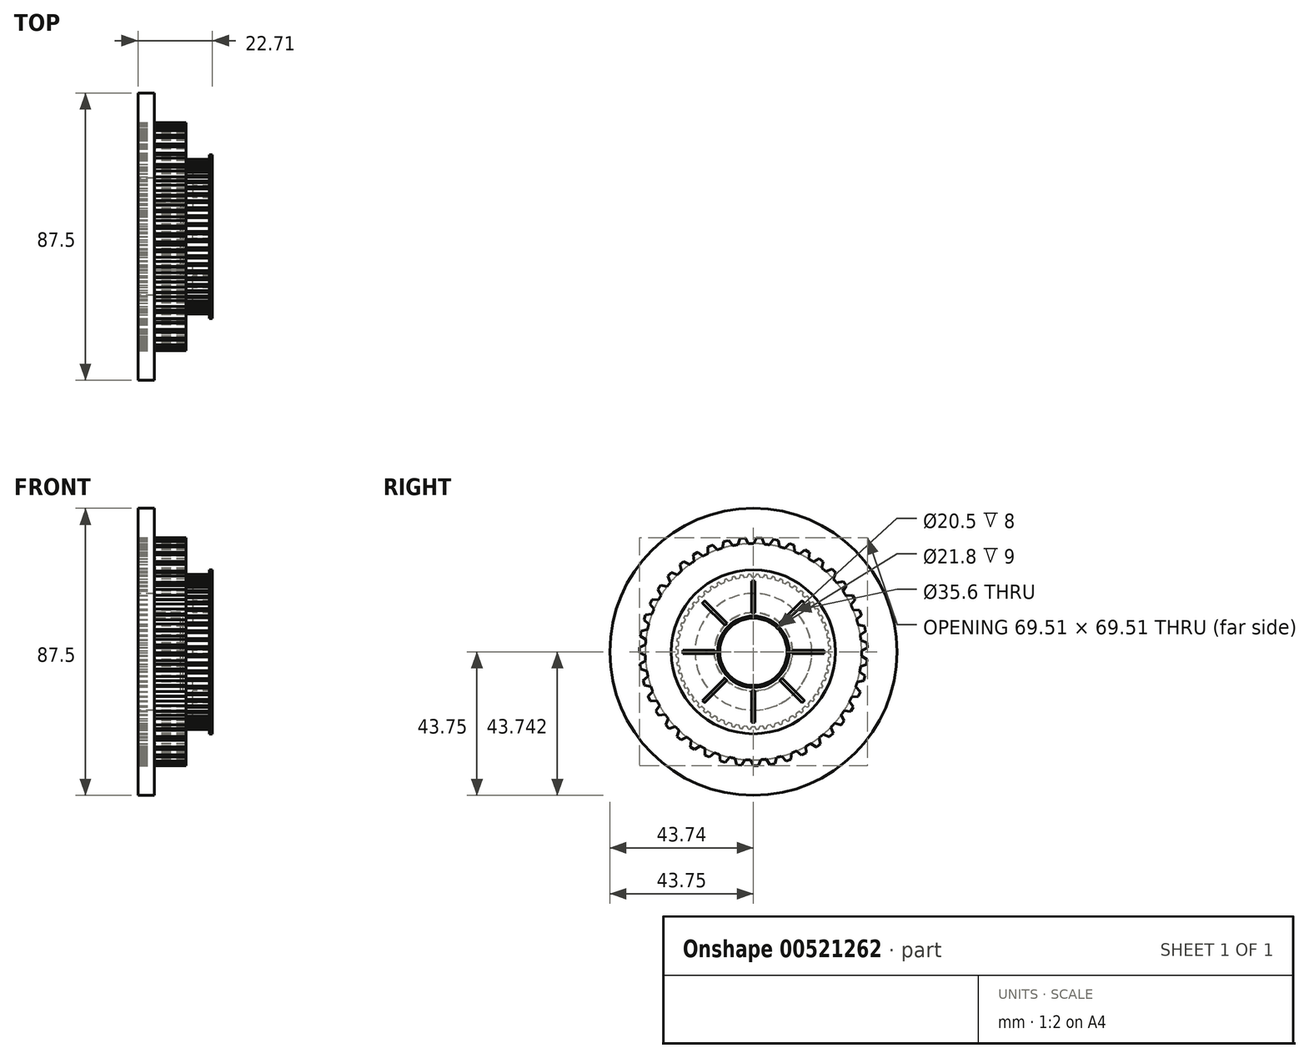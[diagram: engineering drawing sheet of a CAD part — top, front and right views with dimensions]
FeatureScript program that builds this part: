
annotation { "Feature Type Name" : "Feature", "Feature Type Description" : "" }
export const myFeature = defineFeature(function(context is Context, id is Id, definition is map)
    precondition{}
    {
        {
            var Q0;
            Q0=qCreatedBy(makeId("Right.planeOp"),FACE);
            var sketch = newSketch(context, id + "F0", { "sketchPlane" : qUnion([Q0])});
            skCircle(sketch, "E0", {"center": v(0, 0) * mm, "radius": 34.77 * mm, "construction": true});
            skCircle(sketch, "E1", {"center": v(0, 0) * mm, "radius": 10.25 * mm});
            skCircle(sketch, "E2", {"center": v(0, 0) * mm, "radius": 43.75 * mm});
            skCircle(sketch, "E3", {"center": v(0, 0) * mm, "radius": 12 * mm});
            skLineSegment(sketch, "E4", {"start": v(-2.5, 34.67) * mm, "end": v(2.5, 34.67) * mm, "construction": true});
            skCircle(sketch, "E5", {"center": v(0, 0) * mm, "radius": 32.97 * mm});
            skLineSegment(sketch, "E6", {"start": v(0, 0) * mm, "end": v(0, 46.74) * mm, "construction": true});
            skLineSegment(sketch, "E7", {"start": v(-2.5, 34.67) * mm, "end": v(-1.53, 32.93) * mm});
            skLineSegment(sketch, "E8", {"start": v(-1.53, 32.93) * mm, "end": v(0.13, 32.96) * mm});
            skLineSegment(sketch, "E9", {"start": v(0.13, 32.96) * mm, "end": v(1.03, 34.75) * mm});
            skLineSegment(sketch, "E10", {"start": v(1.03, 34.75) * mm, "end": v(2.5, 34.67) * mm});
            skLineSegment(sketch, "E11", {"start": v(-2.5, 34.67) * mm, "end": v(0, 0) * mm, "construction": true});
            skLineSegment(sketch, "E12", {"start": v(1.03, 34.75) * mm, "end": v(0, 0) * mm, "construction": true});
            skLineSegment(sketch, "E13", {"start": v(-2.5, 34.67) * mm, "end": v(-2.37, 32.88) * mm, "construction": true});
            skLineSegment(sketch, "E14", {"start": v(-2.37, 32.88) * mm, "end": v(0.13, 32.96) * mm});
            skLineSegment(sketch, "E15.1.0", {"start": v(-7.52, 33.94) * mm, "end": v(-6.3, 32.36) * mm});
            skLineSegment(sketch, "E15.1.1", {"start": v(-6.3, 32.36) * mm, "end": v(-4.67, 32.63) * mm});
            skLineSegment(sketch, "E15.1.2", {"start": v(-4.67, 32.63) * mm, "end": v(-4.05, 34.53) * mm});
            skLineSegment(sketch, "E15.1.3", {"start": v(-4.05, 34.53) * mm, "end": v(-2.58, 34.67) * mm});
            skLineSegment(sketch, "E15.2.0", {"start": v(-12.38, 32.48) * mm, "end": v(-10.95, 31.1) * mm});
            skLineSegment(sketch, "E15.2.1", {"start": v(-10.95, 31.1) * mm, "end": v(-9.37, 31.6) * mm});
            skLineSegment(sketch, "E15.2.2", {"start": v(-9.37, 31.6) * mm, "end": v(-9.03, 33.57) * mm});
            skLineSegment(sketch, "E15.2.3", {"start": v(-9.03, 33.57) * mm, "end": v(-7.6, 33.93) * mm});
            skLineSegment(sketch, "E15.3.0", {"start": v(-16.98, 30.34) * mm, "end": v(-15.36, 29.17) * mm});
            skLineSegment(sketch, "E15.3.1", {"start": v(-15.36, 29.17) * mm, "end": v(-13.88, 29.9) * mm});
            skLineSegment(sketch, "E15.3.2", {"start": v(-13.88, 29.9) * mm, "end": v(-13.82, 31.9) * mm});
            skLineSegment(sketch, "E15.3.3", {"start": v(-13.82, 31.9) * mm, "end": v(-12.45, 32.46) * mm});
            skLineSegment(sketch, "E15.4.0", {"start": v(-21.22, 27.54) * mm, "end": v(-19.44, 26.62) * mm});
            skLineSegment(sketch, "E15.4.1", {"start": v(-19.44, 26.62) * mm, "end": v(-18.08, 27.56) * mm});
            skLineSegment(sketch, "E15.4.2", {"start": v(-18.08, 27.56) * mm, "end": v(-18.32, 29.55) * mm});
            skLineSegment(sketch, "E15.4.3", {"start": v(-18.32, 29.55) * mm, "end": v(-17.05, 30.3) * mm});
            skLineSegment(sketch, "E15.5.0", {"start": v(-25, 24.16) * mm, "end": v(-23.11, 23.5) * mm});
            skLineSegment(sketch, "E15.5.1", {"start": v(-23.11, 23.5) * mm, "end": v(-21.9, 24.64) * mm});
            skLineSegment(sketch, "E15.5.2", {"start": v(-21.9, 24.64) * mm, "end": v(-22.43, 26.57) * mm});
            skLineSegment(sketch, "E15.5.3", {"start": v(-22.43, 26.57) * mm, "end": v(-21.28, 27.5) * mm});
            skLineSegment(sketch, "E15.6.0", {"start": v(-28.25, 20.26) * mm, "end": v(-26.29, 19.9) * mm});
            skLineSegment(sketch, "E15.6.1", {"start": v(-26.29, 19.9) * mm, "end": v(-25.26, 21.19) * mm});
            skLineSegment(sketch, "E15.6.2", {"start": v(-25.26, 21.19) * mm, "end": v(-26.05, 23.02) * mm});
            skLineSegment(sketch, "E15.6.3", {"start": v(-26.05, 23.02) * mm, "end": v(-25.05, 24.1) * mm});
            skLineSegment(sketch, "E15.7.0", {"start": v(-30.9, 15.93) * mm, "end": v(-28.9, 15.85) * mm});
            skLineSegment(sketch, "E15.7.1", {"start": v(-28.9, 15.85) * mm, "end": v(-28.07, 17.28) * mm});
            skLineSegment(sketch, "E15.7.2", {"start": v(-28.07, 17.28) * mm, "end": v(-29.13, 18.98) * mm});
            skLineSegment(sketch, "E15.7.3", {"start": v(-29.13, 18.98) * mm, "end": v(-28.3, 20.2) * mm});
            skLineSegment(sketch, "E15.8.0", {"start": v(-32.9, 11.26) * mm, "end": v(-30.9, 11.47) * mm});
            skLineSegment(sketch, "E15.8.1", {"start": v(-30.9, 11.47) * mm, "end": v(-30.29, 13.01) * mm});
            skLineSegment(sketch, "E15.8.2", {"start": v(-30.29, 13.01) * mm, "end": v(-31.58, 14.53) * mm});
            skLineSegment(sketch, "E15.8.3", {"start": v(-31.58, 14.53) * mm, "end": v(-30.94, 15.86) * mm});
            skLineSegment(sketch, "E15.9.0", {"start": v(-34.18, 6.35) * mm, "end": v(-32.25, 6.85) * mm});
            skLineSegment(sketch, "E15.9.1", {"start": v(-32.25, 6.85) * mm, "end": v(-31.86, 8.46) * mm});
            skLineSegment(sketch, "E15.9.2", {"start": v(-31.86, 8.46) * mm, "end": v(-33.36, 9.78) * mm});
            skLineSegment(sketch, "E15.9.3", {"start": v(-33.36, 9.78) * mm, "end": v(-32.92, 11.19) * mm});
            skLineSegment(sketch, "E15.10.0", {"start": v(-34.74, 1.3) * mm, "end": v(-32.9, 2.08) * mm});
            skLineSegment(sketch, "E15.10.1", {"start": v(-32.9, 2.08) * mm, "end": v(-32.75, 3.73) * mm});
            skLineSegment(sketch, "E15.10.2", {"start": v(-32.75, 3.73) * mm, "end": v(-34.43, 4.82) * mm});
            skLineSegment(sketch, "E15.10.3", {"start": v(-34.43, 4.82) * mm, "end": v(-34.2, 6.28) * mm});
            skLineSegment(sketch, "E15.11.0", {"start": v(-34.56, -3.76) * mm, "end": v(-32.85, -2.73) * mm});
            skLineSegment(sketch, "E15.11.1", {"start": v(-32.85, -2.73) * mm, "end": v(-32.95, -1.08) * mm});
            skLineSegment(sketch, "E15.11.2", {"start": v(-32.95, -1.08) * mm, "end": v(-34.76, -0.24) * mm});
            skLineSegment(sketch, "E15.11.3", {"start": v(-34.76, -0.24) * mm, "end": v(-34.74, 1.23) * mm});
            skLineSegment(sketch, "E15.12.0", {"start": v(-33.64, -8.76) * mm, "end": v(-32.1, -7.48) * mm});
            skLineSegment(sketch, "E15.12.1", {"start": v(-32.1, -7.48) * mm, "end": v(-32.44, -5.86) * mm});
            skLineSegment(sketch, "E15.12.2", {"start": v(-32.44, -5.86) * mm, "end": v(-34.36, -5.3) * mm});
            skLineSegment(sketch, "E15.12.3", {"start": v(-34.36, -5.3) * mm, "end": v(-34.55, -3.84) * mm});
            skLineSegment(sketch, "E15.13.0", {"start": v(-32.01, -13.56) * mm, "end": v(-30.67, -12.08) * mm});
            skLineSegment(sketch, "E15.13.1", {"start": v(-30.67, -12.08) * mm, "end": v(-31.24, -10.52) * mm});
            skLineSegment(sketch, "E15.13.2", {"start": v(-31.24, -10.52) * mm, "end": v(-33.22, -10.25) * mm});
            skLineSegment(sketch, "E15.13.3", {"start": v(-33.22, -10.25) * mm, "end": v(-33.62, -8.83) * mm});
            skLineSegment(sketch, "E15.14.0", {"start": v(-29.7, -18.08) * mm, "end": v(-28.59, -16.42) * mm});
            skLineSegment(sketch, "E15.14.1", {"start": v(-28.59, -16.42) * mm, "end": v(-29.38, -14.96) * mm});
            skLineSegment(sketch, "E15.14.2", {"start": v(-29.38, -14.96) * mm, "end": v(-31.37, -14.98) * mm});
            skLineSegment(sketch, "E15.14.3", {"start": v(-31.37, -14.98) * mm, "end": v(-31.98, -13.63) * mm});
            skLineSegment(sketch, "E15.15.0", {"start": v(-26.75, -22.2) * mm, "end": v(-25.9, -20.4) * mm});
            skLineSegment(sketch, "E15.15.1", {"start": v(-25.9, -20.4) * mm, "end": v(-26.88, -19.08) * mm});
            skLineSegment(sketch, "E15.15.2", {"start": v(-26.88, -19.08) * mm, "end": v(-28.86, -19.39) * mm});
            skLineSegment(sketch, "E15.15.3", {"start": v(-28.86, -19.39) * mm, "end": v(-29.66, -18.14) * mm});
            skLineSegment(sketch, "E15.16.0", {"start": v(-23.23, -25.87) * mm, "end": v(-22.65, -23.96) * mm});
            skLineSegment(sketch, "E15.16.1", {"start": v(-22.65, -23.96) * mm, "end": v(-23.82, -22.79) * mm});
            skLineSegment(sketch, "E15.16.2", {"start": v(-23.82, -22.79) * mm, "end": v(-25.73, -23.38) * mm});
            skLineSegment(sketch, "E15.16.3", {"start": v(-25.73, -23.38) * mm, "end": v(-26.7, -22.27) * mm});
            skLineSegment(sketch, "E15.17.0", {"start": v(-19.21, -28.97) * mm, "end": v(-18.92, -27) * mm});
            skLineSegment(sketch, "E15.17.1", {"start": v(-18.92, -27) * mm, "end": v(-20.25, -26.01) * mm});
            skLineSegment(sketch, "E15.17.2", {"start": v(-20.25, -26.01) * mm, "end": v(-22.05, -26.88) * mm});
            skLineSegment(sketch, "E15.17.3", {"start": v(-22.05, -26.88) * mm, "end": v(-23.17, -25.92) * mm});
            skLineSegment(sketch, "E15.18.0", {"start": v(-14.8, -31.46) * mm, "end": v(-14.78, -29.46) * mm});
            skLineSegment(sketch, "E15.18.1", {"start": v(-14.78, -29.46) * mm, "end": v(-16.25, -28.68) * mm});
            skLineSegment(sketch, "E15.18.2", {"start": v(-16.25, -28.68) * mm, "end": v(-17.9, -29.8) * mm});
            skLineSegment(sketch, "E15.18.3", {"start": v(-17.9, -29.8) * mm, "end": v(-19.15, -29.01) * mm});
            skLineSegment(sketch, "E15.19.0", {"start": v(-10.05, -33.28) * mm, "end": v(-10.34, -31.3) * mm});
            skLineSegment(sketch, "E15.19.1", {"start": v(-10.34, -31.3) * mm, "end": v(-11.9, -30.74) * mm});
            skLineSegment(sketch, "E15.19.2", {"start": v(-11.9, -30.74) * mm, "end": v(-13.37, -32.1) * mm});
            skLineSegment(sketch, "E15.19.3", {"start": v(-13.37, -32.1) * mm, "end": v(-14.72, -31.5) * mm});
            skLineSegment(sketch, "E15.20.0", {"start": v(-5.1, -34.39) * mm, "end": v(-5.67, -32.47) * mm});
            skLineSegment(sketch, "E15.20.1", {"start": v(-5.67, -32.47) * mm, "end": v(-7.3, -32.15) * mm});
            skLineSegment(sketch, "E15.20.2", {"start": v(-7.3, -32.15) * mm, "end": v(-8.56, -33.7) * mm});
            skLineSegment(sketch, "E15.20.3", {"start": v(-8.56, -33.7) * mm, "end": v(-9.98, -33.3) * mm});
            skLineSegment(sketch, "E15.21.0", {"start": v(-0.04, -34.76) * mm, "end": v(-0.88, -32.95) * mm});
            skLineSegment(sketch, "E15.21.1", {"start": v(-0.88, -32.95) * mm, "end": v(-2.53, -32.87) * mm});
            skLineSegment(sketch, "E15.21.2", {"start": v(-2.53, -32.87) * mm, "end": v(-3.56, -34.58) * mm});
            skLineSegment(sketch, "E15.21.3", {"start": v(-3.56, -34.58) * mm, "end": v(-5.02, -34.4) * mm});
            skLineSegment(sketch, "E15.22.0", {"start": v(5.02, -34.4) * mm, "end": v(3.93, -32.73) * mm});
            skLineSegment(sketch, "E15.22.1", {"start": v(3.93, -32.73) * mm, "end": v(2.28, -32.89) * mm});
            skLineSegment(sketch, "E15.22.2", {"start": v(2.28, -32.89) * mm, "end": v(1.51, -34.73) * mm});
            skLineSegment(sketch, "E15.22.3", {"start": v(1.51, -34.73) * mm, "end": v(0.04, -34.76) * mm});
            skLineSegment(sketch, "E15.23.0", {"start": v(9.98, -33.3) * mm, "end": v(8.65, -31.8) * mm});
            skLineSegment(sketch, "E15.23.1", {"start": v(8.65, -31.8) * mm, "end": v(7.04, -32.2) * mm});
            skLineSegment(sketch, "E15.23.2", {"start": v(7.04, -32.2) * mm, "end": v(6.55, -34.14) * mm});
            skLineSegment(sketch, "E15.23.3", {"start": v(6.55, -34.14) * mm, "end": v(5.1, -34.39) * mm});
            skLineSegment(sketch, "E15.24.0", {"start": v(14.72, -31.5) * mm, "end": v(13.2, -30.21) * mm});
            skLineSegment(sketch, "E15.24.1", {"start": v(13.2, -30.21) * mm, "end": v(11.66, -30.84) * mm});
            skLineSegment(sketch, "E15.24.2", {"start": v(11.66, -30.84) * mm, "end": v(11.46, -32.82) * mm});
            skLineSegment(sketch, "E15.24.3", {"start": v(11.46, -32.82) * mm, "end": v(10.05, -33.28) * mm});
            skLineSegment(sketch, "E15.25.0", {"start": v(19.15, -29.01) * mm, "end": v(17.45, -27.97) * mm});
            skLineSegment(sketch, "E15.25.1", {"start": v(17.45, -27.97) * mm, "end": v(16.02, -28.8) * mm});
            skLineSegment(sketch, "E15.25.2", {"start": v(16.02, -28.8) * mm, "end": v(16.11, -30.8) * mm});
            skLineSegment(sketch, "E15.25.3", {"start": v(16.11, -30.8) * mm, "end": v(14.8, -31.46) * mm});
            skLineSegment(sketch, "E15.26.0", {"start": v(23.17, -25.92) * mm, "end": v(21.33, -25.13) * mm});
            skLineSegment(sketch, "E15.26.1", {"start": v(21.33, -25.13) * mm, "end": v(20.05, -26.17) * mm});
            skLineSegment(sketch, "E15.26.2", {"start": v(20.05, -26.17) * mm, "end": v(20.43, -28.13) * mm});
            skLineSegment(sketch, "E15.26.3", {"start": v(20.43, -28.13) * mm, "end": v(19.21, -28.97) * mm});
            skLineSegment(sketch, "E15.27.0", {"start": v(26.7, -22.27) * mm, "end": v(24.77, -21.76) * mm});
            skLineSegment(sketch, "E15.27.1", {"start": v(24.77, -21.76) * mm, "end": v(23.64, -22.97) * mm});
            skLineSegment(sketch, "E15.27.2", {"start": v(23.64, -22.97) * mm, "end": v(24.3, -24.86) * mm});
            skLineSegment(sketch, "E15.27.3", {"start": v(24.3, -24.86) * mm, "end": v(23.23, -25.87) * mm});
            skLineSegment(sketch, "E15.28.0", {"start": v(29.66, -18.14) * mm, "end": v(27.67, -17.92) * mm});
            skLineSegment(sketch, "E15.28.1", {"start": v(27.67, -17.92) * mm, "end": v(26.74, -19.28) * mm});
            skLineSegment(sketch, "E15.28.2", {"start": v(26.74, -19.28) * mm, "end": v(27.67, -21.05) * mm});
            skLineSegment(sketch, "E15.28.3", {"start": v(27.67, -21.05) * mm, "end": v(26.75, -22.2) * mm});
            skLineSegment(sketch, "E15.29.0", {"start": v(31.98, -13.63) * mm, "end": v(29.98, -13.7) * mm});
            skLineSegment(sketch, "E15.29.1", {"start": v(29.98, -13.7) * mm, "end": v(29.26, -15.19) * mm});
            skLineSegment(sketch, "E15.29.2", {"start": v(29.26, -15.19) * mm, "end": v(30.44, -16.8) * mm});
            skLineSegment(sketch, "E15.29.3", {"start": v(30.44, -16.8) * mm, "end": v(29.7, -18.08) * mm});
            skLineSegment(sketch, "E15.30.0", {"start": v(33.62, -8.83) * mm, "end": v(31.66, -9.19) * mm});
            skLineSegment(sketch, "E15.30.1", {"start": v(31.66, -9.19) * mm, "end": v(31.16, -10.76) * mm});
            skLineSegment(sketch, "E15.30.2", {"start": v(31.16, -10.76) * mm, "end": v(32.56, -12.2) * mm});
            skLineSegment(sketch, "E15.30.3", {"start": v(32.56, -12.2) * mm, "end": v(32.01, -13.56) * mm});
            skLineSegment(sketch, "E15.31.0", {"start": v(34.55, -3.84) * mm, "end": v(32.66, -4.48) * mm});
            skLineSegment(sketch, "E15.31.1", {"start": v(32.66, -4.48) * mm, "end": v(32.4, -6.11) * mm});
            skLineSegment(sketch, "E15.31.2", {"start": v(32.4, -6.11) * mm, "end": v(33.99, -7.32) * mm});
            skLineSegment(sketch, "E15.31.3", {"start": v(33.99, -7.32) * mm, "end": v(33.64, -8.76) * mm});
            skLineSegment(sketch, "E15.32.0", {"start": v(34.74, 1.23) * mm, "end": v(32.96, 0.32) * mm});
            skLineSegment(sketch, "E15.32.1", {"start": v(32.96, 0.32) * mm, "end": v(32.94, -1.33) * mm});
            skLineSegment(sketch, "E15.32.2", {"start": v(32.94, -1.33) * mm, "end": v(34.69, -2.3) * mm});
            skLineSegment(sketch, "E15.32.3", {"start": v(34.69, -2.3) * mm, "end": v(34.56, -3.76) * mm});
            skLineSegment(sketch, "E15.33.0", {"start": v(34.2, 6.28) * mm, "end": v(32.56, 5.12) * mm});
            skLineSegment(sketch, "E15.33.1", {"start": v(32.56, 5.12) * mm, "end": v(32.78, 3.48) * mm});
            skLineSegment(sketch, "E15.33.2", {"start": v(32.78, 3.48) * mm, "end": v(34.65, 2.78) * mm});
            skLineSegment(sketch, "E15.33.3", {"start": v(34.65, 2.78) * mm, "end": v(34.74, 1.3) * mm});
            skLineSegment(sketch, "E15.34.0", {"start": v(32.92, 11.19) * mm, "end": v(31.47, 9.8) * mm});
            skLineSegment(sketch, "E15.34.1", {"start": v(31.47, 9.8) * mm, "end": v(31.93, 8.21) * mm});
            skLineSegment(sketch, "E15.34.2", {"start": v(31.93, 8.21) * mm, "end": v(33.88, 7.8) * mm});
            skLineSegment(sketch, "E15.34.3", {"start": v(33.88, 7.8) * mm, "end": v(34.18, 6.35) * mm});
            skLineSegment(sketch, "E15.35.0", {"start": v(30.94, 15.86) * mm, "end": v(29.7, 14.28) * mm});
            skLineSegment(sketch, "E15.35.1", {"start": v(29.7, 14.28) * mm, "end": v(30.39, 12.77) * mm});
            skLineSegment(sketch, "E15.35.2", {"start": v(30.39, 12.77) * mm, "end": v(32.38, 12.65) * mm});
            skLineSegment(sketch, "E15.35.3", {"start": v(32.38, 12.65) * mm, "end": v(32.9, 11.26) * mm});
            skLineSegment(sketch, "E15.36.0", {"start": v(28.3, 20.2) * mm, "end": v(27.31, 18.46) * mm});
            skLineSegment(sketch, "E15.36.1", {"start": v(27.31, 18.46) * mm, "end": v(28.2, 17.06) * mm});
            skLineSegment(sketch, "E15.36.2", {"start": v(28.2, 17.06) * mm, "end": v(30.2, 17.23) * mm});
            skLineSegment(sketch, "E15.36.3", {"start": v(30.2, 17.23) * mm, "end": v(30.9, 15.93) * mm});
            skLineSegment(sketch, "E15.37.0", {"start": v(25.05, 24.1) * mm, "end": v(24.33, 22.24) * mm});
            skLineSegment(sketch, "E15.37.1", {"start": v(24.33, 22.24) * mm, "end": v(25.42, 20.99) * mm});
            skLineSegment(sketch, "E15.37.2", {"start": v(25.42, 20.99) * mm, "end": v(27.37, 21.44) * mm});
            skLineSegment(sketch, "E15.37.3", {"start": v(27.37, 21.44) * mm, "end": v(28.25, 20.26) * mm});
            skLineSegment(sketch, "E15.38.0", {"start": v(21.28, 27.5) * mm, "end": v(20.84, 25.54) * mm});
            skLineSegment(sketch, "E15.38.1", {"start": v(20.84, 25.54) * mm, "end": v(22.1, 24.47) * mm});
            skLineSegment(sketch, "E15.38.2", {"start": v(22.1, 24.47) * mm, "end": v(23.95, 25.2) * mm});
            skLineSegment(sketch, "E15.38.3", {"start": v(23.95, 25.2) * mm, "end": v(25, 24.16) * mm});
            skLineSegment(sketch, "E15.39.0", {"start": v(17.05, 30.3) * mm, "end": v(16.9, 28.3) * mm});
            skLineSegment(sketch, "E15.39.1", {"start": v(16.9, 28.3) * mm, "end": v(18.3, 27.42) * mm});
            skLineSegment(sketch, "E15.39.2", {"start": v(18.3, 27.42) * mm, "end": v(20.03, 28.42) * mm});
            skLineSegment(sketch, "E15.39.3", {"start": v(20.03, 28.42) * mm, "end": v(21.22, 27.54) * mm});
            skLineSegment(sketch, "E15.40.0", {"start": v(12.45, 32.46) * mm, "end": v(12.6, 30.46) * mm});
            skLineSegment(sketch, "E15.40.1", {"start": v(12.6, 30.46) * mm, "end": v(14.1, 29.8) * mm});
            skLineSegment(sketch, "E15.40.2", {"start": v(14.1, 29.8) * mm, "end": v(15.68, 31.03) * mm});
            skLineSegment(sketch, "E15.40.3", {"start": v(15.68, 31.03) * mm, "end": v(16.98, 30.34) * mm});
            skLineSegment(sketch, "E15.41.0", {"start": v(7.6, 33.93) * mm, "end": v(8.02, 31.97) * mm});
            skLineSegment(sketch, "E15.41.1", {"start": v(8.02, 31.97) * mm, "end": v(9.62, 31.53) * mm});
            skLineSegment(sketch, "E15.41.2", {"start": v(9.62, 31.53) * mm, "end": v(11, 32.98) * mm});
            skLineSegment(sketch, "E15.41.3", {"start": v(11, 32.98) * mm, "end": v(12.38, 32.48) * mm});
            skLineSegment(sketch, "E15.42.0", {"start": v(2.58, 34.67) * mm, "end": v(3.28, 32.8) * mm});
            skLineSegment(sketch, "E15.42.1", {"start": v(3.28, 32.8) * mm, "end": v(4.93, 32.6) * mm});
            skLineSegment(sketch, "E15.42.2", {"start": v(4.93, 32.6) * mm, "end": v(6.07, 34.23) * mm});
            skLineSegment(sketch, "E15.42.3", {"start": v(6.07, 34.23) * mm, "end": v(7.52, 33.94) * mm});
            skLineSegment(sketch, "E16", {"start": v(2.5, 34.67) * mm, "end": v(2.58, 34.67) * mm});
            skLineSegment(sketch, "E17.1.0", {"start": v(-2.58, 34.67) * mm, "end": v(-2.5, 34.67) * mm});
            skLineSegment(sketch, "E17.2.0", {"start": v(-7.6, 33.93) * mm, "end": v(-7.52, 33.94) * mm});
            skLineSegment(sketch, "E17.3.0", {"start": v(-12.45, 32.46) * mm, "end": v(-12.38, 32.48) * mm});
            skLineSegment(sketch, "E17.4.0", {"start": v(-17.05, 30.3) * mm, "end": v(-16.98, 30.34) * mm});
            skLineSegment(sketch, "E17.5.0", {"start": v(-21.28, 27.5) * mm, "end": v(-21.22, 27.54) * mm});
            skLineSegment(sketch, "E17.6.0", {"start": v(-25.05, 24.1) * mm, "end": v(-25, 24.16) * mm});
            skLineSegment(sketch, "E17.7.0", {"start": v(-28.3, 20.2) * mm, "end": v(-28.25, 20.26) * mm});
            skLineSegment(sketch, "E17.8.0", {"start": v(-30.94, 15.86) * mm, "end": v(-30.9, 15.93) * mm});
            skLineSegment(sketch, "E17.9.0", {"start": v(-32.92, 11.19) * mm, "end": v(-32.9, 11.26) * mm});
            skLineSegment(sketch, "E17.10.0", {"start": v(-34.2, 6.28) * mm, "end": v(-34.18, 6.35) * mm});
            skLineSegment(sketch, "E17.11.0", {"start": v(-34.74, 1.23) * mm, "end": v(-34.74, 1.3) * mm});
            skLineSegment(sketch, "E17.12.0", {"start": v(-34.55, -3.84) * mm, "end": v(-34.56, -3.76) * mm});
            skLineSegment(sketch, "E17.13.0", {"start": v(-33.62, -8.83) * mm, "end": v(-33.64, -8.76) * mm});
            skLineSegment(sketch, "E17.14.0", {"start": v(-31.98, -13.63) * mm, "end": v(-32.01, -13.56) * mm});
            skLineSegment(sketch, "E17.15.0", {"start": v(-29.66, -18.14) * mm, "end": v(-29.7, -18.08) * mm});
            skLineSegment(sketch, "E17.16.0", {"start": v(-26.7, -22.27) * mm, "end": v(-26.75, -22.2) * mm});
            skLineSegment(sketch, "E17.17.0", {"start": v(-23.17, -25.92) * mm, "end": v(-23.23, -25.87) * mm});
            skLineSegment(sketch, "E17.18.0", {"start": v(-19.15, -29.01) * mm, "end": v(-19.21, -28.97) * mm});
            skLineSegment(sketch, "E17.19.0", {"start": v(-14.72, -31.5) * mm, "end": v(-14.8, -31.46) * mm});
            skLineSegment(sketch, "E17.20.0", {"start": v(-9.98, -33.3) * mm, "end": v(-10.05, -33.28) * mm});
            skLineSegment(sketch, "E17.21.0", {"start": v(-5.02, -34.4) * mm, "end": v(-5.1, -34.39) * mm});
            skLineSegment(sketch, "E17.22.0", {"start": v(0.04, -34.76) * mm, "end": v(-0.04, -34.76) * mm});
            skLineSegment(sketch, "E17.23.0", {"start": v(5.1, -34.39) * mm, "end": v(5.02, -34.4) * mm});
            skLineSegment(sketch, "E17.24.0", {"start": v(10.05, -33.28) * mm, "end": v(9.98, -33.3) * mm});
            skLineSegment(sketch, "E17.25.0", {"start": v(14.8, -31.46) * mm, "end": v(14.72, -31.5) * mm});
            skLineSegment(sketch, "E17.26.0", {"start": v(19.21, -28.97) * mm, "end": v(19.15, -29.01) * mm});
            skLineSegment(sketch, "E17.27.0", {"start": v(23.23, -25.87) * mm, "end": v(23.17, -25.92) * mm});
            skLineSegment(sketch, "E17.28.0", {"start": v(26.75, -22.2) * mm, "end": v(26.7, -22.27) * mm});
            skLineSegment(sketch, "E17.29.0", {"start": v(29.7, -18.08) * mm, "end": v(29.66, -18.14) * mm});
            skLineSegment(sketch, "E17.30.0", {"start": v(32.01, -13.56) * mm, "end": v(31.98, -13.63) * mm});
            skLineSegment(sketch, "E17.31.0", {"start": v(33.64, -8.76) * mm, "end": v(33.62, -8.83) * mm});
            skLineSegment(sketch, "E17.32.0", {"start": v(34.56, -3.76) * mm, "end": v(34.55, -3.84) * mm});
            skLineSegment(sketch, "E17.33.0", {"start": v(34.74, 1.3) * mm, "end": v(34.74, 1.23) * mm});
            skLineSegment(sketch, "E17.34.0", {"start": v(34.18, 6.35) * mm, "end": v(34.2, 6.28) * mm});
            skLineSegment(sketch, "E17.35.0", {"start": v(32.9, 11.26) * mm, "end": v(32.92, 11.19) * mm});
            skLineSegment(sketch, "E17.36.0", {"start": v(30.9, 15.93) * mm, "end": v(30.94, 15.86) * mm});
            skLineSegment(sketch, "E17.37.0", {"start": v(28.25, 20.26) * mm, "end": v(28.3, 20.2) * mm});
            skLineSegment(sketch, "E17.38.0", {"start": v(25, 24.16) * mm, "end": v(25.05, 24.1) * mm});
            skLineSegment(sketch, "E17.39.0", {"start": v(21.22, 27.54) * mm, "end": v(21.28, 27.5) * mm});
            skLineSegment(sketch, "E17.40.0", {"start": v(16.98, 30.34) * mm, "end": v(17.05, 30.3) * mm});
            skLineSegment(sketch, "E17.41.0", {"start": v(12.38, 32.48) * mm, "end": v(12.45, 32.46) * mm});
            skLineSegment(sketch, "E17.42.0", {"start": v(7.52, 33.94) * mm, "end": v(7.6, 33.93) * mm});
            skSolve(sketch);
        }
        {
            var Q0;
            {var subQ1=sQuery(id+"F0.wireOp",EDGE,"E15.4.0");Q0=makeQuery(id+"F0.imprint","IMPRINT",FACE,{"disambiguationData":[TD([[makeQuery(id+"F0.imprint","IMPRINT",EDGE,{"derivedFrom":subQ1}),-1.0]])]});}
            var Q1;
            {var subQ1=sQuery(id+"F0.wireOp",EDGE,"E15.28.0");Q1=makeQuery(id+"F0.imprint","IMPRINT",FACE,{"disambiguationData":[TD([[makeQuery(id+"F0.imprint","IMPRINT",EDGE,{"derivedFrom":subQ1}),-1.0]])]});}
            var Q2;
            {var subQ1=sQuery(id+"F0.wireOp",EDGE,"E15.41.0");Q2=makeQuery(id+"F0.imprint","IMPRINT",FACE,{"disambiguationData":[TD([[makeQuery(id+"F0.imprint","IMPRINT",EDGE,{"derivedFrom":subQ1}),-1.0]])]});}
            var Q3;
            {var subQ1=sQuery(id+"F0.wireOp",EDGE,"E15.2.0");Q3=makeQuery(id+"F0.imprint","IMPRINT",FACE,{"disambiguationData":[TD([[makeQuery(id+"F0.imprint","IMPRINT",EDGE,{"derivedFrom":subQ1}),-1.0]])]});}
            var Q4;
            {var subQ1=sQuery(id+"F0.wireOp",EDGE,"E15.10.0");Q4=makeQuery(id+"F0.imprint","IMPRINT",FACE,{"disambiguationData":[TD([[makeQuery(id+"F0.imprint","IMPRINT",EDGE,{"derivedFrom":subQ1}),-1.0]])]});}
            var Q5;
            {var subQ1=sQuery(id+"F0.wireOp",EDGE,"E15.26.0");Q5=makeQuery(id+"F0.imprint","IMPRINT",FACE,{"disambiguationData":[TD([[makeQuery(id+"F0.imprint","IMPRINT",EDGE,{"derivedFrom":subQ1}),-1.0]])]});}
            var Q6;
            {var subQ1=sQuery(id+"F0.wireOp",EDGE,"E15.18.0");Q6=makeQuery(id+"F0.imprint","IMPRINT",FACE,{"disambiguationData":[TD([[makeQuery(id+"F0.imprint","IMPRINT",EDGE,{"derivedFrom":subQ1}),-1.0]])]});}
            var Q7;
            {var subQ1=sQuery(id+"F0.wireOp",EDGE,"E15.6.0");Q7=makeQuery(id+"F0.imprint","IMPRINT",FACE,{"disambiguationData":[TD([[makeQuery(id+"F0.imprint","IMPRINT",EDGE,{"derivedFrom":subQ1}),-1.0]])]});}
            var Q8;
            {var subQ1=sQuery(id+"F0.wireOp",EDGE,"E15.14.0");Q8=makeQuery(id+"F0.imprint","IMPRINT",FACE,{"disambiguationData":[TD([[makeQuery(id+"F0.imprint","IMPRINT",EDGE,{"derivedFrom":subQ1}),-1.0]])]});}
            var Q9;
            {var subQ1=sQuery(id+"F0.wireOp",EDGE,"E15.22.0");Q9=makeQuery(id+"F0.imprint","IMPRINT",FACE,{"disambiguationData":[TD([[makeQuery(id+"F0.imprint","IMPRINT",EDGE,{"derivedFrom":subQ1}),-1.0]])]});}
            var Q10;
            {var subQ1=sQuery(id+"F0.wireOp",EDGE,"E15.30.0");Q10=makeQuery(id+"F0.imprint","IMPRINT",FACE,{"disambiguationData":[TD([[makeQuery(id+"F0.imprint","IMPRINT",EDGE,{"derivedFrom":subQ1}),-1.0]])]});}
            var Q11;
            {var subQ1=sQuery(id+"F0.wireOp",EDGE,"E15.31.0");Q11=makeQuery(id+"F0.imprint","IMPRINT",FACE,{"disambiguationData":[TD([[makeQuery(id+"F0.imprint","IMPRINT",EDGE,{"derivedFrom":subQ1}),-1.0]])]});}
            var Q12;
            {var subQ1=sQuery(id+"F0.wireOp",EDGE,"E15.15.0");Q12=makeQuery(id+"F0.imprint","IMPRINT",FACE,{"disambiguationData":[TD([[makeQuery(id+"F0.imprint","IMPRINT",EDGE,{"derivedFrom":subQ1}),-1.0]])]});}
            var Q13;
            {var subQ1=sQuery(id+"F0.wireOp",EDGE,"E15.7.0");Q13=makeQuery(id+"F0.imprint","IMPRINT",FACE,{"disambiguationData":[TD([[makeQuery(id+"F0.imprint","IMPRINT",EDGE,{"derivedFrom":subQ1}),-1.0]])]});}
            var Q14;
            {var subQ1=sQuery(id+"F0.wireOp",EDGE,"E15.25.0");Q14=makeQuery(id+"F0.imprint","IMPRINT",FACE,{"disambiguationData":[TD([[makeQuery(id+"F0.imprint","IMPRINT",EDGE,{"derivedFrom":subQ1}),-1.0]])]});}
            var Q15;
            {var subQ1=sQuery(id+"F0.wireOp",EDGE,"E15.39.0");Q15=makeQuery(id+"F0.imprint","IMPRINT",FACE,{"disambiguationData":[TD([[makeQuery(id+"F0.imprint","IMPRINT",EDGE,{"derivedFrom":subQ1}),-1.0]])]});}
            var Q16;
            {var subQ1=sQuery(id+"F0.wireOp",EDGE,"E15.34.0");Q16=makeQuery(id+"F0.imprint","IMPRINT",FACE,{"disambiguationData":[TD([[makeQuery(id+"F0.imprint","IMPRINT",EDGE,{"derivedFrom":subQ1}),-1.0]])]});}
            var Q17;
            {var subQ1=sQuery(id+"F0.wireOp",EDGE,"E15.35.0");Q17=makeQuery(id+"F0.imprint","IMPRINT",FACE,{"disambiguationData":[TD([[makeQuery(id+"F0.imprint","IMPRINT",EDGE,{"derivedFrom":subQ1}),-1.0]])]});}
            var Q18;
            {var subQ0=sQuery(id+"F0.wireOp",EDGE,"E15.36.0");Q18=makeQuery(id+"F0.imprint","IMPRINT",FACE,{"disambiguationData":[TD([[makeQuery(id+"F0.imprint","IMPRINT",EDGE,{"derivedFrom":subQ0}),-1.0]])]});}
            var Q19;
            {var subQ1=sQuery(id+"F0.wireOp",EDGE,"E15.37.0");Q19=makeQuery(id+"F0.imprint","IMPRINT",FACE,{"disambiguationData":[TD([[makeQuery(id+"F0.imprint","IMPRINT",EDGE,{"derivedFrom":subQ1}),-1.0]])]});}
            var Q20;
            {var subQ1=sQuery(id+"F0.wireOp",EDGE,"E15.1.0");Q20=makeQuery(id+"F0.imprint","IMPRINT",FACE,{"disambiguationData":[TD([[makeQuery(id+"F0.imprint","IMPRINT",EDGE,{"derivedFrom":subQ1}),-1.0]])]});}
            var Q21;
            {var subQ1=sQuery(id+"F0.wireOp",EDGE,"E15.17.0");Q21=makeQuery(id+"F0.imprint","IMPRINT",FACE,{"disambiguationData":[TD([[makeQuery(id+"F0.imprint","IMPRINT",EDGE,{"derivedFrom":subQ1}),-1.0]])]});}
            var Q22;
            {var subQ1=sQuery(id+"F0.wireOp",EDGE,"E15.9.0");Q22=makeQuery(id+"F0.imprint","IMPRINT",FACE,{"disambiguationData":[TD([[makeQuery(id+"F0.imprint","IMPRINT",EDGE,{"derivedFrom":subQ1}),-1.0]])]});}
            var Q23;
            {var subQ1=sQuery(id+"F0.wireOp",EDGE,"E15.40.0");Q23=makeQuery(id+"F0.imprint","IMPRINT",FACE,{"disambiguationData":[TD([[makeQuery(id+"F0.imprint","IMPRINT",EDGE,{"derivedFrom":subQ1}),-1.0]])]});}
            var Q24;
            {var subQ1=sQuery(id+"F0.wireOp",EDGE,"E15.38.0");Q24=makeQuery(id+"F0.imprint","IMPRINT",FACE,{"disambiguationData":[TD([[makeQuery(id+"F0.imprint","IMPRINT",EDGE,{"derivedFrom":subQ1}),-1.0]])]});}
            var Q25;
            {var subQ1=sQuery(id+"F0.wireOp",EDGE,"E15.32.0");Q25=makeQuery(id+"F0.imprint","IMPRINT",FACE,{"disambiguationData":[TD([[makeQuery(id+"F0.imprint","IMPRINT",EDGE,{"derivedFrom":subQ1}),-1.0]])]});}
            var Q26;
            {var subQ1=sQuery(id+"F0.wireOp",EDGE,"E15.33.0");Q26=makeQuery(id+"F0.imprint","IMPRINT",FACE,{"disambiguationData":[TD([[makeQuery(id+"F0.imprint","IMPRINT",EDGE,{"derivedFrom":subQ1}),-1.0]])]});}
            var Q27;
            {var subQ1=sQuery(id+"F0.wireOp",EDGE,"E15.21.0");Q27=makeQuery(id+"F0.imprint","IMPRINT",FACE,{"disambiguationData":[TD([[makeQuery(id+"F0.imprint","IMPRINT",EDGE,{"derivedFrom":subQ1}),-1.0]])]});}
            var Q28;
            {var subQ1=sQuery(id+"F0.wireOp",EDGE,"E15.5.0");Q28=makeQuery(id+"F0.imprint","IMPRINT",FACE,{"disambiguationData":[TD([[makeQuery(id+"F0.imprint","IMPRINT",EDGE,{"derivedFrom":subQ1}),-1.0]])]});}
            var Q29;
            {var subQ1=sQuery(id+"F0.wireOp",EDGE,"E15.29.0");Q29=makeQuery(id+"F0.imprint","IMPRINT",FACE,{"disambiguationData":[TD([[makeQuery(id+"F0.imprint","IMPRINT",EDGE,{"derivedFrom":subQ1}),-1.0]])]});}
            var Q30;
            {var subQ1=sQuery(id+"F0.wireOp",EDGE,"E15.13.0");Q30=makeQuery(id+"F0.imprint","IMPRINT",FACE,{"disambiguationData":[TD([[makeQuery(id+"F0.imprint","IMPRINT",EDGE,{"derivedFrom":subQ1}),-1.0]])]});}
            var Q31;
            {var subQ1=sQuery(id+"F0.wireOp",EDGE,"E15.16.0");Q31=makeQuery(id+"F0.imprint","IMPRINT",FACE,{"disambiguationData":[TD([[makeQuery(id+"F0.imprint","IMPRINT",EDGE,{"derivedFrom":subQ1}),-1.0]])]});}
            var Q32;
            {var subQ1=sQuery(id+"F0.wireOp",EDGE,"E15.8.0");Q32=makeQuery(id+"F0.imprint","IMPRINT",FACE,{"disambiguationData":[TD([[makeQuery(id+"F0.imprint","IMPRINT",EDGE,{"derivedFrom":subQ1}),-1.0]])]});}
            var Q33;
            {var subQ1=sQuery(id+"F0.wireOp",EDGE,"E15.24.0");Q33=makeQuery(id+"F0.imprint","IMPRINT",FACE,{"disambiguationData":[TD([[makeQuery(id+"F0.imprint","IMPRINT",EDGE,{"derivedFrom":subQ1}),-1.0]])]});}
            var Q34;
            {var subQ1=sQuery(id+"F0.wireOp",EDGE,"E15.3.0");Q34=makeQuery(id+"F0.imprint","IMPRINT",FACE,{"disambiguationData":[TD([[makeQuery(id+"F0.imprint","IMPRINT",EDGE,{"derivedFrom":subQ1}),-1.0]])]});}
            var Q35;
            {var subQ1=sQuery(id+"F0.wireOp",EDGE,"E15.11.0");Q35=makeQuery(id+"F0.imprint","IMPRINT",FACE,{"disambiguationData":[TD([[makeQuery(id+"F0.imprint","IMPRINT",EDGE,{"derivedFrom":subQ1}),-1.0]])]});}
            var Q36;
            {var subQ1=sQuery(id+"F0.wireOp",EDGE,"E15.19.0");Q36=makeQuery(id+"F0.imprint","IMPRINT",FACE,{"disambiguationData":[TD([[makeQuery(id+"F0.imprint","IMPRINT",EDGE,{"derivedFrom":subQ1}),-1.0]])]});}
            var Q37;
            {var subQ1=sQuery(id+"F0.wireOp",EDGE,"E15.27.0");Q37=makeQuery(id+"F0.imprint","IMPRINT",FACE,{"disambiguationData":[TD([[makeQuery(id+"F0.imprint","IMPRINT",EDGE,{"derivedFrom":subQ1}),-1.0]])]});}
            var Q38;
            {var subQ1=sQuery(id+"F0.wireOp",EDGE,"E15.20.0");Q38=makeQuery(id+"F0.imprint","IMPRINT",FACE,{"disambiguationData":[TD([[makeQuery(id+"F0.imprint","IMPRINT",EDGE,{"derivedFrom":subQ1}),-1.0]])]});}
            var Q39;
            {var subQ1=sQuery(id+"F0.wireOp",EDGE,"E15.12.0");Q39=makeQuery(id+"F0.imprint","IMPRINT",FACE,{"disambiguationData":[TD([[makeQuery(id+"F0.imprint","IMPRINT",EDGE,{"derivedFrom":subQ1}),-1.0]])]});}
            var Q40;
            {var subQ0=sQuery(id+"F0.wireOp",EDGE,"E15.32.1");Q40=makeQuery(id+"F0.imprint","IMPRINT",FACE,{"disambiguationData":[TD([[makeQuery(id+"F0.imprint","IMPRINT",EDGE,{"derivedFrom":subQ0}),1.0]])]});}
            var Q41;
            {var subQ0=sQuery(id+"F0.wireOp",EDGE,"E15.7.1");Q41=makeQuery(id+"F0.imprint","IMPRINT",FACE,{"disambiguationData":[TD([[makeQuery(id+"F0.imprint","IMPRINT",EDGE,{"derivedFrom":subQ0}),1.0]])]});}
            var Q42;
            {var subQ0=sQuery(id+"F0.wireOp",EDGE,"E15.23.1");Q42=makeQuery(id+"F0.imprint","IMPRINT",FACE,{"disambiguationData":[TD([[makeQuery(id+"F0.imprint","IMPRINT",EDGE,{"derivedFrom":subQ0}),1.0]])]});}
            var Q43;
            {var subQ0=sQuery(id+"F0.wireOp",EDGE,"E15.28.1");Q43=makeQuery(id+"F0.imprint","IMPRINT",FACE,{"disambiguationData":[TD([[makeQuery(id+"F0.imprint","IMPRINT",EDGE,{"derivedFrom":subQ0}),1.0]])]});}
            var Q44;
            {var subQ0=sQuery(id+"F0.wireOp",EDGE,"E15.8.1");Q44=makeQuery(id+"F0.imprint","IMPRINT",FACE,{"disambiguationData":[TD([[makeQuery(id+"F0.imprint","IMPRINT",EDGE,{"derivedFrom":subQ0}),1.0]])]});}
            var Q45;
            {var subQ1=sQuery(id+"F0.wireOp",EDGE,"E9");Q45=makeQuery(id+"F0.imprint","IMPRINT",FACE,{"disambiguationData":[TD([[makeQuery(id+"F0.imprint","IMPRINT",EDGE,{"derivedFrom":subQ1}),-1.0]])]});}
            var Q46;
            {var subQ1=sQuery(id+"F0.wireOp",EDGE,"E15.23.0");Q46=makeQuery(id+"F0.imprint","IMPRINT",FACE,{"disambiguationData":[TD([[makeQuery(id+"F0.imprint","IMPRINT",EDGE,{"derivedFrom":subQ1}),-1.0]])]});}
            var Q47;
            {var subQ0=sQuery(id+"F0.wireOp",EDGE,"E15.13.1");Q47=makeQuery(id+"F0.imprint","IMPRINT",FACE,{"disambiguationData":[TD([[makeQuery(id+"F0.imprint","IMPRINT",EDGE,{"derivedFrom":subQ0}),1.0]])]});}
            var Q48;
            {var subQ0=sQuery(id+"F0.wireOp",EDGE,"E15.5.1");Q48=makeQuery(id+"F0.imprint","IMPRINT",FACE,{"disambiguationData":[TD([[makeQuery(id+"F0.imprint","IMPRINT",EDGE,{"derivedFrom":subQ0}),1.0]])]});}
            var Q49;
            {var subQ0=sQuery(id+"F0.wireOp",EDGE,"E15.30.1");Q49=makeQuery(id+"F0.imprint","IMPRINT",FACE,{"disambiguationData":[TD([[makeQuery(id+"F0.imprint","IMPRINT",EDGE,{"derivedFrom":subQ0}),1.0]])]});}
            var Q50;
            {var subQ0=sQuery(id+"F0.wireOp",EDGE,"E15.22.1");Q50=makeQuery(id+"F0.imprint","IMPRINT",FACE,{"disambiguationData":[TD([[makeQuery(id+"F0.imprint","IMPRINT",EDGE,{"derivedFrom":subQ0}),1.0]])]});}
            var Q51;
            {var subQ0=sQuery(id+"F0.wireOp",EDGE,"E15.14.1");Q51=makeQuery(id+"F0.imprint","IMPRINT",FACE,{"disambiguationData":[TD([[makeQuery(id+"F0.imprint","IMPRINT",EDGE,{"derivedFrom":subQ0}),1.0]])]});}
            var Q52;
            {var subQ0=sQuery(id+"F0.wireOp",EDGE,"E15.40.1");Q52=makeQuery(id+"F0.imprint","IMPRINT",FACE,{"disambiguationData":[TD([[makeQuery(id+"F0.imprint","IMPRINT",EDGE,{"derivedFrom":subQ0}),1.0]])]});}
            var Q53;
            {var subQ1=sQuery(id+"F0.wireOp",EDGE,"E7");Q53=makeQuery(id+"F0.imprint","IMPRINT",FACE,{"disambiguationData":[TD([[makeQuery(id+"F0.imprint","IMPRINT",EDGE,{"derivedFrom":subQ1}),-1.0]])]});}
            var Q54;
            {var subQ0=sQuery(id+"F0.wireOp",EDGE,"E15.11.1");Q54=makeQuery(id+"F0.imprint","IMPRINT",FACE,{"disambiguationData":[TD([[makeQuery(id+"F0.imprint","IMPRINT",EDGE,{"derivedFrom":subQ0}),1.0]])]});}
            var Q55;
            {var subQ0=sQuery(id+"F0.wireOp",EDGE,"E15.10.1");Q55=makeQuery(id+"F0.imprint","IMPRINT",FACE,{"disambiguationData":[TD([[makeQuery(id+"F0.imprint","IMPRINT",EDGE,{"derivedFrom":subQ0}),1.0]])]});}
            var Q56;
            {var subQ0=sQuery(id+"F0.wireOp",EDGE,"E15.2.1");Q56=makeQuery(id+"F0.imprint","IMPRINT",FACE,{"disambiguationData":[TD([[makeQuery(id+"F0.imprint","IMPRINT",EDGE,{"derivedFrom":subQ0}),1.0]])]});}
            var Q57;
            {var subQ0=sQuery(id+"F0.wireOp",EDGE,"E15.12.1");Q57=makeQuery(id+"F0.imprint","IMPRINT",FACE,{"disambiguationData":[TD([[makeQuery(id+"F0.imprint","IMPRINT",EDGE,{"derivedFrom":subQ0}),1.0]])]});}
            var Q58;
            {var subQ0=sQuery(id+"F0.wireOp",EDGE,"E15.24.1");Q58=makeQuery(id+"F0.imprint","IMPRINT",FACE,{"disambiguationData":[TD([[makeQuery(id+"F0.imprint","IMPRINT",EDGE,{"derivedFrom":subQ0}),1.0]])]});}
            var Q59;
            {var subQ0=sQuery(id+"F0.wireOp",EDGE,"E15.15.1");Q59=makeQuery(id+"F0.imprint","IMPRINT",FACE,{"disambiguationData":[TD([[makeQuery(id+"F0.imprint","IMPRINT",EDGE,{"derivedFrom":subQ0}),1.0]])]});}
            var Q60;
            {var subQ0=sQuery(id+"F0.wireOp",EDGE,"E15.31.1");Q60=makeQuery(id+"F0.imprint","IMPRINT",FACE,{"disambiguationData":[TD([[makeQuery(id+"F0.imprint","IMPRINT",EDGE,{"derivedFrom":subQ0}),1.0]])]});}
            var Q61;
            {var subQ0=sQuery(id+"F0.wireOp",EDGE,"E15.20.1");Q61=makeQuery(id+"F0.imprint","IMPRINT",FACE,{"disambiguationData":[TD([[makeQuery(id+"F0.imprint","IMPRINT",EDGE,{"derivedFrom":subQ0}),1.0]])]});}
            var Q62;
            {var subQ0=sQuery(id+"F0.wireOp",EDGE,"E15.41.1");Q62=makeQuery(id+"F0.imprint","IMPRINT",FACE,{"disambiguationData":[TD([[makeQuery(id+"F0.imprint","IMPRINT",EDGE,{"derivedFrom":subQ0}),1.0]])]});}
            var Q63;
            {var subQ0=sQuery(id+"F0.wireOp",EDGE,"E15.16.1");Q63=makeQuery(id+"F0.imprint","IMPRINT",FACE,{"disambiguationData":[TD([[makeQuery(id+"F0.imprint","IMPRINT",EDGE,{"derivedFrom":subQ0}),1.0]])]});}
            var Q64;
            {var subQ0=sQuery(id+"F0.wireOp",EDGE,"E15.42.1");Q64=makeQuery(id+"F0.imprint","IMPRINT",FACE,{"disambiguationData":[TD([[makeQuery(id+"F0.imprint","IMPRINT",EDGE,{"derivedFrom":subQ0}),1.0]])]});}
            var Q65;
            {var subQ0=sQuery(id+"F0.wireOp",EDGE,"E15.29.1");Q65=makeQuery(id+"F0.imprint","IMPRINT",FACE,{"disambiguationData":[TD([[makeQuery(id+"F0.imprint","IMPRINT",EDGE,{"derivedFrom":subQ0}),1.0]])]});}
            var Q66;
            {var subQ0=sQuery(id+"F0.wireOp",EDGE,"E15.21.1");Q66=makeQuery(id+"F0.imprint","IMPRINT",FACE,{"disambiguationData":[TD([[makeQuery(id+"F0.imprint","IMPRINT",EDGE,{"derivedFrom":subQ0}),1.0]])]});}
            var Q67;
            {var subQ0=sQuery(id+"F0.wireOp",EDGE,"E15.35.1");Q67=makeQuery(id+"F0.imprint","IMPRINT",FACE,{"disambiguationData":[TD([[makeQuery(id+"F0.imprint","IMPRINT",EDGE,{"derivedFrom":subQ0}),1.0]])]});}
            var Q68;
            {var subQ0=sQuery(id+"F0.wireOp",EDGE,"E15.36.1");Q68=makeQuery(id+"F0.imprint","IMPRINT",FACE,{"disambiguationData":[TD([[makeQuery(id+"F0.imprint","IMPRINT",EDGE,{"derivedFrom":subQ0}),1.0]])]});}
            var Q69;
            {var subQ0=sQuery(id+"F0.wireOp",EDGE,"E15.37.1");Q69=makeQuery(id+"F0.imprint","IMPRINT",FACE,{"disambiguationData":[TD([[makeQuery(id+"F0.imprint","IMPRINT",EDGE,{"derivedFrom":subQ0}),1.0]])]});}
            var Q70;
            {var subQ0=sQuery(id+"F0.wireOp",EDGE,"E15.39.1");Q70=makeQuery(id+"F0.imprint","IMPRINT",FACE,{"disambiguationData":[TD([[makeQuery(id+"F0.imprint","IMPRINT",EDGE,{"derivedFrom":subQ0}),1.0]])]});}
            var Q71;
            {var subQ0=sQuery(id+"F0.wireOp",EDGE,"E15.38.1");Q71=makeQuery(id+"F0.imprint","IMPRINT",FACE,{"disambiguationData":[TD([[makeQuery(id+"F0.imprint","IMPRINT",EDGE,{"derivedFrom":subQ0}),1.0]])]});}
            var Q72;
            {var subQ0=sQuery(id+"F0.wireOp",EDGE,"E15.33.1");Q72=makeQuery(id+"F0.imprint","IMPRINT",FACE,{"disambiguationData":[TD([[makeQuery(id+"F0.imprint","IMPRINT",EDGE,{"derivedFrom":subQ0}),1.0]])]});}
            var Q73;
            {var subQ0=sQuery(id+"F0.wireOp",EDGE,"E15.34.1");Q73=makeQuery(id+"F0.imprint","IMPRINT",FACE,{"disambiguationData":[TD([[makeQuery(id+"F0.imprint","IMPRINT",EDGE,{"derivedFrom":subQ0}),1.0]])]});}
            var Q74;
            {var subQ0=sQuery(id+"F0.wireOp",EDGE,"E15.3.1");Q74=makeQuery(id+"F0.imprint","IMPRINT",FACE,{"disambiguationData":[TD([[makeQuery(id+"F0.imprint","IMPRINT",EDGE,{"derivedFrom":subQ0}),1.0]])]});}
            var Q75;
            {var subQ0=sQuery(id+"F0.wireOp",EDGE,"E15.19.1");Q75=makeQuery(id+"F0.imprint","IMPRINT",FACE,{"disambiguationData":[TD([[makeQuery(id+"F0.imprint","IMPRINT",EDGE,{"derivedFrom":subQ0}),1.0]])]});}
            var Q76;
            {var subQ0=sQuery(id+"F0.wireOp",EDGE,"E15.27.1");Q76=makeQuery(id+"F0.imprint","IMPRINT",FACE,{"disambiguationData":[TD([[makeQuery(id+"F0.imprint","IMPRINT",EDGE,{"derivedFrom":subQ0}),1.0]])]});}
            var Q77;
            {var subQ0=sQuery(id+"F0.wireOp",EDGE,"E15.25.1");Q77=makeQuery(id+"F0.imprint","IMPRINT",FACE,{"disambiguationData":[TD([[makeQuery(id+"F0.imprint","IMPRINT",EDGE,{"derivedFrom":subQ0}),1.0]])]});}
            var Q78;
            {var subQ0=sQuery(id+"F0.wireOp",EDGE,"E15.26.1");Q78=makeQuery(id+"F0.imprint","IMPRINT",FACE,{"disambiguationData":[TD([[makeQuery(id+"F0.imprint","IMPRINT",EDGE,{"derivedFrom":subQ0}),1.0]])]});}
            var Q79;
            {var subQ0=sQuery(id+"F0.wireOp",EDGE,"E15.18.1");Q79=makeQuery(id+"F0.imprint","IMPRINT",FACE,{"disambiguationData":[TD([[makeQuery(id+"F0.imprint","IMPRINT",EDGE,{"derivedFrom":subQ0}),1.0]])]});}
            var Q80;
            {var subQ1=sQuery(id+"F0.wireOp",EDGE,"E8");Q80=makeQuery(id+"F0.imprint","IMPRINT",FACE,{"disambiguationData":[TD([[makeQuery(id+"F0.imprint","IMPRINT",EDGE,{"derivedFrom":subQ1}),-1.0]])]});}
            var Q81;
            {var subQ0=sQuery(id+"F0.wireOp",EDGE,"E15.1.1");Q81=makeQuery(id+"F0.imprint","IMPRINT",FACE,{"disambiguationData":[TD([[makeQuery(id+"F0.imprint","IMPRINT",EDGE,{"derivedFrom":subQ0}),1.0]])]});}
            var Q82;
            {var subQ0=sQuery(id+"F0.wireOp",EDGE,"E15.9.1");Q82=makeQuery(id+"F0.imprint","IMPRINT",FACE,{"disambiguationData":[TD([[makeQuery(id+"F0.imprint","IMPRINT",EDGE,{"derivedFrom":subQ0}),1.0]])]});}
            var Q83;
            {var subQ0=sQuery(id+"F0.wireOp",EDGE,"E15.17.1");Q83=makeQuery(id+"F0.imprint","IMPRINT",FACE,{"disambiguationData":[TD([[makeQuery(id+"F0.imprint","IMPRINT",EDGE,{"derivedFrom":subQ0}),1.0]])]});}
            var Q84;
            {var subQ0=sQuery(id+"F0.wireOp",EDGE,"E15.4.1");Q84=makeQuery(id+"F0.imprint","IMPRINT",FACE,{"disambiguationData":[TD([[makeQuery(id+"F0.imprint","IMPRINT",EDGE,{"derivedFrom":subQ0}),1.0]])]});}
            var Q85;
            {var subQ0=sQuery(id+"F0.wireOp",EDGE,"E8");Q85=makeQuery(id+"F0.imprint","IMPRINT",FACE,{"disambiguationData":[TD([[makeQuery(id+"F0.imprint","IMPRINT",EDGE,{"derivedFrom":subQ0}),1.0]])]});}
            var Q86;
            {var subQ0=sQuery(id+"F0.wireOp",EDGE,"E15.6.1");Q86=makeQuery(id+"F0.imprint","IMPRINT",FACE,{"disambiguationData":[TD([[makeQuery(id+"F0.imprint","IMPRINT",EDGE,{"derivedFrom":subQ0}),1.0]])]});}
            var Q87;
            Q87=makeQuery(id+"F0.imprint","IMPRINT",FACE,{"disambiguationData":[TD([[makeQuery(id+"F0.imprint","IMPRINT",EDGE,{"derivedFrom":sQuery(id+"F0.wireOp",EDGE,"E3")}),-1.0]])]});
            extrude(context, id + "F1", {"entities" : qUnion([Q0, Q1, Q2, Q3, Q4, Q5, Q6, Q7, Q8, Q9, Q10, Q11, Q12, Q13, Q14, Q15, Q16, Q17, Q18, Q19, Q20, Q21, Q22, Q23, Q24, Q25, Q26, Q27, Q28, Q29, Q30, Q31, Q32, Q33, Q34, Q35, Q36, Q37, Q38, Q39, Q40, Q41, Q42, Q43, Q44, Q45, Q46, Q47, Q48, Q49, Q50, Q51, Q52, Q53, Q54, Q55, Q56, Q57, Q58, Q59, Q60, Q61, Q62, Q63, Q64, Q65, Q66, Q67, Q68, Q69, Q70, Q71, Q72, Q73, Q74, Q75, Q76, Q77, Q78, Q79, Q80, Q81, Q82, Q83, Q84, Q85, Q86, Q87]), "depth" : 9.71 * mm});
        }
        {
            var Q0;
            Q0=makeQuery(id+"F0.imprint","IMPRINT",FACE,{"disambiguationData":[TD([[makeQuery(id+"F0.imprint","IMPRINT",EDGE,{"derivedFrom":sQuery(id+"F0.wireOp",EDGE,"E1")}),-1.0]])]});
            extrude(context, id + "F2", {"entities" : qUnion([Q0]), "depth" : 8 * mm});
        }
        {
            var Q0;
            Q0=makeQuery(id+"F0.imprint","IMPRINT",FACE,{"disambiguationData":[TD([[makeQuery(id+"F0.imprint","IMPRINT",EDGE,{"derivedFrom":sQuery(id+"F0.wireOp",EDGE,"E2")}),1.0]])]});
            var Q1;
            Q1=makeQuery(id+"F0.imprint","IMPRINT",FACE,{"disambiguationData":[TD([[makeQuery(id+"F0.imprint","IMPRINT",EDGE,{"derivedFrom":sQuery(id+"F0.wireOp",EDGE,"E3")}),-1.0]])]});
            extrude(context, id + "F3", {"entities" : qUnion([Q0, Q1]), "operationType" : NewBodyOperationType.ADD, "oppositeDirection" : true, "depth" : 5 * mm});
        }
        {
            var Q0;
            Q0=makeQuery(id+"F3.opExtrude","CAP_FACE",FACE,{"disambiguationData":[OSD([sQuery(id+"F0.wireOp",EDGE,"E3"),sQuery(id+"F0.wireOp",EDGE,"E5"),sQuery(id+"F0.wireOp",EDGE,"E14"),sQuery(id+"F0.wireOp",EDGE,"E15.1.1"),sQuery(id+"F0.wireOp",EDGE,"E15.2.1"),sQuery(id+"F0.wireOp",EDGE,"E15.3.1"),sQuery(id+"F0.wireOp",EDGE,"E15.4.1"),sQuery(id+"F0.wireOp",EDGE,"E15.5.1"),sQuery(id+"F0.wireOp",EDGE,"E15.6.1"),sQuery(id+"F0.wireOp",EDGE,"E15.7.1"),sQuery(id+"F0.wireOp",EDGE,"E15.8.1"),sQuery(id+"F0.wireOp",EDGE,"E15.9.1"),sQuery(id+"F0.wireOp",EDGE,"E15.10.1"),sQuery(id+"F0.wireOp",EDGE,"E15.11.1"),sQuery(id+"F0.wireOp",EDGE,"E15.12.1"),sQuery(id+"F0.wireOp",EDGE,"E15.13.1"),sQuery(id+"F0.wireOp",EDGE,"E15.14.1"),sQuery(id+"F0.wireOp",EDGE,"E15.15.1"),sQuery(id+"F0.wireOp",EDGE,"E15.16.1"),sQuery(id+"F0.wireOp",EDGE,"E15.17.1"),sQuery(id+"F0.wireOp",EDGE,"E15.18.1"),sQuery(id+"F0.wireOp",EDGE,"E15.19.1"),sQuery(id+"F0.wireOp",EDGE,"E15.20.1"),sQuery(id+"F0.wireOp",EDGE,"E15.21.1"),sQuery(id+"F0.wireOp",EDGE,"E15.22.1"),sQuery(id+"F0.wireOp",EDGE,"E15.23.1"),sQuery(id+"F0.wireOp",EDGE,"E15.24.1"),sQuery(id+"F0.wireOp",EDGE,"E15.25.1"),sQuery(id+"F0.wireOp",EDGE,"E15.26.1"),sQuery(id+"F0.wireOp",EDGE,"E15.27.1"),sQuery(id+"F0.wireOp",EDGE,"E15.28.1"),sQuery(id+"F0.wireOp",EDGE,"E15.29.1"),sQuery(id+"F0.wireOp",EDGE,"E15.30.1"),sQuery(id+"F0.wireOp",EDGE,"E15.31.1"),sQuery(id+"F0.wireOp",EDGE,"E15.32.1"),sQuery(id+"F0.wireOp",EDGE,"E15.33.1"),sQuery(id+"F0.wireOp",EDGE,"E15.34.1"),sQuery(id+"F0.wireOp",EDGE,"E15.35.1"),sQuery(id+"F0.wireOp",EDGE,"E15.36.1"),sQuery(id+"F0.wireOp",EDGE,"E15.37.1"),sQuery(id+"F0.wireOp",EDGE,"E15.38.1"),sQuery(id+"F0.wireOp",EDGE,"E15.39.1"),sQuery(id+"F0.wireOp",EDGE,"E15.40.1"),sQuery(id+"F0.wireOp",EDGE,"E15.41.1"),sQuery(id+"F0.wireOp",EDGE,"E15.42.1")])],"isStart":false});
            var sketch = newSketch(context, id + "F4", { "sketchPlane" : qUnion([Q0])});
            skCircle(sketch, "E18", {"center": v(0, 0) * mm, "radius": 17.8 * mm});
            skSolve(sketch);
        }
        {
            var Q0;
            Q0=makeQuery(id+"F4.imprint","IMPRINT",FACE,{"disambiguationData":[TD([[makeQuery(id+"F4.imprint","IMPRINT",EDGE,{"derivedFrom":sQuery(id+"F4.wireOp",EDGE,"E18")}),1.0]])]});
            var Q1;
            Q1=makeQuery(id+"F1.opExtrude","SWEPT_BODY",BODY,{"disambiguationData":[OSD([sQuery(id+"F0.wireOp",EDGE,"E3"),sQuery(id+"F0.wireOp",EDGE,"E5"),sQuery(id+"F0.wireOp",EDGE,"E7"),sQuery(id+"F0.wireOp",EDGE,"E9"),sQuery(id+"F0.wireOp",EDGE,"E10"),sQuery(id+"F0.wireOp",EDGE,"E15.1.0"),sQuery(id+"F0.wireOp",EDGE,"E15.1.2"),sQuery(id+"F0.wireOp",EDGE,"E15.1.3"),sQuery(id+"F0.wireOp",EDGE,"E15.2.0"),sQuery(id+"F0.wireOp",EDGE,"E15.2.2"),sQuery(id+"F0.wireOp",EDGE,"E15.2.3"),sQuery(id+"F0.wireOp",EDGE,"E15.3.0"),sQuery(id+"F0.wireOp",EDGE,"E15.3.2"),sQuery(id+"F0.wireOp",EDGE,"E15.3.3"),sQuery(id+"F0.wireOp",EDGE,"E15.4.0"),sQuery(id+"F0.wireOp",EDGE,"E15.4.2"),sQuery(id+"F0.wireOp",EDGE,"E15.4.3"),sQuery(id+"F0.wireOp",EDGE,"E15.5.0"),sQuery(id+"F0.wireOp",EDGE,"E15.5.2"),sQuery(id+"F0.wireOp",EDGE,"E15.5.3"),sQuery(id+"F0.wireOp",EDGE,"E15.6.0"),sQuery(id+"F0.wireOp",EDGE,"E15.6.2"),sQuery(id+"F0.wireOp",EDGE,"E15.6.3"),sQuery(id+"F0.wireOp",EDGE,"E15.7.0"),sQuery(id+"F0.wireOp",EDGE,"E15.7.2"),sQuery(id+"F0.wireOp",EDGE,"E15.7.3"),sQuery(id+"F0.wireOp",EDGE,"E15.8.0"),sQuery(id+"F0.wireOp",EDGE,"E15.8.2"),sQuery(id+"F0.wireOp",EDGE,"E15.8.3"),sQuery(id+"F0.wireOp",EDGE,"E15.9.0"),sQuery(id+"F0.wireOp",EDGE,"E15.9.2"),sQuery(id+"F0.wireOp",EDGE,"E15.9.3"),sQuery(id+"F0.wireOp",EDGE,"E15.10.0"),sQuery(id+"F0.wireOp",EDGE,"E15.10.2"),sQuery(id+"F0.wireOp",EDGE,"E15.10.3"),sQuery(id+"F0.wireOp",EDGE,"E15.11.0"),sQuery(id+"F0.wireOp",EDGE,"E15.11.2"),sQuery(id+"F0.wireOp",EDGE,"E15.11.3"),sQuery(id+"F0.wireOp",EDGE,"E15.12.0"),sQuery(id+"F0.wireOp",EDGE,"E15.12.2"),sQuery(id+"F0.wireOp",EDGE,"E15.12.3"),sQuery(id+"F0.wireOp",EDGE,"E15.13.0"),sQuery(id+"F0.wireOp",EDGE,"E15.13.2"),sQuery(id+"F0.wireOp",EDGE,"E15.13.3"),sQuery(id+"F0.wireOp",EDGE,"E15.14.0"),sQuery(id+"F0.wireOp",EDGE,"E15.14.2"),sQuery(id+"F0.wireOp",EDGE,"E15.14.3"),sQuery(id+"F0.wireOp",EDGE,"E15.15.0"),sQuery(id+"F0.wireOp",EDGE,"E15.15.2"),sQuery(id+"F0.wireOp",EDGE,"E15.15.3"),sQuery(id+"F0.wireOp",EDGE,"E15.16.0"),sQuery(id+"F0.wireOp",EDGE,"E15.16.2"),sQuery(id+"F0.wireOp",EDGE,"E15.16.3"),sQuery(id+"F0.wireOp",EDGE,"E15.17.0"),sQuery(id+"F0.wireOp",EDGE,"E15.17.2"),sQuery(id+"F0.wireOp",EDGE,"E15.17.3"),sQuery(id+"F0.wireOp",EDGE,"E15.18.0"),sQuery(id+"F0.wireOp",EDGE,"E15.18.2"),sQuery(id+"F0.wireOp",EDGE,"E15.18.3"),sQuery(id+"F0.wireOp",EDGE,"E15.19.0"),sQuery(id+"F0.wireOp",EDGE,"E15.19.2"),sQuery(id+"F0.wireOp",EDGE,"E15.19.3"),sQuery(id+"F0.wireOp",EDGE,"E15.20.0"),sQuery(id+"F0.wireOp",EDGE,"E15.20.2"),sQuery(id+"F0.wireOp",EDGE,"E15.20.3"),sQuery(id+"F0.wireOp",EDGE,"E15.21.0"),sQuery(id+"F0.wireOp",EDGE,"E15.21.2"),sQuery(id+"F0.wireOp",EDGE,"E15.21.3"),sQuery(id+"F0.wireOp",EDGE,"E15.22.0"),sQuery(id+"F0.wireOp",EDGE,"E15.22.2"),sQuery(id+"F0.wireOp",EDGE,"E15.22.3"),sQuery(id+"F0.wireOp",EDGE,"E15.23.0"),sQuery(id+"F0.wireOp",EDGE,"E15.23.2"),sQuery(id+"F0.wireOp",EDGE,"E15.23.3"),sQuery(id+"F0.wireOp",EDGE,"E15.24.0"),sQuery(id+"F0.wireOp",EDGE,"E15.24.2"),sQuery(id+"F0.wireOp",EDGE,"E15.24.3"),sQuery(id+"F0.wireOp",EDGE,"E15.25.0"),sQuery(id+"F0.wireOp",EDGE,"E15.25.2"),sQuery(id+"F0.wireOp",EDGE,"E15.25.3"),sQuery(id+"F0.wireOp",EDGE,"E15.26.0"),sQuery(id+"F0.wireOp",EDGE,"E15.26.2"),sQuery(id+"F0.wireOp",EDGE,"E15.26.3"),sQuery(id+"F0.wireOp",EDGE,"E15.27.0"),sQuery(id+"F0.wireOp",EDGE,"E15.27.2"),sQuery(id+"F0.wireOp",EDGE,"E15.27.3"),sQuery(id+"F0.wireOp",EDGE,"E15.28.0"),sQuery(id+"F0.wireOp",EDGE,"E15.28.2"),sQuery(id+"F0.wireOp",EDGE,"E15.28.3"),sQuery(id+"F0.wireOp",EDGE,"E15.29.0"),sQuery(id+"F0.wireOp",EDGE,"E15.29.2"),sQuery(id+"F0.wireOp",EDGE,"E15.29.3"),sQuery(id+"F0.wireOp",EDGE,"E15.30.0"),sQuery(id+"F0.wireOp",EDGE,"E15.30.2"),sQuery(id+"F0.wireOp",EDGE,"E15.30.3"),sQuery(id+"F0.wireOp",EDGE,"E15.31.0"),sQuery(id+"F0.wireOp",EDGE,"E15.31.2"),sQuery(id+"F0.wireOp",EDGE,"E15.31.3"),sQuery(id+"F0.wireOp",EDGE,"E15.32.0"),sQuery(id+"F0.wireOp",EDGE,"E15.32.2"),sQuery(id+"F0.wireOp",EDGE,"E15.32.3"),sQuery(id+"F0.wireOp",EDGE,"E15.33.0"),sQuery(id+"F0.wireOp",EDGE,"E15.33.2"),sQuery(id+"F0.wireOp",EDGE,"E15.33.3"),sQuery(id+"F0.wireOp",EDGE,"E15.34.0"),sQuery(id+"F0.wireOp",EDGE,"E15.34.2"),sQuery(id+"F0.wireOp",EDGE,"E15.34.3"),sQuery(id+"F0.wireOp",EDGE,"E15.35.0"),sQuery(id+"F0.wireOp",EDGE,"E15.35.2"),sQuery(id+"F0.wireOp",EDGE,"E15.35.3"),sQuery(id+"F0.wireOp",EDGE,"E15.36.0"),sQuery(id+"F0.wireOp",EDGE,"E15.36.2"),sQuery(id+"F0.wireOp",EDGE,"E15.36.3"),sQuery(id+"F0.wireOp",EDGE,"E15.37.0"),sQuery(id+"F0.wireOp",EDGE,"E15.37.2"),sQuery(id+"F0.wireOp",EDGE,"E15.37.3"),sQuery(id+"F0.wireOp",EDGE,"E15.38.0"),sQuery(id+"F0.wireOp",EDGE,"E15.38.2"),sQuery(id+"F0.wireOp",EDGE,"E15.38.3"),sQuery(id+"F0.wireOp",EDGE,"E15.39.0"),sQuery(id+"F0.wireOp",EDGE,"E15.39.2"),sQuery(id+"F0.wireOp",EDGE,"E15.39.3"),sQuery(id+"F0.wireOp",EDGE,"E15.40.0"),sQuery(id+"F0.wireOp",EDGE,"E15.40.2"),sQuery(id+"F0.wireOp",EDGE,"E15.40.3"),sQuery(id+"F0.wireOp",EDGE,"E15.41.0"),sQuery(id+"F0.wireOp",EDGE,"E15.41.2"),sQuery(id+"F0.wireOp",EDGE,"E15.41.3"),sQuery(id+"F0.wireOp",EDGE,"E15.42.0"),sQuery(id+"F0.wireOp",EDGE,"E15.42.2"),sQuery(id+"F0.wireOp",EDGE,"E15.42.3"),sQuery(id+"F0.wireOp",EDGE,"E16"),sQuery(id+"F0.wireOp",EDGE,"E17.1.0"),sQuery(id+"F0.wireOp",EDGE,"E17.2.0"),sQuery(id+"F0.wireOp",EDGE,"E17.3.0"),sQuery(id+"F0.wireOp",EDGE,"E17.4.0"),sQuery(id+"F0.wireOp",EDGE,"E17.5.0"),sQuery(id+"F0.wireOp",EDGE,"E17.6.0"),sQuery(id+"F0.wireOp",EDGE,"E17.7.0"),sQuery(id+"F0.wireOp",EDGE,"E17.8.0"),sQuery(id+"F0.wireOp",EDGE,"E17.9.0"),sQuery(id+"F0.wireOp",EDGE,"E17.10.0"),sQuery(id+"F0.wireOp",EDGE,"E17.11.0"),sQuery(id+"F0.wireOp",EDGE,"E17.12.0"),sQuery(id+"F0.wireOp",EDGE,"E17.13.0"),sQuery(id+"F0.wireOp",EDGE,"E17.14.0"),sQuery(id+"F0.wireOp",EDGE,"E17.15.0"),sQuery(id+"F0.wireOp",EDGE,"E17.16.0"),sQuery(id+"F0.wireOp",EDGE,"E17.17.0"),sQuery(id+"F0.wireOp",EDGE,"E17.18.0"),sQuery(id+"F0.wireOp",EDGE,"E17.19.0"),sQuery(id+"F0.wireOp",EDGE,"E17.20.0"),sQuery(id+"F0.wireOp",EDGE,"E17.21.0"),sQuery(id+"F0.wireOp",EDGE,"E17.22.0"),sQuery(id+"F0.wireOp",EDGE,"E17.23.0"),sQuery(id+"F0.wireOp",EDGE,"E17.24.0"),sQuery(id+"F0.wireOp",EDGE,"E17.25.0"),sQuery(id+"F0.wireOp",EDGE,"E17.26.0"),sQuery(id+"F0.wireOp",EDGE,"E17.27.0"),sQuery(id+"F0.wireOp",EDGE,"E17.28.0"),sQuery(id+"F0.wireOp",EDGE,"E17.29.0"),sQuery(id+"F0.wireOp",EDGE,"E17.30.0"),sQuery(id+"F0.wireOp",EDGE,"E17.31.0"),sQuery(id+"F0.wireOp",EDGE,"E17.32.0"),sQuery(id+"F0.wireOp",EDGE,"E17.33.0"),sQuery(id+"F0.wireOp",EDGE,"E17.34.0"),sQuery(id+"F0.wireOp",EDGE,"E17.35.0"),sQuery(id+"F0.wireOp",EDGE,"E17.36.0"),sQuery(id+"F0.wireOp",EDGE,"E17.37.0"),sQuery(id+"F0.wireOp",EDGE,"E17.38.0"),sQuery(id+"F0.wireOp",EDGE,"E17.39.0"),sQuery(id+"F0.wireOp",EDGE,"E17.40.0"),sQuery(id+"F0.wireOp",EDGE,"E17.41.0"),sQuery(id+"F0.wireOp",EDGE,"E17.42.0")])]});
            extrude(context, id + "F5", {"entities" : qUnion([Q0]), "operationType" : NewBodyOperationType.REMOVE, "endBound" : BoundingType.UP_TO_BODY, "oppositeDirection" : true, "endBoundEntityBody" : qUnion([Q1]), "depth" : 25 * mm});
        }
        {
            var Q0;
            Q0=makeQuery(id+"F1.opExtrude","CAP_FACE",FACE,{"disambiguationData":[OSD([sQuery(id+"F0.wireOp",EDGE,"E3"),sQuery(id+"F0.wireOp",EDGE,"E5"),sQuery(id+"F0.wireOp",EDGE,"E7"),sQuery(id+"F0.wireOp",EDGE,"E9"),sQuery(id+"F0.wireOp",EDGE,"E10"),sQuery(id+"F0.wireOp",EDGE,"E15.1.0"),sQuery(id+"F0.wireOp",EDGE,"E15.1.2"),sQuery(id+"F0.wireOp",EDGE,"E15.1.3"),sQuery(id+"F0.wireOp",EDGE,"E15.2.0"),sQuery(id+"F0.wireOp",EDGE,"E15.2.2"),sQuery(id+"F0.wireOp",EDGE,"E15.2.3"),sQuery(id+"F0.wireOp",EDGE,"E15.3.0"),sQuery(id+"F0.wireOp",EDGE,"E15.3.2"),sQuery(id+"F0.wireOp",EDGE,"E15.3.3"),sQuery(id+"F0.wireOp",EDGE,"E15.4.0"),sQuery(id+"F0.wireOp",EDGE,"E15.4.2"),sQuery(id+"F0.wireOp",EDGE,"E15.4.3"),sQuery(id+"F0.wireOp",EDGE,"E15.5.0"),sQuery(id+"F0.wireOp",EDGE,"E15.5.2"),sQuery(id+"F0.wireOp",EDGE,"E15.5.3"),sQuery(id+"F0.wireOp",EDGE,"E15.6.0"),sQuery(id+"F0.wireOp",EDGE,"E15.6.2"),sQuery(id+"F0.wireOp",EDGE,"E15.6.3"),sQuery(id+"F0.wireOp",EDGE,"E15.7.0"),sQuery(id+"F0.wireOp",EDGE,"E15.7.2"),sQuery(id+"F0.wireOp",EDGE,"E15.7.3"),sQuery(id+"F0.wireOp",EDGE,"E15.8.0"),sQuery(id+"F0.wireOp",EDGE,"E15.8.2"),sQuery(id+"F0.wireOp",EDGE,"E15.8.3"),sQuery(id+"F0.wireOp",EDGE,"E15.9.0"),sQuery(id+"F0.wireOp",EDGE,"E15.9.2"),sQuery(id+"F0.wireOp",EDGE,"E15.9.3"),sQuery(id+"F0.wireOp",EDGE,"E15.10.0"),sQuery(id+"F0.wireOp",EDGE,"E15.10.2"),sQuery(id+"F0.wireOp",EDGE,"E15.10.3"),sQuery(id+"F0.wireOp",EDGE,"E15.11.0"),sQuery(id+"F0.wireOp",EDGE,"E15.11.2"),sQuery(id+"F0.wireOp",EDGE,"E15.11.3"),sQuery(id+"F0.wireOp",EDGE,"E15.12.0"),sQuery(id+"F0.wireOp",EDGE,"E15.12.2"),sQuery(id+"F0.wireOp",EDGE,"E15.12.3"),sQuery(id+"F0.wireOp",EDGE,"E15.13.0"),sQuery(id+"F0.wireOp",EDGE,"E15.13.2"),sQuery(id+"F0.wireOp",EDGE,"E15.13.3"),sQuery(id+"F0.wireOp",EDGE,"E15.14.0"),sQuery(id+"F0.wireOp",EDGE,"E15.14.2"),sQuery(id+"F0.wireOp",EDGE,"E15.14.3"),sQuery(id+"F0.wireOp",EDGE,"E15.15.0"),sQuery(id+"F0.wireOp",EDGE,"E15.15.2"),sQuery(id+"F0.wireOp",EDGE,"E15.15.3"),sQuery(id+"F0.wireOp",EDGE,"E15.16.0"),sQuery(id+"F0.wireOp",EDGE,"E15.16.2"),sQuery(id+"F0.wireOp",EDGE,"E15.16.3"),sQuery(id+"F0.wireOp",EDGE,"E15.17.0"),sQuery(id+"F0.wireOp",EDGE,"E15.17.2"),sQuery(id+"F0.wireOp",EDGE,"E15.17.3"),sQuery(id+"F0.wireOp",EDGE,"E15.18.0"),sQuery(id+"F0.wireOp",EDGE,"E15.18.2"),sQuery(id+"F0.wireOp",EDGE,"E15.18.3"),sQuery(id+"F0.wireOp",EDGE,"E15.19.0"),sQuery(id+"F0.wireOp",EDGE,"E15.19.2"),sQuery(id+"F0.wireOp",EDGE,"E15.19.3"),sQuery(id+"F0.wireOp",EDGE,"E15.20.0"),sQuery(id+"F0.wireOp",EDGE,"E15.20.2"),sQuery(id+"F0.wireOp",EDGE,"E15.20.3"),sQuery(id+"F0.wireOp",EDGE,"E15.21.0"),sQuery(id+"F0.wireOp",EDGE,"E15.21.2"),sQuery(id+"F0.wireOp",EDGE,"E15.21.3"),sQuery(id+"F0.wireOp",EDGE,"E15.22.0"),sQuery(id+"F0.wireOp",EDGE,"E15.22.2"),sQuery(id+"F0.wireOp",EDGE,"E15.22.3"),sQuery(id+"F0.wireOp",EDGE,"E15.23.0"),sQuery(id+"F0.wireOp",EDGE,"E15.23.2"),sQuery(id+"F0.wireOp",EDGE,"E15.23.3"),sQuery(id+"F0.wireOp",EDGE,"E15.24.0"),sQuery(id+"F0.wireOp",EDGE,"E15.24.2"),sQuery(id+"F0.wireOp",EDGE,"E15.24.3"),sQuery(id+"F0.wireOp",EDGE,"E15.25.0"),sQuery(id+"F0.wireOp",EDGE,"E15.25.2"),sQuery(id+"F0.wireOp",EDGE,"E15.25.3"),sQuery(id+"F0.wireOp",EDGE,"E15.26.0"),sQuery(id+"F0.wireOp",EDGE,"E15.26.2"),sQuery(id+"F0.wireOp",EDGE,"E15.26.3"),sQuery(id+"F0.wireOp",EDGE,"E15.27.0"),sQuery(id+"F0.wireOp",EDGE,"E15.27.2"),sQuery(id+"F0.wireOp",EDGE,"E15.27.3"),sQuery(id+"F0.wireOp",EDGE,"E15.28.0"),sQuery(id+"F0.wireOp",EDGE,"E15.28.2"),sQuery(id+"F0.wireOp",EDGE,"E15.28.3"),sQuery(id+"F0.wireOp",EDGE,"E15.29.0"),sQuery(id+"F0.wireOp",EDGE,"E15.29.2"),sQuery(id+"F0.wireOp",EDGE,"E15.29.3"),sQuery(id+"F0.wireOp",EDGE,"E15.30.0"),sQuery(id+"F0.wireOp",EDGE,"E15.30.2"),sQuery(id+"F0.wireOp",EDGE,"E15.30.3"),sQuery(id+"F0.wireOp",EDGE,"E15.31.0"),sQuery(id+"F0.wireOp",EDGE,"E15.31.2"),sQuery(id+"F0.wireOp",EDGE,"E15.31.3"),sQuery(id+"F0.wireOp",EDGE,"E15.32.0"),sQuery(id+"F0.wireOp",EDGE,"E15.32.2"),sQuery(id+"F0.wireOp",EDGE,"E15.32.3"),sQuery(id+"F0.wireOp",EDGE,"E15.33.0"),sQuery(id+"F0.wireOp",EDGE,"E15.33.2"),sQuery(id+"F0.wireOp",EDGE,"E15.33.3"),sQuery(id+"F0.wireOp",EDGE,"E15.34.0"),sQuery(id+"F0.wireOp",EDGE,"E15.34.2"),sQuery(id+"F0.wireOp",EDGE,"E15.34.3"),sQuery(id+"F0.wireOp",EDGE,"E15.35.0"),sQuery(id+"F0.wireOp",EDGE,"E15.35.2"),sQuery(id+"F0.wireOp",EDGE,"E15.35.3"),sQuery(id+"F0.wireOp",EDGE,"E15.36.0"),sQuery(id+"F0.wireOp",EDGE,"E15.36.2"),sQuery(id+"F0.wireOp",EDGE,"E15.36.3"),sQuery(id+"F0.wireOp",EDGE,"E15.37.0"),sQuery(id+"F0.wireOp",EDGE,"E15.37.2"),sQuery(id+"F0.wireOp",EDGE,"E15.37.3"),sQuery(id+"F0.wireOp",EDGE,"E15.38.0"),sQuery(id+"F0.wireOp",EDGE,"E15.38.2"),sQuery(id+"F0.wireOp",EDGE,"E15.38.3"),sQuery(id+"F0.wireOp",EDGE,"E15.39.0"),sQuery(id+"F0.wireOp",EDGE,"E15.39.2"),sQuery(id+"F0.wireOp",EDGE,"E15.39.3"),sQuery(id+"F0.wireOp",EDGE,"E15.40.0"),sQuery(id+"F0.wireOp",EDGE,"E15.40.2"),sQuery(id+"F0.wireOp",EDGE,"E15.40.3"),sQuery(id+"F0.wireOp",EDGE,"E15.41.0"),sQuery(id+"F0.wireOp",EDGE,"E15.41.2"),sQuery(id+"F0.wireOp",EDGE,"E15.41.3"),sQuery(id+"F0.wireOp",EDGE,"E15.42.0"),sQuery(id+"F0.wireOp",EDGE,"E15.42.2"),sQuery(id+"F0.wireOp",EDGE,"E15.42.3"),sQuery(id+"F0.wireOp",EDGE,"E16"),sQuery(id+"F0.wireOp",EDGE,"E17.1.0"),sQuery(id+"F0.wireOp",EDGE,"E17.2.0"),sQuery(id+"F0.wireOp",EDGE,"E17.3.0"),sQuery(id+"F0.wireOp",EDGE,"E17.4.0"),sQuery(id+"F0.wireOp",EDGE,"E17.5.0"),sQuery(id+"F0.wireOp",EDGE,"E17.6.0"),sQuery(id+"F0.wireOp",EDGE,"E17.7.0"),sQuery(id+"F0.wireOp",EDGE,"E17.8.0"),sQuery(id+"F0.wireOp",EDGE,"E17.9.0"),sQuery(id+"F0.wireOp",EDGE,"E17.10.0"),sQuery(id+"F0.wireOp",EDGE,"E17.11.0"),sQuery(id+"F0.wireOp",EDGE,"E17.12.0"),sQuery(id+"F0.wireOp",EDGE,"E17.13.0"),sQuery(id+"F0.wireOp",EDGE,"E17.14.0"),sQuery(id+"F0.wireOp",EDGE,"E17.15.0"),sQuery(id+"F0.wireOp",EDGE,"E17.16.0"),sQuery(id+"F0.wireOp",EDGE,"E17.17.0"),sQuery(id+"F0.wireOp",EDGE,"E17.18.0"),sQuery(id+"F0.wireOp",EDGE,"E17.19.0"),sQuery(id+"F0.wireOp",EDGE,"E17.20.0"),sQuery(id+"F0.wireOp",EDGE,"E17.21.0"),sQuery(id+"F0.wireOp",EDGE,"E17.22.0"),sQuery(id+"F0.wireOp",EDGE,"E17.23.0"),sQuery(id+"F0.wireOp",EDGE,"E17.24.0"),sQuery(id+"F0.wireOp",EDGE,"E17.25.0"),sQuery(id+"F0.wireOp",EDGE,"E17.26.0"),sQuery(id+"F0.wireOp",EDGE,"E17.27.0"),sQuery(id+"F0.wireOp",EDGE,"E17.28.0"),sQuery(id+"F0.wireOp",EDGE,"E17.29.0"),sQuery(id+"F0.wireOp",EDGE,"E17.30.0"),sQuery(id+"F0.wireOp",EDGE,"E17.31.0"),sQuery(id+"F0.wireOp",EDGE,"E17.32.0"),sQuery(id+"F0.wireOp",EDGE,"E17.33.0"),sQuery(id+"F0.wireOp",EDGE,"E17.34.0"),sQuery(id+"F0.wireOp",EDGE,"E17.35.0"),sQuery(id+"F0.wireOp",EDGE,"E17.36.0"),sQuery(id+"F0.wireOp",EDGE,"E17.37.0"),sQuery(id+"F0.wireOp",EDGE,"E17.38.0"),sQuery(id+"F0.wireOp",EDGE,"E17.39.0"),sQuery(id+"F0.wireOp",EDGE,"E17.40.0"),sQuery(id+"F0.wireOp",EDGE,"E17.41.0"),sQuery(id+"F0.wireOp",EDGE,"E17.42.0")])],"isStart":false});
            var sketch = newSketch(context, id + "F6", { "sketchPlane" : qUnion([Q0])});
            skCircle(sketch, "E19.0", {"center": v(0, 0) * mm, "radius": 17.8 * mm});
            skCircle(sketch, "E20", {"center": v(0, 0) * mm, "radius": 25 * mm});
            skCircle(sketch, "E21", {"center": v(0, 0) * mm, "radius": 23.86 * mm});
            skCircle(sketch, "E22", {"center": v(0, 0) * mm, "radius": 23.62 * mm});
            skLineSegment(sketch, "E23", {"start": v(-0.88, 23.62) * mm, "end": v(0.87, 23.62) * mm});
            skLineSegment(sketch, "E24", {"start": v(0, 18.78) * mm, "end": v(0, 27.09) * mm, "construction": true});
            skLineSegment(sketch, "E25", {"start": v(-0.4, 22.88) * mm, "end": v(0.4, 22.88) * mm});
            skLineSegment(sketch, "E26", {"start": v(-0.87, 23.62) * mm, "end": v(-0.58, 23) * mm});
            skLineSegment(sketch, "E27", {"start": v(0.87, 23.62) * mm, "end": v(0.58, 23) * mm});
            skArc(sketch, "E28.filletArc", {"start": v(0.4, 22.88) * mm, "mid": v(0.5, 22.9) * mm, "end": v(0.58, 23) * mm});
            skArc(sketch, "E29.filletArc", {"start": v(-0.58, 23) * mm, "mid": v(-0.5, 22.9) * mm, "end": v(-0.4, 22.88) * mm});
            skLineSegment(sketch, "E30.1.0", {"start": v(-1.6, 23.59) * mm, "end": v(-1.83, 22.93) * mm});
            skLineSegment(sketch, "E30.1.1", {"start": v(-3.34, 23.4) * mm, "end": v(-1.6, 23.59) * mm});
            skLineSegment(sketch, "E30.1.2", {"start": v(-2.79, 22.7) * mm, "end": v(-2, 22.8) * mm});
            skLineSegment(sketch, "E30.1.3", {"start": v(-3.34, 23.4) * mm, "end": v(-2.98, 22.8) * mm});
            skArc(sketch, "E30.1.4", {"start": v(-2, 22.8) * mm, "mid": v(-1.9, 22.83) * mm, "end": v(-1.83, 22.93) * mm});
            skArc(sketch, "E30.1.5", {"start": v(-2.98, 22.8) * mm, "mid": v(-2.9, 22.73) * mm, "end": v(-2.79, 22.7) * mm});
            skLineSegment(sketch, "E30.2.0", {"start": v(-4.06, 23.3) * mm, "end": v(-4.21, 22.6) * mm});
            skLineSegment(sketch, "E30.2.1", {"start": v(-5.77, 22.93) * mm, "end": v(-4.06, 23.3) * mm});
            skLineSegment(sketch, "E30.2.2", {"start": v(-5.15, 22.3) * mm, "end": v(-4.37, 22.46) * mm});
            skLineSegment(sketch, "E30.2.3", {"start": v(-5.77, 22.93) * mm, "end": v(-5.35, 22.37) * mm});
            skArc(sketch, "E30.2.4", {"start": v(-4.37, 22.46) * mm, "mid": v(-4.27, 22.51) * mm, "end": v(-4.21, 22.6) * mm});
            skArc(sketch, "E30.2.5", {"start": v(-5.35, 22.37) * mm, "mid": v(-5.26, 22.3) * mm, "end": v(-5.15, 22.3) * mm});
            skLineSegment(sketch, "E30.3.0", {"start": v(-6.47, 22.74) * mm, "end": v(-6.55, 22.04) * mm});
            skLineSegment(sketch, "E30.3.1", {"start": v(-8.13, 22.2) * mm, "end": v(-6.47, 22.74) * mm});
            skLineSegment(sketch, "E30.3.2", {"start": v(-7.45, 21.63) * mm, "end": v(-6.7, 21.88) * mm});
            skLineSegment(sketch, "E30.3.3", {"start": v(-8.13, 22.2) * mm, "end": v(-7.66, 21.69) * mm});
            skArc(sketch, "E30.3.4", {"start": v(-6.7, 21.88) * mm, "mid": v(-6.6, 21.94) * mm, "end": v(-6.55, 22.04) * mm});
            skArc(sketch, "E30.3.5", {"start": v(-7.66, 21.69) * mm, "mid": v(-7.56, 21.63) * mm, "end": v(-7.45, 21.63) * mm});
            skLineSegment(sketch, "E30.4.0", {"start": v(-8.8, 21.94) * mm, "end": v(-8.82, 21.24) * mm});
            skLineSegment(sketch, "E30.4.1", {"start": v(-10.4, 21.23) * mm, "end": v(-8.8, 21.94) * mm});
            skLineSegment(sketch, "E30.4.2", {"start": v(-9.67, 20.74) * mm, "end": v(-8.94, 21.06) * mm});
            skLineSegment(sketch, "E30.4.3", {"start": v(-10.4, 21.23) * mm, "end": v(-9.88, 20.77) * mm});
            skArc(sketch, "E30.4.4", {"start": v(-8.94, 21.06) * mm, "mid": v(-8.86, 21.13) * mm, "end": v(-8.82, 21.24) * mm});
            skArc(sketch, "E30.4.5", {"start": v(-9.88, 20.77) * mm, "mid": v(-9.78, 20.72) * mm, "end": v(-9.67, 20.74) * mm});
            skLineSegment(sketch, "E30.5.0", {"start": v(-11.05, 20.9) * mm, "end": v(-11, 20.2) * mm});
            skLineSegment(sketch, "E30.5.1", {"start": v(-12.57, 20.02) * mm, "end": v(-11.05, 20.9) * mm});
            skLineSegment(sketch, "E30.5.2", {"start": v(-11.78, 19.61) * mm, "end": v(-11.1, 20) * mm});
            skLineSegment(sketch, "E30.5.3", {"start": v(-12.57, 20.02) * mm, "end": v(-12, 19.62) * mm});
            skArc(sketch, "E30.5.4", {"start": v(-11.1, 20) * mm, "mid": v(-11.02, 20.1) * mm, "end": v(-11, 20.2) * mm});
            skArc(sketch, "E30.5.5", {"start": v(-12, 19.62) * mm, "mid": v(-11.9, 19.58) * mm, "end": v(-11.78, 19.61) * mm});
            skLineSegment(sketch, "E30.6.0", {"start": v(-13.18, 19.63) * mm, "end": v(-13.04, 18.94) * mm});
            skLineSegment(sketch, "E30.6.1", {"start": v(-14.6, 18.6) * mm, "end": v(-13.18, 19.63) * mm});
            skLineSegment(sketch, "E30.6.2", {"start": v(-13.77, 18.27) * mm, "end": v(-13.12, 18.74) * mm});
            skLineSegment(sketch, "E30.6.3", {"start": v(-14.6, 18.6) * mm, "end": v(-13.98, 18.26) * mm});
            skArc(sketch, "E30.6.4", {"start": v(-13.12, 18.74) * mm, "mid": v(-13.06, 18.83) * mm, "end": v(-13.04, 18.94) * mm});
            skArc(sketch, "E30.6.5", {"start": v(-13.98, 18.26) * mm, "mid": v(-13.87, 18.23) * mm, "end": v(-13.77, 18.27) * mm});
            skLineSegment(sketch, "E30.7.0", {"start": v(-15.16, 18.14) * mm, "end": v(-14.95, 17.47) * mm});
            skLineSegment(sketch, "E30.7.1", {"start": v(-16.46, 16.97) * mm, "end": v(-15.16, 18.14) * mm});
            skLineSegment(sketch, "E30.7.2", {"start": v(-15.6, 16.73) * mm, "end": v(-15.01, 17.27) * mm});
            skLineSegment(sketch, "E30.7.3", {"start": v(-16.46, 16.97) * mm, "end": v(-15.81, 16.7) * mm});
            skArc(sketch, "E30.7.4", {"start": v(-15.01, 17.27) * mm, "mid": v(-14.95, 17.36) * mm, "end": v(-14.95, 17.47) * mm});
            skArc(sketch, "E30.7.5", {"start": v(-15.81, 16.7) * mm, "mid": v(-15.7, 16.68) * mm, "end": v(-15.6, 16.73) * mm});
            skLineSegment(sketch, "E30.8.0", {"start": v(-16.97, 16.46) * mm, "end": v(-16.7, 15.81) * mm});
            skLineSegment(sketch, "E30.8.1", {"start": v(-18.14, 15.16) * mm, "end": v(-16.97, 16.46) * mm});
            skLineSegment(sketch, "E30.8.2", {"start": v(-17.27, 15.01) * mm, "end": v(-16.73, 15.6) * mm});
            skLineSegment(sketch, "E30.8.3", {"start": v(-18.14, 15.16) * mm, "end": v(-17.47, 14.95) * mm});
            skArc(sketch, "E30.8.4", {"start": v(-16.73, 15.6) * mm, "mid": v(-16.68, 15.7) * mm, "end": v(-16.7, 15.81) * mm});
            skArc(sketch, "E30.8.5", {"start": v(-17.47, 14.95) * mm, "mid": v(-17.36, 14.95) * mm, "end": v(-17.27, 15.01) * mm});
            skLineSegment(sketch, "E30.9.0", {"start": v(-18.6, 14.6) * mm, "end": v(-18.26, 13.98) * mm});
            skLineSegment(sketch, "E30.9.1", {"start": v(-19.63, 13.18) * mm, "end": v(-18.6, 14.6) * mm});
            skLineSegment(sketch, "E30.9.2", {"start": v(-18.74, 13.12) * mm, "end": v(-18.27, 13.77) * mm});
            skLineSegment(sketch, "E30.9.3", {"start": v(-19.63, 13.18) * mm, "end": v(-18.94, 13.04) * mm});
            skArc(sketch, "E30.9.4", {"start": v(-18.27, 13.77) * mm, "mid": v(-18.23, 13.87) * mm, "end": v(-18.26, 13.98) * mm});
            skArc(sketch, "E30.9.5", {"start": v(-18.94, 13.04) * mm, "mid": v(-18.83, 13.06) * mm, "end": v(-18.74, 13.12) * mm});
            skLineSegment(sketch, "E30.10.0", {"start": v(-20.02, 12.57) * mm, "end": v(-19.62, 12) * mm});
            skLineSegment(sketch, "E30.10.1", {"start": v(-20.9, 11.05) * mm, "end": v(-20.02, 12.57) * mm});
            skLineSegment(sketch, "E30.10.2", {"start": v(-20, 11.1) * mm, "end": v(-19.61, 11.78) * mm});
            skLineSegment(sketch, "E30.10.3", {"start": v(-20.9, 11.05) * mm, "end": v(-20.2, 11) * mm});
            skArc(sketch, "E30.10.4", {"start": v(-19.61, 11.78) * mm, "mid": v(-19.58, 11.9) * mm, "end": v(-19.62, 12) * mm});
            skArc(sketch, "E30.10.5", {"start": v(-20.2, 11) * mm, "mid": v(-20.1, 11.02) * mm, "end": v(-20, 11.1) * mm});
            skLineSegment(sketch, "E30.11.0", {"start": v(-21.23, 10.4) * mm, "end": v(-20.77, 9.88) * mm});
            skLineSegment(sketch, "E30.11.1", {"start": v(-21.94, 8.8) * mm, "end": v(-21.23, 10.4) * mm});
            skLineSegment(sketch, "E30.11.2", {"start": v(-21.06, 8.94) * mm, "end": v(-20.74, 9.67) * mm});
            skLineSegment(sketch, "E30.11.3", {"start": v(-21.94, 8.8) * mm, "end": v(-21.24, 8.82) * mm});
            skArc(sketch, "E30.11.4", {"start": v(-20.74, 9.67) * mm, "mid": v(-20.72, 9.78) * mm, "end": v(-20.77, 9.88) * mm});
            skArc(sketch, "E30.11.5", {"start": v(-21.24, 8.82) * mm, "mid": v(-21.13, 8.86) * mm, "end": v(-21.06, 8.94) * mm});
            skLineSegment(sketch, "E30.12.0", {"start": v(-22.2, 8.13) * mm, "end": v(-21.69, 7.66) * mm});
            skLineSegment(sketch, "E30.12.1", {"start": v(-22.74, 6.47) * mm, "end": v(-22.2, 8.13) * mm});
            skLineSegment(sketch, "E30.12.2", {"start": v(-21.88, 6.7) * mm, "end": v(-21.63, 7.45) * mm});
            skLineSegment(sketch, "E30.12.3", {"start": v(-22.74, 6.47) * mm, "end": v(-22.04, 6.55) * mm});
            skArc(sketch, "E30.12.4", {"start": v(-21.63, 7.45) * mm, "mid": v(-21.63, 7.56) * mm, "end": v(-21.69, 7.66) * mm});
            skArc(sketch, "E30.12.5", {"start": v(-22.04, 6.55) * mm, "mid": v(-21.94, 6.6) * mm, "end": v(-21.88, 6.7) * mm});
            skLineSegment(sketch, "E30.13.0", {"start": v(-22.93, 5.77) * mm, "end": v(-22.37, 5.35) * mm});
            skLineSegment(sketch, "E30.13.1", {"start": v(-23.3, 4.06) * mm, "end": v(-22.93, 5.77) * mm});
            skLineSegment(sketch, "E30.13.2", {"start": v(-22.46, 4.37) * mm, "end": v(-22.3, 5.15) * mm});
            skLineSegment(sketch, "E30.13.3", {"start": v(-23.3, 4.06) * mm, "end": v(-22.6, 4.21) * mm});
            skArc(sketch, "E30.13.4", {"start": v(-22.3, 5.15) * mm, "mid": v(-22.3, 5.26) * mm, "end": v(-22.37, 5.35) * mm});
            skArc(sketch, "E30.13.5", {"start": v(-22.6, 4.21) * mm, "mid": v(-22.51, 4.27) * mm, "end": v(-22.46, 4.37) * mm});
            skLineSegment(sketch, "E30.14.0", {"start": v(-23.4, 3.34) * mm, "end": v(-22.8, 2.98) * mm});
            skLineSegment(sketch, "E30.14.1", {"start": v(-23.59, 1.6) * mm, "end": v(-23.4, 3.34) * mm});
            skLineSegment(sketch, "E30.14.2", {"start": v(-22.8, 2) * mm, "end": v(-22.7, 2.79) * mm});
            skLineSegment(sketch, "E30.14.3", {"start": v(-23.59, 1.6) * mm, "end": v(-22.93, 1.83) * mm});
            skArc(sketch, "E30.14.4", {"start": v(-22.7, 2.79) * mm, "mid": v(-22.73, 2.9) * mm, "end": v(-22.8, 2.98) * mm});
            skArc(sketch, "E30.14.5", {"start": v(-22.93, 1.83) * mm, "mid": v(-22.83, 1.9) * mm, "end": v(-22.8, 2) * mm});
            skLineSegment(sketch, "E30.15.0", {"start": v(-23.62, 0.88) * mm, "end": v(-23, 0.58) * mm});
            skLineSegment(sketch, "E30.15.1", {"start": v(-23.62, -0.87) * mm, "end": v(-23.62, 0.88) * mm});
            skLineSegment(sketch, "E30.15.2", {"start": v(-22.88, -0.4) * mm, "end": v(-22.88, 0.4) * mm});
            skLineSegment(sketch, "E30.15.3", {"start": v(-23.62, -0.87) * mm, "end": v(-23, -0.58) * mm});
            skArc(sketch, "E30.15.4", {"start": v(-22.88, 0.4) * mm, "mid": v(-22.9, 0.5) * mm, "end": v(-23, 0.58) * mm});
            skArc(sketch, "E30.15.5", {"start": v(-23, -0.58) * mm, "mid": v(-22.9, -0.5) * mm, "end": v(-22.88, -0.4) * mm});
            skLineSegment(sketch, "E30.16.0", {"start": v(-23.59, -1.6) * mm, "end": v(-22.93, -1.83) * mm});
            skLineSegment(sketch, "E30.16.1", {"start": v(-23.4, -3.34) * mm, "end": v(-23.59, -1.6) * mm});
            skLineSegment(sketch, "E30.16.2", {"start": v(-22.7, -2.79) * mm, "end": v(-22.8, -2) * mm});
            skLineSegment(sketch, "E30.16.3", {"start": v(-23.4, -3.34) * mm, "end": v(-22.8, -2.98) * mm});
            skArc(sketch, "E30.16.4", {"start": v(-22.8, -2) * mm, "mid": v(-22.83, -1.9) * mm, "end": v(-22.93, -1.83) * mm});
            skArc(sketch, "E30.16.5", {"start": v(-22.8, -2.98) * mm, "mid": v(-22.73, -2.9) * mm, "end": v(-22.7, -2.79) * mm});
            skLineSegment(sketch, "E30.17.0", {"start": v(-23.3, -4.06) * mm, "end": v(-22.6, -4.21) * mm});
            skLineSegment(sketch, "E30.17.1", {"start": v(-22.93, -5.77) * mm, "end": v(-23.3, -4.06) * mm});
            skLineSegment(sketch, "E30.17.2", {"start": v(-22.3, -5.15) * mm, "end": v(-22.46, -4.37) * mm});
            skLineSegment(sketch, "E30.17.3", {"start": v(-22.93, -5.77) * mm, "end": v(-22.37, -5.35) * mm});
            skArc(sketch, "E30.17.4", {"start": v(-22.46, -4.37) * mm, "mid": v(-22.51, -4.27) * mm, "end": v(-22.6, -4.21) * mm});
            skArc(sketch, "E30.17.5", {"start": v(-22.37, -5.35) * mm, "mid": v(-22.3, -5.26) * mm, "end": v(-22.3, -5.15) * mm});
            skLineSegment(sketch, "E30.18.0", {"start": v(-22.74, -6.47) * mm, "end": v(-22.04, -6.55) * mm});
            skLineSegment(sketch, "E30.18.1", {"start": v(-22.2, -8.13) * mm, "end": v(-22.74, -6.47) * mm});
            skLineSegment(sketch, "E30.18.2", {"start": v(-21.63, -7.45) * mm, "end": v(-21.88, -6.7) * mm});
            skLineSegment(sketch, "E30.18.3", {"start": v(-22.2, -8.13) * mm, "end": v(-21.69, -7.66) * mm});
            skArc(sketch, "E30.18.4", {"start": v(-21.88, -6.7) * mm, "mid": v(-21.94, -6.6) * mm, "end": v(-22.04, -6.55) * mm});
            skArc(sketch, "E30.18.5", {"start": v(-21.69, -7.66) * mm, "mid": v(-21.63, -7.56) * mm, "end": v(-21.63, -7.45) * mm});
            skLineSegment(sketch, "E30.19.0", {"start": v(-21.94, -8.8) * mm, "end": v(-21.24, -8.82) * mm});
            skLineSegment(sketch, "E30.19.1", {"start": v(-21.23, -10.4) * mm, "end": v(-21.94, -8.8) * mm});
            skLineSegment(sketch, "E30.19.2", {"start": v(-20.74, -9.67) * mm, "end": v(-21.06, -8.94) * mm});
            skLineSegment(sketch, "E30.19.3", {"start": v(-21.23, -10.4) * mm, "end": v(-20.77, -9.88) * mm});
            skArc(sketch, "E30.19.4", {"start": v(-21.06, -8.94) * mm, "mid": v(-21.13, -8.86) * mm, "end": v(-21.24, -8.82) * mm});
            skArc(sketch, "E30.19.5", {"start": v(-20.77, -9.88) * mm, "mid": v(-20.72, -9.78) * mm, "end": v(-20.74, -9.67) * mm});
            skLineSegment(sketch, "E30.20.0", {"start": v(-20.9, -11.05) * mm, "end": v(-20.2, -11) * mm});
            skLineSegment(sketch, "E30.20.1", {"start": v(-20.02, -12.57) * mm, "end": v(-20.9, -11.05) * mm});
            skLineSegment(sketch, "E30.20.2", {"start": v(-19.61, -11.78) * mm, "end": v(-20, -11.1) * mm});
            skLineSegment(sketch, "E30.20.3", {"start": v(-20.02, -12.57) * mm, "end": v(-19.62, -12) * mm});
            skArc(sketch, "E30.20.4", {"start": v(-20, -11.1) * mm, "mid": v(-20.1, -11.02) * mm, "end": v(-20.2, -11) * mm});
            skArc(sketch, "E30.20.5", {"start": v(-19.62, -12) * mm, "mid": v(-19.58, -11.9) * mm, "end": v(-19.61, -11.78) * mm});
            skLineSegment(sketch, "E30.21.0", {"start": v(-19.63, -13.18) * mm, "end": v(-18.94, -13.04) * mm});
            skLineSegment(sketch, "E30.21.1", {"start": v(-18.6, -14.6) * mm, "end": v(-19.63, -13.18) * mm});
            skLineSegment(sketch, "E30.21.2", {"start": v(-18.27, -13.77) * mm, "end": v(-18.74, -13.12) * mm});
            skLineSegment(sketch, "E30.21.3", {"start": v(-18.6, -14.6) * mm, "end": v(-18.26, -13.98) * mm});
            skArc(sketch, "E30.21.4", {"start": v(-18.74, -13.12) * mm, "mid": v(-18.83, -13.06) * mm, "end": v(-18.94, -13.04) * mm});
            skArc(sketch, "E30.21.5", {"start": v(-18.26, -13.98) * mm, "mid": v(-18.23, -13.87) * mm, "end": v(-18.27, -13.77) * mm});
            skLineSegment(sketch, "E30.22.0", {"start": v(-18.14, -15.16) * mm, "end": v(-17.47, -14.95) * mm});
            skLineSegment(sketch, "E30.22.1", {"start": v(-16.97, -16.46) * mm, "end": v(-18.14, -15.16) * mm});
            skLineSegment(sketch, "E30.22.2", {"start": v(-16.73, -15.6) * mm, "end": v(-17.27, -15.01) * mm});
            skLineSegment(sketch, "E30.22.3", {"start": v(-16.97, -16.46) * mm, "end": v(-16.7, -15.81) * mm});
            skArc(sketch, "E30.22.4", {"start": v(-17.27, -15.01) * mm, "mid": v(-17.36, -14.95) * mm, "end": v(-17.47, -14.95) * mm});
            skArc(sketch, "E30.22.5", {"start": v(-16.7, -15.81) * mm, "mid": v(-16.68, -15.7) * mm, "end": v(-16.73, -15.6) * mm});
            skLineSegment(sketch, "E30.23.0", {"start": v(-16.46, -16.97) * mm, "end": v(-15.81, -16.7) * mm});
            skLineSegment(sketch, "E30.23.1", {"start": v(-15.16, -18.14) * mm, "end": v(-16.46, -16.97) * mm});
            skLineSegment(sketch, "E30.23.2", {"start": v(-15.01, -17.27) * mm, "end": v(-15.6, -16.73) * mm});
            skLineSegment(sketch, "E30.23.3", {"start": v(-15.16, -18.14) * mm, "end": v(-14.95, -17.47) * mm});
            skArc(sketch, "E30.23.4", {"start": v(-15.6, -16.73) * mm, "mid": v(-15.7, -16.68) * mm, "end": v(-15.81, -16.7) * mm});
            skArc(sketch, "E30.23.5", {"start": v(-14.95, -17.47) * mm, "mid": v(-14.95, -17.36) * mm, "end": v(-15.01, -17.27) * mm});
            skLineSegment(sketch, "E30.24.0", {"start": v(-14.6, -18.6) * mm, "end": v(-13.98, -18.26) * mm});
            skLineSegment(sketch, "E30.24.1", {"start": v(-13.18, -19.63) * mm, "end": v(-14.6, -18.6) * mm});
            skLineSegment(sketch, "E30.24.2", {"start": v(-13.12, -18.74) * mm, "end": v(-13.77, -18.27) * mm});
            skLineSegment(sketch, "E30.24.3", {"start": v(-13.18, -19.63) * mm, "end": v(-13.04, -18.94) * mm});
            skArc(sketch, "E30.24.4", {"start": v(-13.77, -18.27) * mm, "mid": v(-13.87, -18.23) * mm, "end": v(-13.98, -18.26) * mm});
            skArc(sketch, "E30.24.5", {"start": v(-13.04, -18.94) * mm, "mid": v(-13.06, -18.83) * mm, "end": v(-13.12, -18.74) * mm});
            skLineSegment(sketch, "E30.25.0", {"start": v(-12.57, -20.02) * mm, "end": v(-12, -19.62) * mm});
            skLineSegment(sketch, "E30.25.1", {"start": v(-11.05, -20.9) * mm, "end": v(-12.57, -20.02) * mm});
            skLineSegment(sketch, "E30.25.2", {"start": v(-11.1, -20) * mm, "end": v(-11.78, -19.61) * mm});
            skLineSegment(sketch, "E30.25.3", {"start": v(-11.05, -20.9) * mm, "end": v(-11, -20.2) * mm});
            skArc(sketch, "E30.25.4", {"start": v(-11.78, -19.61) * mm, "mid": v(-11.9, -19.58) * mm, "end": v(-12, -19.62) * mm});
            skArc(sketch, "E30.25.5", {"start": v(-11, -20.2) * mm, "mid": v(-11.02, -20.1) * mm, "end": v(-11.1, -20) * mm});
            skLineSegment(sketch, "E30.26.0", {"start": v(-10.4, -21.23) * mm, "end": v(-9.88, -20.77) * mm});
            skLineSegment(sketch, "E30.26.1", {"start": v(-8.8, -21.94) * mm, "end": v(-10.4, -21.23) * mm});
            skLineSegment(sketch, "E30.26.2", {"start": v(-8.94, -21.06) * mm, "end": v(-9.67, -20.74) * mm});
            skLineSegment(sketch, "E30.26.3", {"start": v(-8.8, -21.94) * mm, "end": v(-8.82, -21.24) * mm});
            skArc(sketch, "E30.26.4", {"start": v(-9.67, -20.74) * mm, "mid": v(-9.78, -20.72) * mm, "end": v(-9.88, -20.77) * mm});
            skArc(sketch, "E30.26.5", {"start": v(-8.82, -21.24) * mm, "mid": v(-8.86, -21.13) * mm, "end": v(-8.94, -21.06) * mm});
            skLineSegment(sketch, "E30.27.0", {"start": v(-8.13, -22.2) * mm, "end": v(-7.66, -21.69) * mm});
            skLineSegment(sketch, "E30.27.1", {"start": v(-6.47, -22.74) * mm, "end": v(-8.13, -22.2) * mm});
            skLineSegment(sketch, "E30.27.2", {"start": v(-6.7, -21.88) * mm, "end": v(-7.45, -21.63) * mm});
            skLineSegment(sketch, "E30.27.3", {"start": v(-6.47, -22.74) * mm, "end": v(-6.55, -22.04) * mm});
            skArc(sketch, "E30.27.4", {"start": v(-7.45, -21.63) * mm, "mid": v(-7.56, -21.63) * mm, "end": v(-7.66, -21.69) * mm});
            skArc(sketch, "E30.27.5", {"start": v(-6.55, -22.04) * mm, "mid": v(-6.6, -21.94) * mm, "end": v(-6.7, -21.88) * mm});
            skLineSegment(sketch, "E30.28.0", {"start": v(-5.77, -22.93) * mm, "end": v(-5.35, -22.37) * mm});
            skLineSegment(sketch, "E30.28.1", {"start": v(-4.06, -23.3) * mm, "end": v(-5.77, -22.93) * mm});
            skLineSegment(sketch, "E30.28.2", {"start": v(-4.37, -22.46) * mm, "end": v(-5.15, -22.3) * mm});
            skLineSegment(sketch, "E30.28.3", {"start": v(-4.06, -23.3) * mm, "end": v(-4.21, -22.6) * mm});
            skArc(sketch, "E30.28.4", {"start": v(-5.15, -22.3) * mm, "mid": v(-5.26, -22.3) * mm, "end": v(-5.35, -22.37) * mm});
            skArc(sketch, "E30.28.5", {"start": v(-4.21, -22.6) * mm, "mid": v(-4.27, -22.51) * mm, "end": v(-4.37, -22.46) * mm});
            skLineSegment(sketch, "E30.29.0", {"start": v(-3.34, -23.4) * mm, "end": v(-2.98, -22.8) * mm});
            skLineSegment(sketch, "E30.29.1", {"start": v(-1.6, -23.59) * mm, "end": v(-3.34, -23.4) * mm});
            skLineSegment(sketch, "E30.29.2", {"start": v(-2, -22.8) * mm, "end": v(-2.79, -22.7) * mm});
            skLineSegment(sketch, "E30.29.3", {"start": v(-1.6, -23.59) * mm, "end": v(-1.83, -22.93) * mm});
            skArc(sketch, "E30.29.4", {"start": v(-2.79, -22.7) * mm, "mid": v(-2.9, -22.73) * mm, "end": v(-2.98, -22.8) * mm});
            skArc(sketch, "E30.29.5", {"start": v(-1.83, -22.93) * mm, "mid": v(-1.9, -22.83) * mm, "end": v(-2, -22.8) * mm});
            skLineSegment(sketch, "E30.30.0", {"start": v(-0.88, -23.62) * mm, "end": v(-0.58, -23) * mm});
            skLineSegment(sketch, "E30.30.1", {"start": v(0.87, -23.62) * mm, "end": v(-0.88, -23.62) * mm});
            skLineSegment(sketch, "E30.30.2", {"start": v(0.4, -22.88) * mm, "end": v(-0.4, -22.88) * mm});
            skLineSegment(sketch, "E30.30.3", {"start": v(0.87, -23.62) * mm, "end": v(0.58, -23) * mm});
            skArc(sketch, "E30.30.4", {"start": v(-0.4, -22.88) * mm, "mid": v(-0.5, -22.9) * mm, "end": v(-0.58, -23) * mm});
            skArc(sketch, "E30.30.5", {"start": v(0.58, -23) * mm, "mid": v(0.5, -22.9) * mm, "end": v(0.4, -22.88) * mm});
            skLineSegment(sketch, "E30.31.0", {"start": v(1.6, -23.59) * mm, "end": v(1.83, -22.93) * mm});
            skLineSegment(sketch, "E30.31.1", {"start": v(3.34, -23.4) * mm, "end": v(1.6, -23.59) * mm});
            skLineSegment(sketch, "E30.31.2", {"start": v(2.79, -22.7) * mm, "end": v(2, -22.8) * mm});
            skLineSegment(sketch, "E30.31.3", {"start": v(3.34, -23.4) * mm, "end": v(2.98, -22.8) * mm});
            skArc(sketch, "E30.31.4", {"start": v(2, -22.8) * mm, "mid": v(1.9, -22.83) * mm, "end": v(1.83, -22.93) * mm});
            skArc(sketch, "E30.31.5", {"start": v(2.98, -22.8) * mm, "mid": v(2.9, -22.73) * mm, "end": v(2.79, -22.7) * mm});
            skLineSegment(sketch, "E30.32.0", {"start": v(4.06, -23.3) * mm, "end": v(4.21, -22.6) * mm});
            skLineSegment(sketch, "E30.32.1", {"start": v(5.77, -22.93) * mm, "end": v(4.06, -23.3) * mm});
            skLineSegment(sketch, "E30.32.2", {"start": v(5.15, -22.3) * mm, "end": v(4.37, -22.46) * mm});
            skLineSegment(sketch, "E30.32.3", {"start": v(5.77, -22.93) * mm, "end": v(5.35, -22.37) * mm});
            skArc(sketch, "E30.32.4", {"start": v(4.37, -22.46) * mm, "mid": v(4.27, -22.51) * mm, "end": v(4.21, -22.6) * mm});
            skArc(sketch, "E30.32.5", {"start": v(5.35, -22.37) * mm, "mid": v(5.26, -22.3) * mm, "end": v(5.15, -22.3) * mm});
            skLineSegment(sketch, "E30.33.0", {"start": v(6.47, -22.74) * mm, "end": v(6.55, -22.04) * mm});
            skLineSegment(sketch, "E30.33.1", {"start": v(8.13, -22.2) * mm, "end": v(6.47, -22.74) * mm});
            skLineSegment(sketch, "E30.33.2", {"start": v(7.45, -21.63) * mm, "end": v(6.7, -21.88) * mm});
            skLineSegment(sketch, "E30.33.3", {"start": v(8.13, -22.2) * mm, "end": v(7.66, -21.69) * mm});
            skArc(sketch, "E30.33.4", {"start": v(6.7, -21.88) * mm, "mid": v(6.6, -21.94) * mm, "end": v(6.55, -22.04) * mm});
            skArc(sketch, "E30.33.5", {"start": v(7.66, -21.69) * mm, "mid": v(7.56, -21.63) * mm, "end": v(7.45, -21.63) * mm});
            skLineSegment(sketch, "E30.34.0", {"start": v(8.8, -21.94) * mm, "end": v(8.82, -21.24) * mm});
            skLineSegment(sketch, "E30.34.1", {"start": v(10.4, -21.23) * mm, "end": v(8.8, -21.94) * mm});
            skLineSegment(sketch, "E30.34.2", {"start": v(9.67, -20.74) * mm, "end": v(8.94, -21.06) * mm});
            skLineSegment(sketch, "E30.34.3", {"start": v(10.4, -21.23) * mm, "end": v(9.88, -20.77) * mm});
            skArc(sketch, "E30.34.4", {"start": v(8.94, -21.06) * mm, "mid": v(8.86, -21.13) * mm, "end": v(8.82, -21.24) * mm});
            skArc(sketch, "E30.34.5", {"start": v(9.88, -20.77) * mm, "mid": v(9.78, -20.72) * mm, "end": v(9.67, -20.74) * mm});
            skLineSegment(sketch, "E30.35.0", {"start": v(11.05, -20.9) * mm, "end": v(11, -20.2) * mm});
            skLineSegment(sketch, "E30.35.1", {"start": v(12.57, -20.02) * mm, "end": v(11.05, -20.9) * mm});
            skLineSegment(sketch, "E30.35.2", {"start": v(11.78, -19.61) * mm, "end": v(11.1, -20) * mm});
            skLineSegment(sketch, "E30.35.3", {"start": v(12.57, -20.02) * mm, "end": v(12, -19.62) * mm});
            skArc(sketch, "E30.35.4", {"start": v(11.1, -20) * mm, "mid": v(11.02, -20.1) * mm, "end": v(11, -20.2) * mm});
            skArc(sketch, "E30.35.5", {"start": v(12, -19.62) * mm, "mid": v(11.9, -19.58) * mm, "end": v(11.78, -19.61) * mm});
            skLineSegment(sketch, "E30.36.0", {"start": v(13.18, -19.63) * mm, "end": v(13.04, -18.94) * mm});
            skLineSegment(sketch, "E30.36.1", {"start": v(14.6, -18.6) * mm, "end": v(13.18, -19.63) * mm});
            skLineSegment(sketch, "E30.36.2", {"start": v(13.77, -18.27) * mm, "end": v(13.12, -18.74) * mm});
            skLineSegment(sketch, "E30.36.3", {"start": v(14.6, -18.6) * mm, "end": v(13.98, -18.26) * mm});
            skArc(sketch, "E30.36.4", {"start": v(13.12, -18.74) * mm, "mid": v(13.06, -18.83) * mm, "end": v(13.04, -18.94) * mm});
            skArc(sketch, "E30.36.5", {"start": v(13.98, -18.26) * mm, "mid": v(13.87, -18.23) * mm, "end": v(13.77, -18.27) * mm});
            skLineSegment(sketch, "E30.37.0", {"start": v(15.16, -18.14) * mm, "end": v(14.95, -17.47) * mm});
            skLineSegment(sketch, "E30.37.1", {"start": v(16.46, -16.97) * mm, "end": v(15.16, -18.14) * mm});
            skLineSegment(sketch, "E30.37.2", {"start": v(15.6, -16.73) * mm, "end": v(15.01, -17.27) * mm});
            skLineSegment(sketch, "E30.37.3", {"start": v(16.46, -16.97) * mm, "end": v(15.81, -16.7) * mm});
            skArc(sketch, "E30.37.4", {"start": v(15.01, -17.27) * mm, "mid": v(14.95, -17.36) * mm, "end": v(14.95, -17.47) * mm});
            skArc(sketch, "E30.37.5", {"start": v(15.81, -16.7) * mm, "mid": v(15.7, -16.68) * mm, "end": v(15.6, -16.73) * mm});
            skLineSegment(sketch, "E30.38.0", {"start": v(16.97, -16.46) * mm, "end": v(16.7, -15.81) * mm});
            skLineSegment(sketch, "E30.38.1", {"start": v(18.14, -15.16) * mm, "end": v(16.97, -16.46) * mm});
            skLineSegment(sketch, "E30.38.2", {"start": v(17.27, -15.01) * mm, "end": v(16.73, -15.6) * mm});
            skLineSegment(sketch, "E30.38.3", {"start": v(18.14, -15.16) * mm, "end": v(17.47, -14.95) * mm});
            skArc(sketch, "E30.38.4", {"start": v(16.73, -15.6) * mm, "mid": v(16.68, -15.7) * mm, "end": v(16.7, -15.81) * mm});
            skArc(sketch, "E30.38.5", {"start": v(17.47, -14.95) * mm, "mid": v(17.36, -14.95) * mm, "end": v(17.27, -15.01) * mm});
            skLineSegment(sketch, "E30.39.0", {"start": v(18.6, -14.6) * mm, "end": v(18.26, -13.98) * mm});
            skLineSegment(sketch, "E30.39.1", {"start": v(19.63, -13.18) * mm, "end": v(18.6, -14.6) * mm});
            skLineSegment(sketch, "E30.39.2", {"start": v(18.74, -13.12) * mm, "end": v(18.27, -13.77) * mm});
            skLineSegment(sketch, "E30.39.3", {"start": v(19.63, -13.18) * mm, "end": v(18.94, -13.04) * mm});
            skArc(sketch, "E30.39.4", {"start": v(18.27, -13.77) * mm, "mid": v(18.23, -13.87) * mm, "end": v(18.26, -13.98) * mm});
            skArc(sketch, "E30.39.5", {"start": v(18.94, -13.04) * mm, "mid": v(18.83, -13.06) * mm, "end": v(18.74, -13.12) * mm});
            skLineSegment(sketch, "E30.40.0", {"start": v(20.02, -12.57) * mm, "end": v(19.62, -12) * mm});
            skLineSegment(sketch, "E30.40.1", {"start": v(20.9, -11.05) * mm, "end": v(20.02, -12.57) * mm});
            skLineSegment(sketch, "E30.40.2", {"start": v(20, -11.1) * mm, "end": v(19.61, -11.78) * mm});
            skLineSegment(sketch, "E30.40.3", {"start": v(20.9, -11.05) * mm, "end": v(20.2, -11) * mm});
            skArc(sketch, "E30.40.4", {"start": v(19.61, -11.78) * mm, "mid": v(19.58, -11.9) * mm, "end": v(19.62, -12) * mm});
            skArc(sketch, "E30.40.5", {"start": v(20.2, -11) * mm, "mid": v(20.1, -11.02) * mm, "end": v(20, -11.1) * mm});
            skLineSegment(sketch, "E30.41.0", {"start": v(21.23, -10.4) * mm, "end": v(20.77, -9.88) * mm});
            skLineSegment(sketch, "E30.41.1", {"start": v(21.94, -8.8) * mm, "end": v(21.23, -10.4) * mm});
            skLineSegment(sketch, "E30.41.2", {"start": v(21.06, -8.94) * mm, "end": v(20.74, -9.67) * mm});
            skLineSegment(sketch, "E30.41.3", {"start": v(21.94, -8.8) * mm, "end": v(21.24, -8.82) * mm});
            skArc(sketch, "E30.41.4", {"start": v(20.74, -9.67) * mm, "mid": v(20.72, -9.78) * mm, "end": v(20.77, -9.88) * mm});
            skArc(sketch, "E30.41.5", {"start": v(21.24, -8.82) * mm, "mid": v(21.13, -8.86) * mm, "end": v(21.06, -8.94) * mm});
            skLineSegment(sketch, "E30.42.0", {"start": v(22.2, -8.13) * mm, "end": v(21.69, -7.66) * mm});
            skLineSegment(sketch, "E30.42.1", {"start": v(22.74, -6.47) * mm, "end": v(22.2, -8.13) * mm});
            skLineSegment(sketch, "E30.42.2", {"start": v(21.88, -6.7) * mm, "end": v(21.63, -7.45) * mm});
            skLineSegment(sketch, "E30.42.3", {"start": v(22.74, -6.47) * mm, "end": v(22.04, -6.55) * mm});
            skArc(sketch, "E30.42.4", {"start": v(21.63, -7.45) * mm, "mid": v(21.63, -7.56) * mm, "end": v(21.69, -7.66) * mm});
            skArc(sketch, "E30.42.5", {"start": v(22.04, -6.55) * mm, "mid": v(21.94, -6.6) * mm, "end": v(21.88, -6.7) * mm});
            skLineSegment(sketch, "E30.43.0", {"start": v(22.93, -5.77) * mm, "end": v(22.37, -5.35) * mm});
            skLineSegment(sketch, "E30.43.1", {"start": v(23.3, -4.06) * mm, "end": v(22.93, -5.77) * mm});
            skLineSegment(sketch, "E30.43.2", {"start": v(22.46, -4.37) * mm, "end": v(22.3, -5.15) * mm});
            skLineSegment(sketch, "E30.43.3", {"start": v(23.3, -4.06) * mm, "end": v(22.6, -4.21) * mm});
            skArc(sketch, "E30.43.4", {"start": v(22.3, -5.15) * mm, "mid": v(22.3, -5.26) * mm, "end": v(22.37, -5.35) * mm});
            skArc(sketch, "E30.43.5", {"start": v(22.6, -4.21) * mm, "mid": v(22.51, -4.27) * mm, "end": v(22.46, -4.37) * mm});
            skLineSegment(sketch, "E30.44.0", {"start": v(23.4, -3.34) * mm, "end": v(22.8, -2.98) * mm});
            skLineSegment(sketch, "E30.44.1", {"start": v(23.59, -1.6) * mm, "end": v(23.4, -3.34) * mm});
            skLineSegment(sketch, "E30.44.2", {"start": v(22.8, -2) * mm, "end": v(22.7, -2.79) * mm});
            skLineSegment(sketch, "E30.44.3", {"start": v(23.59, -1.6) * mm, "end": v(22.93, -1.83) * mm});
            skArc(sketch, "E30.44.4", {"start": v(22.7, -2.79) * mm, "mid": v(22.73, -2.9) * mm, "end": v(22.8, -2.98) * mm});
            skArc(sketch, "E30.44.5", {"start": v(22.93, -1.83) * mm, "mid": v(22.83, -1.9) * mm, "end": v(22.8, -2) * mm});
            skLineSegment(sketch, "E30.45.0", {"start": v(23.62, -0.88) * mm, "end": v(23, -0.58) * mm});
            skLineSegment(sketch, "E30.45.1", {"start": v(23.62, 0.87) * mm, "end": v(23.62, -0.88) * mm});
            skLineSegment(sketch, "E30.45.2", {"start": v(22.88, 0.4) * mm, "end": v(22.88, -0.4) * mm});
            skLineSegment(sketch, "E30.45.3", {"start": v(23.62, 0.87) * mm, "end": v(23, 0.58) * mm});
            skArc(sketch, "E30.45.4", {"start": v(22.88, -0.4) * mm, "mid": v(22.9, -0.5) * mm, "end": v(23, -0.58) * mm});
            skArc(sketch, "E30.45.5", {"start": v(23, 0.58) * mm, "mid": v(22.9, 0.5) * mm, "end": v(22.88, 0.4) * mm});
            skLineSegment(sketch, "E30.46.0", {"start": v(23.59, 1.6) * mm, "end": v(22.93, 1.83) * mm});
            skLineSegment(sketch, "E30.46.1", {"start": v(23.4, 3.34) * mm, "end": v(23.59, 1.6) * mm});
            skLineSegment(sketch, "E30.46.2", {"start": v(22.7, 2.79) * mm, "end": v(22.8, 2) * mm});
            skLineSegment(sketch, "E30.46.3", {"start": v(23.4, 3.34) * mm, "end": v(22.8, 2.98) * mm});
            skArc(sketch, "E30.46.4", {"start": v(22.8, 2) * mm, "mid": v(22.83, 1.9) * mm, "end": v(22.93, 1.83) * mm});
            skArc(sketch, "E30.46.5", {"start": v(22.8, 2.98) * mm, "mid": v(22.73, 2.9) * mm, "end": v(22.7, 2.79) * mm});
            skLineSegment(sketch, "E30.47.0", {"start": v(23.3, 4.06) * mm, "end": v(22.6, 4.21) * mm});
            skLineSegment(sketch, "E30.47.1", {"start": v(22.93, 5.77) * mm, "end": v(23.3, 4.06) * mm});
            skLineSegment(sketch, "E30.47.2", {"start": v(22.3, 5.15) * mm, "end": v(22.46, 4.37) * mm});
            skLineSegment(sketch, "E30.47.3", {"start": v(22.93, 5.77) * mm, "end": v(22.37, 5.35) * mm});
            skArc(sketch, "E30.47.4", {"start": v(22.46, 4.37) * mm, "mid": v(22.51, 4.27) * mm, "end": v(22.6, 4.21) * mm});
            skArc(sketch, "E30.47.5", {"start": v(22.37, 5.35) * mm, "mid": v(22.3, 5.26) * mm, "end": v(22.3, 5.15) * mm});
            skLineSegment(sketch, "E30.48.0", {"start": v(22.74, 6.47) * mm, "end": v(22.04, 6.55) * mm});
            skLineSegment(sketch, "E30.48.1", {"start": v(22.2, 8.13) * mm, "end": v(22.74, 6.47) * mm});
            skLineSegment(sketch, "E30.48.2", {"start": v(21.63, 7.45) * mm, "end": v(21.88, 6.7) * mm});
            skLineSegment(sketch, "E30.48.3", {"start": v(22.2, 8.13) * mm, "end": v(21.69, 7.66) * mm});
            skArc(sketch, "E30.48.4", {"start": v(21.88, 6.7) * mm, "mid": v(21.94, 6.6) * mm, "end": v(22.04, 6.55) * mm});
            skArc(sketch, "E30.48.5", {"start": v(21.69, 7.66) * mm, "mid": v(21.63, 7.56) * mm, "end": v(21.63, 7.45) * mm});
            skLineSegment(sketch, "E30.49.0", {"start": v(21.94, 8.8) * mm, "end": v(21.24, 8.82) * mm});
            skLineSegment(sketch, "E30.49.1", {"start": v(21.23, 10.4) * mm, "end": v(21.94, 8.8) * mm});
            skLineSegment(sketch, "E30.49.2", {"start": v(20.74, 9.67) * mm, "end": v(21.06, 8.94) * mm});
            skLineSegment(sketch, "E30.49.3", {"start": v(21.23, 10.4) * mm, "end": v(20.77, 9.88) * mm});
            skArc(sketch, "E30.49.4", {"start": v(21.06, 8.94) * mm, "mid": v(21.13, 8.86) * mm, "end": v(21.24, 8.82) * mm});
            skArc(sketch, "E30.49.5", {"start": v(20.77, 9.88) * mm, "mid": v(20.72, 9.78) * mm, "end": v(20.74, 9.67) * mm});
            skLineSegment(sketch, "E30.50.0", {"start": v(20.9, 11.05) * mm, "end": v(20.2, 11) * mm});
            skLineSegment(sketch, "E30.50.1", {"start": v(20.02, 12.57) * mm, "end": v(20.9, 11.05) * mm});
            skLineSegment(sketch, "E30.50.2", {"start": v(19.61, 11.78) * mm, "end": v(20, 11.1) * mm});
            skLineSegment(sketch, "E30.50.3", {"start": v(20.02, 12.57) * mm, "end": v(19.62, 12) * mm});
            skArc(sketch, "E30.50.4", {"start": v(20, 11.1) * mm, "mid": v(20.1, 11.02) * mm, "end": v(20.2, 11) * mm});
            skArc(sketch, "E30.50.5", {"start": v(19.62, 12) * mm, "mid": v(19.58, 11.9) * mm, "end": v(19.61, 11.78) * mm});
            skLineSegment(sketch, "E30.51.0", {"start": v(19.63, 13.18) * mm, "end": v(18.94, 13.04) * mm});
            skLineSegment(sketch, "E30.51.1", {"start": v(18.6, 14.6) * mm, "end": v(19.63, 13.18) * mm});
            skLineSegment(sketch, "E30.51.2", {"start": v(18.27, 13.77) * mm, "end": v(18.74, 13.12) * mm});
            skLineSegment(sketch, "E30.51.3", {"start": v(18.6, 14.6) * mm, "end": v(18.26, 13.98) * mm});
            skArc(sketch, "E30.51.4", {"start": v(18.74, 13.12) * mm, "mid": v(18.83, 13.06) * mm, "end": v(18.94, 13.04) * mm});
            skArc(sketch, "E30.51.5", {"start": v(18.26, 13.98) * mm, "mid": v(18.23, 13.87) * mm, "end": v(18.27, 13.77) * mm});
            skLineSegment(sketch, "E30.52.0", {"start": v(18.14, 15.16) * mm, "end": v(17.47, 14.95) * mm});
            skLineSegment(sketch, "E30.52.1", {"start": v(16.97, 16.46) * mm, "end": v(18.14, 15.16) * mm});
            skLineSegment(sketch, "E30.52.2", {"start": v(16.73, 15.6) * mm, "end": v(17.27, 15.01) * mm});
            skLineSegment(sketch, "E30.52.3", {"start": v(16.97, 16.46) * mm, "end": v(16.7, 15.81) * mm});
            skArc(sketch, "E30.52.4", {"start": v(17.27, 15.01) * mm, "mid": v(17.36, 14.95) * mm, "end": v(17.47, 14.95) * mm});
            skArc(sketch, "E30.52.5", {"start": v(16.7, 15.81) * mm, "mid": v(16.68, 15.7) * mm, "end": v(16.73, 15.6) * mm});
            skLineSegment(sketch, "E30.53.0", {"start": v(16.46, 16.97) * mm, "end": v(15.81, 16.7) * mm});
            skLineSegment(sketch, "E30.53.1", {"start": v(15.16, 18.14) * mm, "end": v(16.46, 16.97) * mm});
            skLineSegment(sketch, "E30.53.2", {"start": v(15.01, 17.27) * mm, "end": v(15.6, 16.73) * mm});
            skLineSegment(sketch, "E30.53.3", {"start": v(15.16, 18.14) * mm, "end": v(14.95, 17.47) * mm});
            skArc(sketch, "E30.53.4", {"start": v(15.6, 16.73) * mm, "mid": v(15.7, 16.68) * mm, "end": v(15.81, 16.7) * mm});
            skArc(sketch, "E30.53.5", {"start": v(14.95, 17.47) * mm, "mid": v(14.95, 17.36) * mm, "end": v(15.01, 17.27) * mm});
            skLineSegment(sketch, "E30.54.0", {"start": v(14.6, 18.6) * mm, "end": v(13.98, 18.26) * mm});
            skLineSegment(sketch, "E30.54.1", {"start": v(13.18, 19.63) * mm, "end": v(14.6, 18.6) * mm});
            skLineSegment(sketch, "E30.54.2", {"start": v(13.12, 18.74) * mm, "end": v(13.77, 18.27) * mm});
            skLineSegment(sketch, "E30.54.3", {"start": v(13.18, 19.63) * mm, "end": v(13.04, 18.94) * mm});
            skArc(sketch, "E30.54.4", {"start": v(13.77, 18.27) * mm, "mid": v(13.87, 18.23) * mm, "end": v(13.98, 18.26) * mm});
            skArc(sketch, "E30.54.5", {"start": v(13.04, 18.94) * mm, "mid": v(13.06, 18.83) * mm, "end": v(13.12, 18.74) * mm});
            skLineSegment(sketch, "E30.55.0", {"start": v(12.57, 20.02) * mm, "end": v(12, 19.62) * mm});
            skLineSegment(sketch, "E30.55.1", {"start": v(11.05, 20.9) * mm, "end": v(12.57, 20.02) * mm});
            skLineSegment(sketch, "E30.55.2", {"start": v(11.1, 20) * mm, "end": v(11.78, 19.61) * mm});
            skLineSegment(sketch, "E30.55.3", {"start": v(11.05, 20.9) * mm, "end": v(11, 20.2) * mm});
            skArc(sketch, "E30.55.4", {"start": v(11.78, 19.61) * mm, "mid": v(11.9, 19.58) * mm, "end": v(12, 19.62) * mm});
            skArc(sketch, "E30.55.5", {"start": v(11, 20.2) * mm, "mid": v(11.02, 20.1) * mm, "end": v(11.1, 20) * mm});
            skLineSegment(sketch, "E30.56.0", {"start": v(10.4, 21.23) * mm, "end": v(9.88, 20.77) * mm});
            skLineSegment(sketch, "E30.56.1", {"start": v(8.8, 21.94) * mm, "end": v(10.4, 21.23) * mm});
            skLineSegment(sketch, "E30.56.2", {"start": v(8.94, 21.06) * mm, "end": v(9.67, 20.74) * mm});
            skLineSegment(sketch, "E30.56.3", {"start": v(8.8, 21.94) * mm, "end": v(8.82, 21.24) * mm});
            skArc(sketch, "E30.56.4", {"start": v(9.67, 20.74) * mm, "mid": v(9.78, 20.72) * mm, "end": v(9.88, 20.77) * mm});
            skArc(sketch, "E30.56.5", {"start": v(8.82, 21.24) * mm, "mid": v(8.86, 21.13) * mm, "end": v(8.94, 21.06) * mm});
            skLineSegment(sketch, "E30.57.0", {"start": v(8.13, 22.2) * mm, "end": v(7.66, 21.69) * mm});
            skLineSegment(sketch, "E30.57.1", {"start": v(6.47, 22.74) * mm, "end": v(8.13, 22.2) * mm});
            skLineSegment(sketch, "E30.57.2", {"start": v(6.7, 21.88) * mm, "end": v(7.45, 21.63) * mm});
            skLineSegment(sketch, "E30.57.3", {"start": v(6.47, 22.74) * mm, "end": v(6.55, 22.04) * mm});
            skArc(sketch, "E30.57.4", {"start": v(7.45, 21.63) * mm, "mid": v(7.56, 21.63) * mm, "end": v(7.66, 21.69) * mm});
            skArc(sketch, "E30.57.5", {"start": v(6.55, 22.04) * mm, "mid": v(6.6, 21.94) * mm, "end": v(6.7, 21.88) * mm});
            skLineSegment(sketch, "E30.58.0", {"start": v(5.77, 22.93) * mm, "end": v(5.35, 22.37) * mm});
            skLineSegment(sketch, "E30.58.1", {"start": v(4.06, 23.3) * mm, "end": v(5.77, 22.93) * mm});
            skLineSegment(sketch, "E30.58.2", {"start": v(4.37, 22.46) * mm, "end": v(5.15, 22.3) * mm});
            skLineSegment(sketch, "E30.58.3", {"start": v(4.06, 23.3) * mm, "end": v(4.21, 22.6) * mm});
            skArc(sketch, "E30.58.4", {"start": v(5.15, 22.3) * mm, "mid": v(5.26, 22.3) * mm, "end": v(5.35, 22.37) * mm});
            skArc(sketch, "E30.58.5", {"start": v(4.21, 22.6) * mm, "mid": v(4.27, 22.51) * mm, "end": v(4.37, 22.46) * mm});
            skLineSegment(sketch, "E30.59.0", {"start": v(3.34, 23.4) * mm, "end": v(2.98, 22.8) * mm});
            skLineSegment(sketch, "E30.59.1", {"start": v(1.6, 23.59) * mm, "end": v(3.34, 23.4) * mm});
            skLineSegment(sketch, "E30.59.2", {"start": v(2, 22.8) * mm, "end": v(2.79, 22.7) * mm});
            skLineSegment(sketch, "E30.59.3", {"start": v(1.6, 23.59) * mm, "end": v(1.83, 22.93) * mm});
            skArc(sketch, "E30.59.4", {"start": v(2.79, 22.7) * mm, "mid": v(2.9, 22.73) * mm, "end": v(2.98, 22.8) * mm});
            skArc(sketch, "E30.59.5", {"start": v(1.83, 22.93) * mm, "mid": v(1.9, 22.83) * mm, "end": v(2, 22.8) * mm});
            skCircle(sketch, "E31.0", {"center": v(0, 0) * mm, "radius": 12 * mm});
            skCircle(sketch, "E32", {"center": v(0, 0) * mm, "radius": 10.9 * mm});
            skSolve(sketch);
        }
        {
            var Q0;
            Q0=makeQuery(id+"F6.imprint","IMPRINT",FACE,{"disambiguationData":[TD([[makeQuery(id+"F6.imprint","IMPRINT",EDGE,{"derivedFrom":sQuery(id+"F6.wireOp",EDGE,"E19.0")}),1.0]])]});
            var Q1;
            Q1=makeQuery(id+"F6.imprint","IMPRINT",FACE,{"disambiguationData":[TD([[makeQuery(id+"F6.imprint","IMPRINT",EDGE,{"derivedFrom":sQuery(id+"F6.wireOp",EDGE,"E19.0")}),-1.0]])]});
            var Q2;
            Q2=makeQuery(id+"F6.imprint","IMPRINT",FACE,{"disambiguationData":[TD([[makeQuery(id+"F6.imprint","IMPRINT",EDGE,{"derivedFrom":sQuery(id+"F6.wireOp",EDGE,"E31.0")}),1.0]])]});
            extrude(context, id + "F7", {"entities" : qUnion([Q0, Q1, Q2]), "depth" : 7 * mm});
        }
        {
            var Q0;
            Q0=makeQuery(id+"F7.opExtrude","CAP_FACE",FACE,{"disambiguationData":[OSD([sQuery(id+"F6.wireOp",EDGE,"E22"),sQuery(id+"F6.wireOp",EDGE,"E25"),sQuery(id+"F6.wireOp",EDGE,"E26"),sQuery(id+"F6.wireOp",EDGE,"E27"),sQuery(id+"F6.wireOp",EDGE,"E28.filletArc"),sQuery(id+"F6.wireOp",EDGE,"E29.filletArc"),sQuery(id+"F6.wireOp",EDGE,"E30.1.0"),sQuery(id+"F6.wireOp",EDGE,"E30.1.2"),sQuery(id+"F6.wireOp",EDGE,"E30.1.3"),sQuery(id+"F6.wireOp",EDGE,"E30.1.4"),sQuery(id+"F6.wireOp",EDGE,"E30.1.5"),sQuery(id+"F6.wireOp",EDGE,"E30.2.0"),sQuery(id+"F6.wireOp",EDGE,"E30.2.2"),sQuery(id+"F6.wireOp",EDGE,"E30.2.3"),sQuery(id+"F6.wireOp",EDGE,"E30.2.4"),sQuery(id+"F6.wireOp",EDGE,"E30.2.5"),sQuery(id+"F6.wireOp",EDGE,"E30.3.0"),sQuery(id+"F6.wireOp",EDGE,"E30.3.2"),sQuery(id+"F6.wireOp",EDGE,"E30.3.3"),sQuery(id+"F6.wireOp",EDGE,"E30.3.4"),sQuery(id+"F6.wireOp",EDGE,"E30.3.5"),sQuery(id+"F6.wireOp",EDGE,"E30.4.0"),sQuery(id+"F6.wireOp",EDGE,"E30.4.2"),sQuery(id+"F6.wireOp",EDGE,"E30.4.3"),sQuery(id+"F6.wireOp",EDGE,"E30.4.4"),sQuery(id+"F6.wireOp",EDGE,"E30.4.5"),sQuery(id+"F6.wireOp",EDGE,"E30.5.0"),sQuery(id+"F6.wireOp",EDGE,"E30.5.2"),sQuery(id+"F6.wireOp",EDGE,"E30.5.3"),sQuery(id+"F6.wireOp",EDGE,"E30.5.4"),sQuery(id+"F6.wireOp",EDGE,"E30.5.5"),sQuery(id+"F6.wireOp",EDGE,"E30.6.0"),sQuery(id+"F6.wireOp",EDGE,"E30.6.2"),sQuery(id+"F6.wireOp",EDGE,"E30.6.3"),sQuery(id+"F6.wireOp",EDGE,"E30.6.4"),sQuery(id+"F6.wireOp",EDGE,"E30.6.5"),sQuery(id+"F6.wireOp",EDGE,"E30.7.0"),sQuery(id+"F6.wireOp",EDGE,"E30.7.2"),sQuery(id+"F6.wireOp",EDGE,"E30.7.3"),sQuery(id+"F6.wireOp",EDGE,"E30.7.4"),sQuery(id+"F6.wireOp",EDGE,"E30.7.5"),sQuery(id+"F6.wireOp",EDGE,"E30.8.0"),sQuery(id+"F6.wireOp",EDGE,"E30.8.2"),sQuery(id+"F6.wireOp",EDGE,"E30.8.3"),sQuery(id+"F6.wireOp",EDGE,"E30.8.4"),sQuery(id+"F6.wireOp",EDGE,"E30.8.5"),sQuery(id+"F6.wireOp",EDGE,"E30.9.0"),sQuery(id+"F6.wireOp",EDGE,"E30.9.2"),sQuery(id+"F6.wireOp",EDGE,"E30.9.3"),sQuery(id+"F6.wireOp",EDGE,"E30.9.4"),sQuery(id+"F6.wireOp",EDGE,"E30.9.5"),sQuery(id+"F6.wireOp",EDGE,"E30.10.0"),sQuery(id+"F6.wireOp",EDGE,"E30.10.2"),sQuery(id+"F6.wireOp",EDGE,"E30.10.3"),sQuery(id+"F6.wireOp",EDGE,"E30.10.4"),sQuery(id+"F6.wireOp",EDGE,"E30.10.5"),sQuery(id+"F6.wireOp",EDGE,"E30.11.0"),sQuery(id+"F6.wireOp",EDGE,"E30.11.2"),sQuery(id+"F6.wireOp",EDGE,"E30.11.3"),sQuery(id+"F6.wireOp",EDGE,"E30.11.4"),sQuery(id+"F6.wireOp",EDGE,"E30.11.5"),sQuery(id+"F6.wireOp",EDGE,"E30.12.0"),sQuery(id+"F6.wireOp",EDGE,"E30.12.2"),sQuery(id+"F6.wireOp",EDGE,"E30.12.3"),sQuery(id+"F6.wireOp",EDGE,"E30.12.4"),sQuery(id+"F6.wireOp",EDGE,"E30.12.5"),sQuery(id+"F6.wireOp",EDGE,"E30.13.0"),sQuery(id+"F6.wireOp",EDGE,"E30.13.2"),sQuery(id+"F6.wireOp",EDGE,"E30.13.3"),sQuery(id+"F6.wireOp",EDGE,"E30.13.4"),sQuery(id+"F6.wireOp",EDGE,"E30.13.5"),sQuery(id+"F6.wireOp",EDGE,"E30.14.0"),sQuery(id+"F6.wireOp",EDGE,"E30.14.2"),sQuery(id+"F6.wireOp",EDGE,"E30.14.3"),sQuery(id+"F6.wireOp",EDGE,"E30.14.4"),sQuery(id+"F6.wireOp",EDGE,"E30.14.5"),sQuery(id+"F6.wireOp",EDGE,"E30.15.0"),sQuery(id+"F6.wireOp",EDGE,"E30.15.2"),sQuery(id+"F6.wireOp",EDGE,"E30.15.3"),sQuery(id+"F6.wireOp",EDGE,"E30.15.4"),sQuery(id+"F6.wireOp",EDGE,"E30.15.5"),sQuery(id+"F6.wireOp",EDGE,"E30.16.0"),sQuery(id+"F6.wireOp",EDGE,"E30.16.2"),sQuery(id+"F6.wireOp",EDGE,"E30.16.3"),sQuery(id+"F6.wireOp",EDGE,"E30.16.4"),sQuery(id+"F6.wireOp",EDGE,"E30.16.5"),sQuery(id+"F6.wireOp",EDGE,"E30.17.0"),sQuery(id+"F6.wireOp",EDGE,"E30.17.2"),sQuery(id+"F6.wireOp",EDGE,"E30.17.3"),sQuery(id+"F6.wireOp",EDGE,"E30.17.4"),sQuery(id+"F6.wireOp",EDGE,"E30.17.5"),sQuery(id+"F6.wireOp",EDGE,"E30.18.0"),sQuery(id+"F6.wireOp",EDGE,"E30.18.2"),sQuery(id+"F6.wireOp",EDGE,"E30.18.3"),sQuery(id+"F6.wireOp",EDGE,"E30.18.4"),sQuery(id+"F6.wireOp",EDGE,"E30.18.5"),sQuery(id+"F6.wireOp",EDGE,"E30.19.0"),sQuery(id+"F6.wireOp",EDGE,"E30.19.2"),sQuery(id+"F6.wireOp",EDGE,"E30.19.3"),sQuery(id+"F6.wireOp",EDGE,"E30.19.4"),sQuery(id+"F6.wireOp",EDGE,"E30.19.5"),sQuery(id+"F6.wireOp",EDGE,"E30.20.0"),sQuery(id+"F6.wireOp",EDGE,"E30.20.2"),sQuery(id+"F6.wireOp",EDGE,"E30.20.3"),sQuery(id+"F6.wireOp",EDGE,"E30.20.4"),sQuery(id+"F6.wireOp",EDGE,"E30.20.5"),sQuery(id+"F6.wireOp",EDGE,"E30.21.0"),sQuery(id+"F6.wireOp",EDGE,"E30.21.2"),sQuery(id+"F6.wireOp",EDGE,"E30.21.3"),sQuery(id+"F6.wireOp",EDGE,"E30.21.4"),sQuery(id+"F6.wireOp",EDGE,"E30.21.5"),sQuery(id+"F6.wireOp",EDGE,"E30.22.0"),sQuery(id+"F6.wireOp",EDGE,"E30.22.2"),sQuery(id+"F6.wireOp",EDGE,"E30.22.3"),sQuery(id+"F6.wireOp",EDGE,"E30.22.4"),sQuery(id+"F6.wireOp",EDGE,"E30.22.5"),sQuery(id+"F6.wireOp",EDGE,"E30.23.0"),sQuery(id+"F6.wireOp",EDGE,"E30.23.2"),sQuery(id+"F6.wireOp",EDGE,"E30.23.3"),sQuery(id+"F6.wireOp",EDGE,"E30.23.4"),sQuery(id+"F6.wireOp",EDGE,"E30.23.5"),sQuery(id+"F6.wireOp",EDGE,"E30.24.0"),sQuery(id+"F6.wireOp",EDGE,"E30.24.2"),sQuery(id+"F6.wireOp",EDGE,"E30.24.3"),sQuery(id+"F6.wireOp",EDGE,"E30.24.4"),sQuery(id+"F6.wireOp",EDGE,"E30.24.5"),sQuery(id+"F6.wireOp",EDGE,"E30.25.0"),sQuery(id+"F6.wireOp",EDGE,"E30.25.2"),sQuery(id+"F6.wireOp",EDGE,"E30.25.3"),sQuery(id+"F6.wireOp",EDGE,"E30.25.4"),sQuery(id+"F6.wireOp",EDGE,"E30.25.5"),sQuery(id+"F6.wireOp",EDGE,"E30.26.0"),sQuery(id+"F6.wireOp",EDGE,"E30.26.2"),sQuery(id+"F6.wireOp",EDGE,"E30.26.3"),sQuery(id+"F6.wireOp",EDGE,"E30.26.4"),sQuery(id+"F6.wireOp",EDGE,"E30.26.5"),sQuery(id+"F6.wireOp",EDGE,"E30.27.0"),sQuery(id+"F6.wireOp",EDGE,"E30.27.2"),sQuery(id+"F6.wireOp",EDGE,"E30.27.3"),sQuery(id+"F6.wireOp",EDGE,"E30.27.4"),sQuery(id+"F6.wireOp",EDGE,"E30.27.5"),sQuery(id+"F6.wireOp",EDGE,"E30.28.0"),sQuery(id+"F6.wireOp",EDGE,"E30.28.2"),sQuery(id+"F6.wireOp",EDGE,"E30.28.3"),sQuery(id+"F6.wireOp",EDGE,"E30.28.4"),sQuery(id+"F6.wireOp",EDGE,"E30.28.5"),sQuery(id+"F6.wireOp",EDGE,"E30.29.0"),sQuery(id+"F6.wireOp",EDGE,"E30.29.2"),sQuery(id+"F6.wireOp",EDGE,"E30.29.3"),sQuery(id+"F6.wireOp",EDGE,"E30.29.4"),sQuery(id+"F6.wireOp",EDGE,"E30.29.5"),sQuery(id+"F6.wireOp",EDGE,"E30.30.0"),sQuery(id+"F6.wireOp",EDGE,"E30.30.2"),sQuery(id+"F6.wireOp",EDGE,"E30.30.3"),sQuery(id+"F6.wireOp",EDGE,"E30.30.4"),sQuery(id+"F6.wireOp",EDGE,"E30.30.5"),sQuery(id+"F6.wireOp",EDGE,"E30.31.0"),sQuery(id+"F6.wireOp",EDGE,"E30.31.2"),sQuery(id+"F6.wireOp",EDGE,"E30.31.3"),sQuery(id+"F6.wireOp",EDGE,"E30.31.4"),sQuery(id+"F6.wireOp",EDGE,"E30.31.5"),sQuery(id+"F6.wireOp",EDGE,"E30.32.0"),sQuery(id+"F6.wireOp",EDGE,"E30.32.2"),sQuery(id+"F6.wireOp",EDGE,"E30.32.3"),sQuery(id+"F6.wireOp",EDGE,"E30.32.4"),sQuery(id+"F6.wireOp",EDGE,"E30.32.5"),sQuery(id+"F6.wireOp",EDGE,"E30.33.0"),sQuery(id+"F6.wireOp",EDGE,"E30.33.2"),sQuery(id+"F6.wireOp",EDGE,"E30.33.3"),sQuery(id+"F6.wireOp",EDGE,"E30.33.4"),sQuery(id+"F6.wireOp",EDGE,"E30.33.5"),sQuery(id+"F6.wireOp",EDGE,"E30.34.0"),sQuery(id+"F6.wireOp",EDGE,"E30.34.2"),sQuery(id+"F6.wireOp",EDGE,"E30.34.3"),sQuery(id+"F6.wireOp",EDGE,"E30.34.4"),sQuery(id+"F6.wireOp",EDGE,"E30.34.5"),sQuery(id+"F6.wireOp",EDGE,"E30.35.0"),sQuery(id+"F6.wireOp",EDGE,"E30.35.2"),sQuery(id+"F6.wireOp",EDGE,"E30.35.3"),sQuery(id+"F6.wireOp",EDGE,"E30.35.4"),sQuery(id+"F6.wireOp",EDGE,"E30.35.5"),sQuery(id+"F6.wireOp",EDGE,"E30.36.0"),sQuery(id+"F6.wireOp",EDGE,"E30.36.2"),sQuery(id+"F6.wireOp",EDGE,"E30.36.3"),sQuery(id+"F6.wireOp",EDGE,"E30.36.4"),sQuery(id+"F6.wireOp",EDGE,"E30.36.5"),sQuery(id+"F6.wireOp",EDGE,"E30.37.0"),sQuery(id+"F6.wireOp",EDGE,"E30.37.2"),sQuery(id+"F6.wireOp",EDGE,"E30.37.3"),sQuery(id+"F6.wireOp",EDGE,"E30.37.4"),sQuery(id+"F6.wireOp",EDGE,"E30.37.5"),sQuery(id+"F6.wireOp",EDGE,"E30.38.0"),sQuery(id+"F6.wireOp",EDGE,"E30.38.2"),sQuery(id+"F6.wireOp",EDGE,"E30.38.3"),sQuery(id+"F6.wireOp",EDGE,"E30.38.4"),sQuery(id+"F6.wireOp",EDGE,"E30.38.5"),sQuery(id+"F6.wireOp",EDGE,"E30.39.0"),sQuery(id+"F6.wireOp",EDGE,"E30.39.2"),sQuery(id+"F6.wireOp",EDGE,"E30.39.3"),sQuery(id+"F6.wireOp",EDGE,"E30.39.4"),sQuery(id+"F6.wireOp",EDGE,"E30.39.5"),sQuery(id+"F6.wireOp",EDGE,"E30.40.0"),sQuery(id+"F6.wireOp",EDGE,"E30.40.2"),sQuery(id+"F6.wireOp",EDGE,"E30.40.3"),sQuery(id+"F6.wireOp",EDGE,"E30.40.4"),sQuery(id+"F6.wireOp",EDGE,"E30.40.5"),sQuery(id+"F6.wireOp",EDGE,"E30.41.0"),sQuery(id+"F6.wireOp",EDGE,"E30.41.2"),sQuery(id+"F6.wireOp",EDGE,"E30.41.3"),sQuery(id+"F6.wireOp",EDGE,"E30.41.4"),sQuery(id+"F6.wireOp",EDGE,"E30.41.5"),sQuery(id+"F6.wireOp",EDGE,"E30.42.0"),sQuery(id+"F6.wireOp",EDGE,"E30.42.2"),sQuery(id+"F6.wireOp",EDGE,"E30.42.3"),sQuery(id+"F6.wireOp",EDGE,"E30.42.4"),sQuery(id+"F6.wireOp",EDGE,"E30.42.5"),sQuery(id+"F6.wireOp",EDGE,"E30.43.0"),sQuery(id+"F6.wireOp",EDGE,"E30.43.2"),sQuery(id+"F6.wireOp",EDGE,"E30.43.3"),sQuery(id+"F6.wireOp",EDGE,"E30.43.4"),sQuery(id+"F6.wireOp",EDGE,"E30.43.5"),sQuery(id+"F6.wireOp",EDGE,"E30.44.0"),sQuery(id+"F6.wireOp",EDGE,"E30.44.2"),sQuery(id+"F6.wireOp",EDGE,"E30.44.3"),sQuery(id+"F6.wireOp",EDGE,"E30.44.4"),sQuery(id+"F6.wireOp",EDGE,"E30.44.5"),sQuery(id+"F6.wireOp",EDGE,"E30.45.0"),sQuery(id+"F6.wireOp",EDGE,"E30.45.2"),sQuery(id+"F6.wireOp",EDGE,"E30.45.3"),sQuery(id+"F6.wireOp",EDGE,"E30.45.4"),sQuery(id+"F6.wireOp",EDGE,"E30.45.5"),sQuery(id+"F6.wireOp",EDGE,"E30.46.0"),sQuery(id+"F6.wireOp",EDGE,"E30.46.2"),sQuery(id+"F6.wireOp",EDGE,"E30.46.3"),sQuery(id+"F6.wireOp",EDGE,"E30.46.4"),sQuery(id+"F6.wireOp",EDGE,"E30.46.5"),sQuery(id+"F6.wireOp",EDGE,"E30.47.0"),sQuery(id+"F6.wireOp",EDGE,"E30.47.2"),sQuery(id+"F6.wireOp",EDGE,"E30.47.3"),sQuery(id+"F6.wireOp",EDGE,"E30.47.4"),sQuery(id+"F6.wireOp",EDGE,"E30.47.5"),sQuery(id+"F6.wireOp",EDGE,"E30.48.0"),sQuery(id+"F6.wireOp",EDGE,"E30.48.2"),sQuery(id+"F6.wireOp",EDGE,"E30.48.3"),sQuery(id+"F6.wireOp",EDGE,"E30.48.4"),sQuery(id+"F6.wireOp",EDGE,"E30.48.5"),sQuery(id+"F6.wireOp",EDGE,"E30.49.0"),sQuery(id+"F6.wireOp",EDGE,"E30.49.2"),sQuery(id+"F6.wireOp",EDGE,"E30.49.3"),sQuery(id+"F6.wireOp",EDGE,"E30.49.4"),sQuery(id+"F6.wireOp",EDGE,"E30.49.5"),sQuery(id+"F6.wireOp",EDGE,"E30.50.0"),sQuery(id+"F6.wireOp",EDGE,"E30.50.2"),sQuery(id+"F6.wireOp",EDGE,"E30.50.3"),sQuery(id+"F6.wireOp",EDGE,"E30.50.4"),sQuery(id+"F6.wireOp",EDGE,"E30.50.5"),sQuery(id+"F6.wireOp",EDGE,"E30.51.0"),sQuery(id+"F6.wireOp",EDGE,"E30.51.2"),sQuery(id+"F6.wireOp",EDGE,"E30.51.3"),sQuery(id+"F6.wireOp",EDGE,"E30.51.4"),sQuery(id+"F6.wireOp",EDGE,"E30.51.5"),sQuery(id+"F6.wireOp",EDGE,"E30.52.0"),sQuery(id+"F6.wireOp",EDGE,"E30.52.2"),sQuery(id+"F6.wireOp",EDGE,"E30.52.3"),sQuery(id+"F6.wireOp",EDGE,"E30.52.4"),sQuery(id+"F6.wireOp",EDGE,"E30.52.5"),sQuery(id+"F6.wireOp",EDGE,"E30.53.0"),sQuery(id+"F6.wireOp",EDGE,"E30.53.2"),sQuery(id+"F6.wireOp",EDGE,"E30.53.3"),sQuery(id+"F6.wireOp",EDGE,"E30.53.4"),sQuery(id+"F6.wireOp",EDGE,"E30.53.5"),sQuery(id+"F6.wireOp",EDGE,"E30.54.0"),sQuery(id+"F6.wireOp",EDGE,"E30.54.2"),sQuery(id+"F6.wireOp",EDGE,"E30.54.3"),sQuery(id+"F6.wireOp",EDGE,"E30.54.4"),sQuery(id+"F6.wireOp",EDGE,"E30.54.5"),sQuery(id+"F6.wireOp",EDGE,"E30.55.0"),sQuery(id+"F6.wireOp",EDGE,"E30.55.2"),sQuery(id+"F6.wireOp",EDGE,"E30.55.3"),sQuery(id+"F6.wireOp",EDGE,"E30.55.4"),sQuery(id+"F6.wireOp",EDGE,"E30.55.5"),sQuery(id+"F6.wireOp",EDGE,"E30.56.0"),sQuery(id+"F6.wireOp",EDGE,"E30.56.2"),sQuery(id+"F6.wireOp",EDGE,"E30.56.3"),sQuery(id+"F6.wireOp",EDGE,"E30.56.4"),sQuery(id+"F6.wireOp",EDGE,"E30.56.5"),sQuery(id+"F6.wireOp",EDGE,"E30.57.0"),sQuery(id+"F6.wireOp",EDGE,"E30.57.2"),sQuery(id+"F6.wireOp",EDGE,"E30.57.3"),sQuery(id+"F6.wireOp",EDGE,"E30.57.4"),sQuery(id+"F6.wireOp",EDGE,"E30.57.5"),sQuery(id+"F6.wireOp",EDGE,"E30.58.0"),sQuery(id+"F6.wireOp",EDGE,"E30.58.2"),sQuery(id+"F6.wireOp",EDGE,"E30.58.3"),sQuery(id+"F6.wireOp",EDGE,"E30.58.4"),sQuery(id+"F6.wireOp",EDGE,"E30.58.5"),sQuery(id+"F6.wireOp",EDGE,"E30.59.0"),sQuery(id+"F6.wireOp",EDGE,"E30.59.2"),sQuery(id+"F6.wireOp",EDGE,"E30.59.3"),sQuery(id+"F6.wireOp",EDGE,"E30.59.4"),sQuery(id+"F6.wireOp",EDGE,"E30.59.5"),sQuery(id+"F6.wireOp",EDGE,"E32")])],"isStart":false});
            var sketch = newSketch(context, id + "F8", { "sketchPlane" : qUnion([Q0])});
            skCircle(sketch, "E33.0", {"center": v(0, 0) * mm, "radius": 17.8 * mm});
            skCircle(sketch, "E34.0", {"center": v(0, 0) * mm, "radius": 25 * mm});
            skSolve(sketch);
        }
        {
            var Q0;
            Q0=makeQuery(id+"F8.imprint","IMPRINT",FACE,{"disambiguationData":[TD([[makeQuery(id+"F8.imprint","IMPRINT",EDGE,{"derivedFrom":sQuery(id+"F8.wireOp",EDGE,"E34.0")}),1.0]])]});
            var Q1;
            Q1=makeQuery(id+"F8.imprint","IMPRINT",FACE,{"disambiguationData":[TD([[makeQuery(id+"F8.imprint","IMPRINT",EDGE,{"derivedFrom":sQuery(id+"F8.wireOp",EDGE,"E33.0")}),-1.0]])]});
            var Q2;
            Q2=makeQuery(id+"F8.imprint","IMPRINT",FACE,{"disambiguationData":[TD([[makeQuery(id+"F8.imprint","IMPRINT",EDGE,{"derivedFrom":sQuery(id+"F8.wireOp",EDGE,"E33.0")}),1.0]])]});
            extrude(context, id + "F9", {"entities" : qUnion([Q0, Q1, Q2]), "operationType" : NewBodyOperationType.ADD, "depth" : 1 * mm});
        }
        {
            var Q0;
            Q0=makeQuery(id+"F9.opExtrude","CAP_FACE",FACE,{"disambiguationData":[OSD([sQuery(id+"F6.wireOp",EDGE,"E32"),sQuery(id+"F8.wireOp",EDGE,"E34.0")])],"isStart":false});
            var sketch = newSketch(context, id + "F10", { "sketchPlane" : qUnion([Q0])});
            skCircle(sketch, "E35", {"center": v(0, 0) * mm, "radius": 21.5 * mm});
            skCircle(sketch, "E36.0", {"center": v(0, 0) * mm, "radius": 10.9 * mm});
            skSolve(sketch);
        }
        {
            var Q0;
            Q0=makeQuery(id+"F10.imprint","IMPRINT",FACE,{"disambiguationData":[TD([[makeQuery(id+"F10.imprint","IMPRINT",EDGE,{"derivedFrom":sQuery(id+"F10.wireOp",EDGE,"E35")}),1.0]])]});
            extrude(context, id + "F11", {"entities" : qUnion([Q0]), "operationType" : NewBodyOperationType.REMOVE, "oppositeDirection" : true, "depth" : 6 * mm});
        }
        {
            var Q0;
            Q0=makeQuery(id+"F11.boolean.opBoolean","COPY",FACE,{"derivedFrom":makeQuery(id+"F11.opExtrude","CAP_FACE",FACE,{"disambiguationData":[OSD([sQuery(id+"F10.wireOp",EDGE,"E35"),sQuery(id+"F10.wireOp",EDGE,"E36.0")])],"isStart":false})});
            var sketch = newSketch(context, id + "F12", { "sketchPlane" : qUnion([Q0])});
            skCircle(sketch, "E37.0.0", {"center": v(0, 0) * mm, "radius": 21.5 * mm});
            skCircle(sketch, "E38.0", {"center": v(0, 0) * mm, "radius": 10.9 * mm});
            skCircle(sketch, "E39", {"center": v(0, 0) * mm, "radius": 11.85 * mm});
            skArc(sketch, "E40.0.endCap", {"start": v(-8.03, 8.73) * mm, "mid": v(-8.02, 8.73) * mm, "end": v(-8.02, 8.73) * mm});
            skLineSegment(sketch, "E40.0.left", {"start": v(-14.85, 15.56) * mm, "end": v(-8.03, 8.73) * mm});
            skLineSegment(sketch, "E40.0.right", {"start": v(-15.56, 14.85) * mm, "end": v(-8.73, 8.03) * mm});
            skArc(sketch, "E41.trimOffspring", {"start": v(-8.73, 8.02) * mm, "mid": v(-8.73, 8.02) * mm, "end": v(-8.73, 8.03) * mm});
            skLineSegment(sketch, "E42.1.0", {"start": v(-21.5, 0.5) * mm, "end": v(-11.85, 0.5) * mm});
            skLineSegment(sketch, "E42.1.1", {"start": v(-21.5, -0.5) * mm, "end": v(-11.85, -0.5) * mm});
            skArc(sketch, "E42.1.2", {"start": v(-11.85, 0.5) * mm, "mid": v(-11.84, 0.5) * mm, "end": v(-11.84, 0.5) * mm});
            skArc(sketch, "E42.1.3", {"start": v(-11.84, -0.5) * mm, "mid": v(-11.84, -0.5) * mm, "end": v(-11.85, -0.5) * mm});
            skLineSegment(sketch, "E42.2.0", {"start": v(-15.56, -14.85) * mm, "end": v(-8.73, -8.03) * mm});
            skLineSegment(sketch, "E42.2.1", {"start": v(-14.85, -15.56) * mm, "end": v(-8.03, -8.73) * mm});
            skArc(sketch, "E42.2.2", {"start": v(-8.73, -8.03) * mm, "mid": v(-8.73, -8.02) * mm, "end": v(-8.73, -8.02) * mm});
            skArc(sketch, "E42.2.3", {"start": v(-8.02, -8.73) * mm, "mid": v(-8.02, -8.73) * mm, "end": v(-8.03, -8.73) * mm});
            skLineSegment(sketch, "E42.3.0", {"start": v(-0.5, -21.5) * mm, "end": v(-0.5, -11.85) * mm});
            skLineSegment(sketch, "E42.3.1", {"start": v(0.5, -21.5) * mm, "end": v(0.5, -11.85) * mm});
            skArc(sketch, "E42.3.2", {"start": v(-0.5, -11.85) * mm, "mid": v(-0.5, -11.84) * mm, "end": v(-0.5, -11.84) * mm});
            skArc(sketch, "E42.3.3", {"start": v(0.5, -11.84) * mm, "mid": v(0.5, -11.84) * mm, "end": v(0.5, -11.85) * mm});
            skLineSegment(sketch, "E42.4.0", {"start": v(14.85, -15.56) * mm, "end": v(8.03, -8.73) * mm});
            skLineSegment(sketch, "E42.4.1", {"start": v(15.56, -14.85) * mm, "end": v(8.73, -8.03) * mm});
            skArc(sketch, "E42.4.2", {"start": v(8.03, -8.73) * mm, "mid": v(8.02, -8.73) * mm, "end": v(8.02, -8.73) * mm});
            skArc(sketch, "E42.4.3", {"start": v(8.73, -8.02) * mm, "mid": v(8.73, -8.02) * mm, "end": v(8.73, -8.03) * mm});
            skLineSegment(sketch, "E42.5.0", {"start": v(21.5, -0.5) * mm, "end": v(11.85, -0.5) * mm});
            skLineSegment(sketch, "E42.5.1", {"start": v(21.5, 0.5) * mm, "end": v(11.85, 0.5) * mm});
            skArc(sketch, "E42.5.2", {"start": v(11.85, -0.5) * mm, "mid": v(11.84, -0.5) * mm, "end": v(11.84, -0.5) * mm});
            skArc(sketch, "E42.5.3", {"start": v(11.84, 0.5) * mm, "mid": v(11.84, 0.5) * mm, "end": v(11.85, 0.5) * mm});
            skLineSegment(sketch, "E42.6.0", {"start": v(15.56, 14.85) * mm, "end": v(8.73, 8.03) * mm});
            skLineSegment(sketch, "E42.6.1", {"start": v(14.85, 15.56) * mm, "end": v(8.03, 8.73) * mm});
            skArc(sketch, "E42.6.2", {"start": v(8.73, 8.03) * mm, "mid": v(8.73, 8.02) * mm, "end": v(8.73, 8.02) * mm});
            skArc(sketch, "E42.6.3", {"start": v(8.02, 8.73) * mm, "mid": v(8.02, 8.73) * mm, "end": v(8.03, 8.73) * mm});
            skLineSegment(sketch, "E42.7.0", {"start": v(0.5, 21.5) * mm, "end": v(0.5, 11.85) * mm});
            skLineSegment(sketch, "E42.7.1", {"start": v(-0.5, 21.5) * mm, "end": v(-0.5, 11.85) * mm});
            skArc(sketch, "E42.7.2", {"start": v(0.5, 11.85) * mm, "mid": v(0.5, 11.84) * mm, "end": v(0.5, 11.84) * mm});
            skArc(sketch, "E42.7.3", {"start": v(-0.5, 11.84) * mm, "mid": v(-0.5, 11.84) * mm, "end": v(-0.5, 11.85) * mm});
            skSolve(sketch);
        }
        {
            var Q0;
            Q0=makeQuery(id+"F12.imprint","IMPRINT",FACE,{"disambiguationData":[TD([[makeQuery(id+"F12.imprint","IMPRINT",EDGE,{"derivedFrom":sQuery(id+"F12.wireOp",EDGE,"E38.0")}),-1.0]])]});
            extrude(context, id + "F13", {"entities" : qUnion([Q0]), "operationType" : NewBodyOperationType.ADD, "depth" : 6 * mm});
        }
        {
            var Q0;
            {var subQ1=sQuery(id+"F12.wireOp",EDGE,"E40.0.endCap");Q0=makeQuery(id+"F12.imprint","IMPRINT",FACE,{"disambiguationData":[TD([[makeQuery(id+"F12.imprint","IMPRINT",EDGE,{"derivedFrom":subQ1}),-1.0]])]});}
            var Q1;
            {var subQ4=sQuery(id+"F12.wireOp",EDGE,"E42.7.2");Q1=makeQuery(id+"F12.imprint","IMPRINT",FACE,{"disambiguationData":[TD([[makeQuery(id+"F12.imprint","IMPRINT",EDGE,{"derivedFrom":subQ4}),-1.0]])]});}
            var Q2;
            {var subQ0=sQuery(id+"F12.wireOp",EDGE,"E42.6.2");Q2=makeQuery(id+"F12.imprint","IMPRINT",FACE,{"disambiguationData":[TD([[makeQuery(id+"F12.imprint","IMPRINT",EDGE,{"derivedFrom":subQ0}),-1.0]])]});}
            var Q3;
            {var subQ4=sQuery(id+"F12.wireOp",EDGE,"E42.5.2");Q3=makeQuery(id+"F12.imprint","IMPRINT",FACE,{"disambiguationData":[TD([[makeQuery(id+"F12.imprint","IMPRINT",EDGE,{"derivedFrom":subQ4}),-1.0]])]});}
            var Q4;
            {var subQ0=sQuery(id+"F12.wireOp",EDGE,"E42.4.2");Q4=makeQuery(id+"F12.imprint","IMPRINT",FACE,{"disambiguationData":[TD([[makeQuery(id+"F12.imprint","IMPRINT",EDGE,{"derivedFrom":subQ0}),-1.0]])]});}
            var Q5;
            {var subQ0=sQuery(id+"F12.wireOp",EDGE,"E42.3.2");Q5=makeQuery(id+"F12.imprint","IMPRINT",FACE,{"disambiguationData":[TD([[makeQuery(id+"F12.imprint","IMPRINT",EDGE,{"derivedFrom":subQ0}),-1.0]])]});}
            var Q6;
            {var subQ6=sQuery(id+"F12.wireOp",EDGE,"E42.2.2");Q6=makeQuery(id+"F12.imprint","IMPRINT",FACE,{"disambiguationData":[TD([[makeQuery(id+"F12.imprint","IMPRINT",EDGE,{"derivedFrom":subQ6}),-1.0]])]});}
            var Q7;
            {var subQ4=sQuery(id+"F12.wireOp",EDGE,"E42.1.2");Q7=makeQuery(id+"F12.imprint","IMPRINT",FACE,{"disambiguationData":[TD([[makeQuery(id+"F12.imprint","IMPRINT",EDGE,{"derivedFrom":subQ4}),-1.0]])]});}
            extrude(context, id + "F14", {"entities" : qUnion([Q0, Q1, Q2, Q3, Q4, Q5, Q6, Q7]), "operationType" : NewBodyOperationType.ADD, "depth" : 6 * mm});
        }
        {
            var Q0;
            Q0=makeQuery(id+"F7.opExtrude","CAP_FACE",FACE,{"disambiguationData":[OSD([sQuery(id+"F6.wireOp",EDGE,"E22"),sQuery(id+"F6.wireOp",EDGE,"E25"),sQuery(id+"F6.wireOp",EDGE,"E26"),sQuery(id+"F6.wireOp",EDGE,"E27"),sQuery(id+"F6.wireOp",EDGE,"E28.filletArc"),sQuery(id+"F6.wireOp",EDGE,"E29.filletArc"),sQuery(id+"F6.wireOp",EDGE,"E30.1.0"),sQuery(id+"F6.wireOp",EDGE,"E30.1.2"),sQuery(id+"F6.wireOp",EDGE,"E30.1.3"),sQuery(id+"F6.wireOp",EDGE,"E30.1.4"),sQuery(id+"F6.wireOp",EDGE,"E30.1.5"),sQuery(id+"F6.wireOp",EDGE,"E30.2.0"),sQuery(id+"F6.wireOp",EDGE,"E30.2.2"),sQuery(id+"F6.wireOp",EDGE,"E30.2.3"),sQuery(id+"F6.wireOp",EDGE,"E30.2.4"),sQuery(id+"F6.wireOp",EDGE,"E30.2.5"),sQuery(id+"F6.wireOp",EDGE,"E30.3.0"),sQuery(id+"F6.wireOp",EDGE,"E30.3.2"),sQuery(id+"F6.wireOp",EDGE,"E30.3.3"),sQuery(id+"F6.wireOp",EDGE,"E30.3.4"),sQuery(id+"F6.wireOp",EDGE,"E30.3.5"),sQuery(id+"F6.wireOp",EDGE,"E30.4.0"),sQuery(id+"F6.wireOp",EDGE,"E30.4.2"),sQuery(id+"F6.wireOp",EDGE,"E30.4.3"),sQuery(id+"F6.wireOp",EDGE,"E30.4.4"),sQuery(id+"F6.wireOp",EDGE,"E30.4.5"),sQuery(id+"F6.wireOp",EDGE,"E30.5.0"),sQuery(id+"F6.wireOp",EDGE,"E30.5.2"),sQuery(id+"F6.wireOp",EDGE,"E30.5.3"),sQuery(id+"F6.wireOp",EDGE,"E30.5.4"),sQuery(id+"F6.wireOp",EDGE,"E30.5.5"),sQuery(id+"F6.wireOp",EDGE,"E30.6.0"),sQuery(id+"F6.wireOp",EDGE,"E30.6.2"),sQuery(id+"F6.wireOp",EDGE,"E30.6.3"),sQuery(id+"F6.wireOp",EDGE,"E30.6.4"),sQuery(id+"F6.wireOp",EDGE,"E30.6.5"),sQuery(id+"F6.wireOp",EDGE,"E30.7.0"),sQuery(id+"F6.wireOp",EDGE,"E30.7.2"),sQuery(id+"F6.wireOp",EDGE,"E30.7.3"),sQuery(id+"F6.wireOp",EDGE,"E30.7.4"),sQuery(id+"F6.wireOp",EDGE,"E30.7.5"),sQuery(id+"F6.wireOp",EDGE,"E30.8.0"),sQuery(id+"F6.wireOp",EDGE,"E30.8.2"),sQuery(id+"F6.wireOp",EDGE,"E30.8.3"),sQuery(id+"F6.wireOp",EDGE,"E30.8.4"),sQuery(id+"F6.wireOp",EDGE,"E30.8.5"),sQuery(id+"F6.wireOp",EDGE,"E30.9.0"),sQuery(id+"F6.wireOp",EDGE,"E30.9.2"),sQuery(id+"F6.wireOp",EDGE,"E30.9.3"),sQuery(id+"F6.wireOp",EDGE,"E30.9.4"),sQuery(id+"F6.wireOp",EDGE,"E30.9.5"),sQuery(id+"F6.wireOp",EDGE,"E30.10.0"),sQuery(id+"F6.wireOp",EDGE,"E30.10.2"),sQuery(id+"F6.wireOp",EDGE,"E30.10.3"),sQuery(id+"F6.wireOp",EDGE,"E30.10.4"),sQuery(id+"F6.wireOp",EDGE,"E30.10.5"),sQuery(id+"F6.wireOp",EDGE,"E30.11.0"),sQuery(id+"F6.wireOp",EDGE,"E30.11.2"),sQuery(id+"F6.wireOp",EDGE,"E30.11.3"),sQuery(id+"F6.wireOp",EDGE,"E30.11.4"),sQuery(id+"F6.wireOp",EDGE,"E30.11.5"),sQuery(id+"F6.wireOp",EDGE,"E30.12.0"),sQuery(id+"F6.wireOp",EDGE,"E30.12.2"),sQuery(id+"F6.wireOp",EDGE,"E30.12.3"),sQuery(id+"F6.wireOp",EDGE,"E30.12.4"),sQuery(id+"F6.wireOp",EDGE,"E30.12.5"),sQuery(id+"F6.wireOp",EDGE,"E30.13.0"),sQuery(id+"F6.wireOp",EDGE,"E30.13.2"),sQuery(id+"F6.wireOp",EDGE,"E30.13.3"),sQuery(id+"F6.wireOp",EDGE,"E30.13.4"),sQuery(id+"F6.wireOp",EDGE,"E30.13.5"),sQuery(id+"F6.wireOp",EDGE,"E30.14.0"),sQuery(id+"F6.wireOp",EDGE,"E30.14.2"),sQuery(id+"F6.wireOp",EDGE,"E30.14.3"),sQuery(id+"F6.wireOp",EDGE,"E30.14.4"),sQuery(id+"F6.wireOp",EDGE,"E30.14.5"),sQuery(id+"F6.wireOp",EDGE,"E30.15.0"),sQuery(id+"F6.wireOp",EDGE,"E30.15.2"),sQuery(id+"F6.wireOp",EDGE,"E30.15.3"),sQuery(id+"F6.wireOp",EDGE,"E30.15.4"),sQuery(id+"F6.wireOp",EDGE,"E30.15.5"),sQuery(id+"F6.wireOp",EDGE,"E30.16.0"),sQuery(id+"F6.wireOp",EDGE,"E30.16.2"),sQuery(id+"F6.wireOp",EDGE,"E30.16.3"),sQuery(id+"F6.wireOp",EDGE,"E30.16.4"),sQuery(id+"F6.wireOp",EDGE,"E30.16.5"),sQuery(id+"F6.wireOp",EDGE,"E30.17.0"),sQuery(id+"F6.wireOp",EDGE,"E30.17.2"),sQuery(id+"F6.wireOp",EDGE,"E30.17.3"),sQuery(id+"F6.wireOp",EDGE,"E30.17.4"),sQuery(id+"F6.wireOp",EDGE,"E30.17.5"),sQuery(id+"F6.wireOp",EDGE,"E30.18.0"),sQuery(id+"F6.wireOp",EDGE,"E30.18.2"),sQuery(id+"F6.wireOp",EDGE,"E30.18.3"),sQuery(id+"F6.wireOp",EDGE,"E30.18.4"),sQuery(id+"F6.wireOp",EDGE,"E30.18.5"),sQuery(id+"F6.wireOp",EDGE,"E30.19.0"),sQuery(id+"F6.wireOp",EDGE,"E30.19.2"),sQuery(id+"F6.wireOp",EDGE,"E30.19.3"),sQuery(id+"F6.wireOp",EDGE,"E30.19.4"),sQuery(id+"F6.wireOp",EDGE,"E30.19.5"),sQuery(id+"F6.wireOp",EDGE,"E30.20.0"),sQuery(id+"F6.wireOp",EDGE,"E30.20.2"),sQuery(id+"F6.wireOp",EDGE,"E30.20.3"),sQuery(id+"F6.wireOp",EDGE,"E30.20.4"),sQuery(id+"F6.wireOp",EDGE,"E30.20.5"),sQuery(id+"F6.wireOp",EDGE,"E30.21.0"),sQuery(id+"F6.wireOp",EDGE,"E30.21.2"),sQuery(id+"F6.wireOp",EDGE,"E30.21.3"),sQuery(id+"F6.wireOp",EDGE,"E30.21.4"),sQuery(id+"F6.wireOp",EDGE,"E30.21.5"),sQuery(id+"F6.wireOp",EDGE,"E30.22.0"),sQuery(id+"F6.wireOp",EDGE,"E30.22.2"),sQuery(id+"F6.wireOp",EDGE,"E30.22.3"),sQuery(id+"F6.wireOp",EDGE,"E30.22.4"),sQuery(id+"F6.wireOp",EDGE,"E30.22.5"),sQuery(id+"F6.wireOp",EDGE,"E30.23.0"),sQuery(id+"F6.wireOp",EDGE,"E30.23.2"),sQuery(id+"F6.wireOp",EDGE,"E30.23.3"),sQuery(id+"F6.wireOp",EDGE,"E30.23.4"),sQuery(id+"F6.wireOp",EDGE,"E30.23.5"),sQuery(id+"F6.wireOp",EDGE,"E30.24.0"),sQuery(id+"F6.wireOp",EDGE,"E30.24.2"),sQuery(id+"F6.wireOp",EDGE,"E30.24.3"),sQuery(id+"F6.wireOp",EDGE,"E30.24.4"),sQuery(id+"F6.wireOp",EDGE,"E30.24.5"),sQuery(id+"F6.wireOp",EDGE,"E30.25.0"),sQuery(id+"F6.wireOp",EDGE,"E30.25.2"),sQuery(id+"F6.wireOp",EDGE,"E30.25.3"),sQuery(id+"F6.wireOp",EDGE,"E30.25.4"),sQuery(id+"F6.wireOp",EDGE,"E30.25.5"),sQuery(id+"F6.wireOp",EDGE,"E30.26.0"),sQuery(id+"F6.wireOp",EDGE,"E30.26.2"),sQuery(id+"F6.wireOp",EDGE,"E30.26.3"),sQuery(id+"F6.wireOp",EDGE,"E30.26.4"),sQuery(id+"F6.wireOp",EDGE,"E30.26.5"),sQuery(id+"F6.wireOp",EDGE,"E30.27.0"),sQuery(id+"F6.wireOp",EDGE,"E30.27.2"),sQuery(id+"F6.wireOp",EDGE,"E30.27.3"),sQuery(id+"F6.wireOp",EDGE,"E30.27.4"),sQuery(id+"F6.wireOp",EDGE,"E30.27.5"),sQuery(id+"F6.wireOp",EDGE,"E30.28.0"),sQuery(id+"F6.wireOp",EDGE,"E30.28.2"),sQuery(id+"F6.wireOp",EDGE,"E30.28.3"),sQuery(id+"F6.wireOp",EDGE,"E30.28.4"),sQuery(id+"F6.wireOp",EDGE,"E30.28.5"),sQuery(id+"F6.wireOp",EDGE,"E30.29.0"),sQuery(id+"F6.wireOp",EDGE,"E30.29.2"),sQuery(id+"F6.wireOp",EDGE,"E30.29.3"),sQuery(id+"F6.wireOp",EDGE,"E30.29.4"),sQuery(id+"F6.wireOp",EDGE,"E30.29.5"),sQuery(id+"F6.wireOp",EDGE,"E30.30.0"),sQuery(id+"F6.wireOp",EDGE,"E30.30.2"),sQuery(id+"F6.wireOp",EDGE,"E30.30.3"),sQuery(id+"F6.wireOp",EDGE,"E30.30.4"),sQuery(id+"F6.wireOp",EDGE,"E30.30.5"),sQuery(id+"F6.wireOp",EDGE,"E30.31.0"),sQuery(id+"F6.wireOp",EDGE,"E30.31.2"),sQuery(id+"F6.wireOp",EDGE,"E30.31.3"),sQuery(id+"F6.wireOp",EDGE,"E30.31.4"),sQuery(id+"F6.wireOp",EDGE,"E30.31.5"),sQuery(id+"F6.wireOp",EDGE,"E30.32.0"),sQuery(id+"F6.wireOp",EDGE,"E30.32.2"),sQuery(id+"F6.wireOp",EDGE,"E30.32.3"),sQuery(id+"F6.wireOp",EDGE,"E30.32.4"),sQuery(id+"F6.wireOp",EDGE,"E30.32.5"),sQuery(id+"F6.wireOp",EDGE,"E30.33.0"),sQuery(id+"F6.wireOp",EDGE,"E30.33.2"),sQuery(id+"F6.wireOp",EDGE,"E30.33.3"),sQuery(id+"F6.wireOp",EDGE,"E30.33.4"),sQuery(id+"F6.wireOp",EDGE,"E30.33.5"),sQuery(id+"F6.wireOp",EDGE,"E30.34.0"),sQuery(id+"F6.wireOp",EDGE,"E30.34.2"),sQuery(id+"F6.wireOp",EDGE,"E30.34.3"),sQuery(id+"F6.wireOp",EDGE,"E30.34.4"),sQuery(id+"F6.wireOp",EDGE,"E30.34.5"),sQuery(id+"F6.wireOp",EDGE,"E30.35.0"),sQuery(id+"F6.wireOp",EDGE,"E30.35.2"),sQuery(id+"F6.wireOp",EDGE,"E30.35.3"),sQuery(id+"F6.wireOp",EDGE,"E30.35.4"),sQuery(id+"F6.wireOp",EDGE,"E30.35.5"),sQuery(id+"F6.wireOp",EDGE,"E30.36.0"),sQuery(id+"F6.wireOp",EDGE,"E30.36.2"),sQuery(id+"F6.wireOp",EDGE,"E30.36.3"),sQuery(id+"F6.wireOp",EDGE,"E30.36.4"),sQuery(id+"F6.wireOp",EDGE,"E30.36.5"),sQuery(id+"F6.wireOp",EDGE,"E30.37.0"),sQuery(id+"F6.wireOp",EDGE,"E30.37.2"),sQuery(id+"F6.wireOp",EDGE,"E30.37.3"),sQuery(id+"F6.wireOp",EDGE,"E30.37.4"),sQuery(id+"F6.wireOp",EDGE,"E30.37.5"),sQuery(id+"F6.wireOp",EDGE,"E30.38.0"),sQuery(id+"F6.wireOp",EDGE,"E30.38.2"),sQuery(id+"F6.wireOp",EDGE,"E30.38.3"),sQuery(id+"F6.wireOp",EDGE,"E30.38.4"),sQuery(id+"F6.wireOp",EDGE,"E30.38.5"),sQuery(id+"F6.wireOp",EDGE,"E30.39.0"),sQuery(id+"F6.wireOp",EDGE,"E30.39.2"),sQuery(id+"F6.wireOp",EDGE,"E30.39.3"),sQuery(id+"F6.wireOp",EDGE,"E30.39.4"),sQuery(id+"F6.wireOp",EDGE,"E30.39.5"),sQuery(id+"F6.wireOp",EDGE,"E30.40.0"),sQuery(id+"F6.wireOp",EDGE,"E30.40.2"),sQuery(id+"F6.wireOp",EDGE,"E30.40.3"),sQuery(id+"F6.wireOp",EDGE,"E30.40.4"),sQuery(id+"F6.wireOp",EDGE,"E30.40.5"),sQuery(id+"F6.wireOp",EDGE,"E30.41.0"),sQuery(id+"F6.wireOp",EDGE,"E30.41.2"),sQuery(id+"F6.wireOp",EDGE,"E30.41.3"),sQuery(id+"F6.wireOp",EDGE,"E30.41.4"),sQuery(id+"F6.wireOp",EDGE,"E30.41.5"),sQuery(id+"F6.wireOp",EDGE,"E30.42.0"),sQuery(id+"F6.wireOp",EDGE,"E30.42.2"),sQuery(id+"F6.wireOp",EDGE,"E30.42.3"),sQuery(id+"F6.wireOp",EDGE,"E30.42.4"),sQuery(id+"F6.wireOp",EDGE,"E30.42.5"),sQuery(id+"F6.wireOp",EDGE,"E30.43.0"),sQuery(id+"F6.wireOp",EDGE,"E30.43.2"),sQuery(id+"F6.wireOp",EDGE,"E30.43.3"),sQuery(id+"F6.wireOp",EDGE,"E30.43.4"),sQuery(id+"F6.wireOp",EDGE,"E30.43.5"),sQuery(id+"F6.wireOp",EDGE,"E30.44.0"),sQuery(id+"F6.wireOp",EDGE,"E30.44.2"),sQuery(id+"F6.wireOp",EDGE,"E30.44.3"),sQuery(id+"F6.wireOp",EDGE,"E30.44.4"),sQuery(id+"F6.wireOp",EDGE,"E30.44.5"),sQuery(id+"F6.wireOp",EDGE,"E30.45.0"),sQuery(id+"F6.wireOp",EDGE,"E30.45.2"),sQuery(id+"F6.wireOp",EDGE,"E30.45.3"),sQuery(id+"F6.wireOp",EDGE,"E30.45.4"),sQuery(id+"F6.wireOp",EDGE,"E30.45.5"),sQuery(id+"F6.wireOp",EDGE,"E30.46.0"),sQuery(id+"F6.wireOp",EDGE,"E30.46.2"),sQuery(id+"F6.wireOp",EDGE,"E30.46.3"),sQuery(id+"F6.wireOp",EDGE,"E30.46.4"),sQuery(id+"F6.wireOp",EDGE,"E30.46.5"),sQuery(id+"F6.wireOp",EDGE,"E30.47.0"),sQuery(id+"F6.wireOp",EDGE,"E30.47.2"),sQuery(id+"F6.wireOp",EDGE,"E30.47.3"),sQuery(id+"F6.wireOp",EDGE,"E30.47.4"),sQuery(id+"F6.wireOp",EDGE,"E30.47.5"),sQuery(id+"F6.wireOp",EDGE,"E30.48.0"),sQuery(id+"F6.wireOp",EDGE,"E30.48.2"),sQuery(id+"F6.wireOp",EDGE,"E30.48.3"),sQuery(id+"F6.wireOp",EDGE,"E30.48.4"),sQuery(id+"F6.wireOp",EDGE,"E30.48.5"),sQuery(id+"F6.wireOp",EDGE,"E30.49.0"),sQuery(id+"F6.wireOp",EDGE,"E30.49.2"),sQuery(id+"F6.wireOp",EDGE,"E30.49.3"),sQuery(id+"F6.wireOp",EDGE,"E30.49.4"),sQuery(id+"F6.wireOp",EDGE,"E30.49.5"),sQuery(id+"F6.wireOp",EDGE,"E30.50.0"),sQuery(id+"F6.wireOp",EDGE,"E30.50.2"),sQuery(id+"F6.wireOp",EDGE,"E30.50.3"),sQuery(id+"F6.wireOp",EDGE,"E30.50.4"),sQuery(id+"F6.wireOp",EDGE,"E30.50.5"),sQuery(id+"F6.wireOp",EDGE,"E30.51.0"),sQuery(id+"F6.wireOp",EDGE,"E30.51.2"),sQuery(id+"F6.wireOp",EDGE,"E30.51.3"),sQuery(id+"F6.wireOp",EDGE,"E30.51.4"),sQuery(id+"F6.wireOp",EDGE,"E30.51.5"),sQuery(id+"F6.wireOp",EDGE,"E30.52.0"),sQuery(id+"F6.wireOp",EDGE,"E30.52.2"),sQuery(id+"F6.wireOp",EDGE,"E30.52.3"),sQuery(id+"F6.wireOp",EDGE,"E30.52.4"),sQuery(id+"F6.wireOp",EDGE,"E30.52.5"),sQuery(id+"F6.wireOp",EDGE,"E30.53.0"),sQuery(id+"F6.wireOp",EDGE,"E30.53.2"),sQuery(id+"F6.wireOp",EDGE,"E30.53.3"),sQuery(id+"F6.wireOp",EDGE,"E30.53.4"),sQuery(id+"F6.wireOp",EDGE,"E30.53.5"),sQuery(id+"F6.wireOp",EDGE,"E30.54.0"),sQuery(id+"F6.wireOp",EDGE,"E30.54.2"),sQuery(id+"F6.wireOp",EDGE,"E30.54.3"),sQuery(id+"F6.wireOp",EDGE,"E30.54.4"),sQuery(id+"F6.wireOp",EDGE,"E30.54.5"),sQuery(id+"F6.wireOp",EDGE,"E30.55.0"),sQuery(id+"F6.wireOp",EDGE,"E30.55.2"),sQuery(id+"F6.wireOp",EDGE,"E30.55.3"),sQuery(id+"F6.wireOp",EDGE,"E30.55.4"),sQuery(id+"F6.wireOp",EDGE,"E30.55.5"),sQuery(id+"F6.wireOp",EDGE,"E30.56.0"),sQuery(id+"F6.wireOp",EDGE,"E30.56.2"),sQuery(id+"F6.wireOp",EDGE,"E30.56.3"),sQuery(id+"F6.wireOp",EDGE,"E30.56.4"),sQuery(id+"F6.wireOp",EDGE,"E30.56.5"),sQuery(id+"F6.wireOp",EDGE,"E30.57.0"),sQuery(id+"F6.wireOp",EDGE,"E30.57.2"),sQuery(id+"F6.wireOp",EDGE,"E30.57.3"),sQuery(id+"F6.wireOp",EDGE,"E30.57.4"),sQuery(id+"F6.wireOp",EDGE,"E30.57.5"),sQuery(id+"F6.wireOp",EDGE,"E30.58.0"),sQuery(id+"F6.wireOp",EDGE,"E30.58.2"),sQuery(id+"F6.wireOp",EDGE,"E30.58.3"),sQuery(id+"F6.wireOp",EDGE,"E30.58.4"),sQuery(id+"F6.wireOp",EDGE,"E30.58.5"),sQuery(id+"F6.wireOp",EDGE,"E30.59.0"),sQuery(id+"F6.wireOp",EDGE,"E30.59.2"),sQuery(id+"F6.wireOp",EDGE,"E30.59.3"),sQuery(id+"F6.wireOp",EDGE,"E30.59.4"),sQuery(id+"F6.wireOp",EDGE,"E30.59.5"),sQuery(id+"F6.wireOp",EDGE,"E32")])],"isStart":true});
            var sketch = newSketch(context, id + "F15", { "sketchPlane" : qUnion([Q0])});
            skCircle(sketch, "E43.0", {"center": v(0, 0) * mm, "radius": 10.9 * mm});
            skCircle(sketch, "E44.0", {"center": v(0, 0) * mm, "radius": 11.85 * mm});
            skSolve(sketch);
        }
        {
            var Q0;
            Q0=makeQuery(id+"F15.imprint","IMPRINT",FACE,{"disambiguationData":[TD([[makeQuery(id+"F15.imprint","IMPRINT",EDGE,{"derivedFrom":sQuery(id+"F15.wireOp",EDGE,"E43.0")}),1.0]])]});
            extrude(context, id + "F16", {"entities" : qUnion([Q0]), "operationType" : NewBodyOperationType.ADD, "depth" : 1 * mm});
        }
    });
